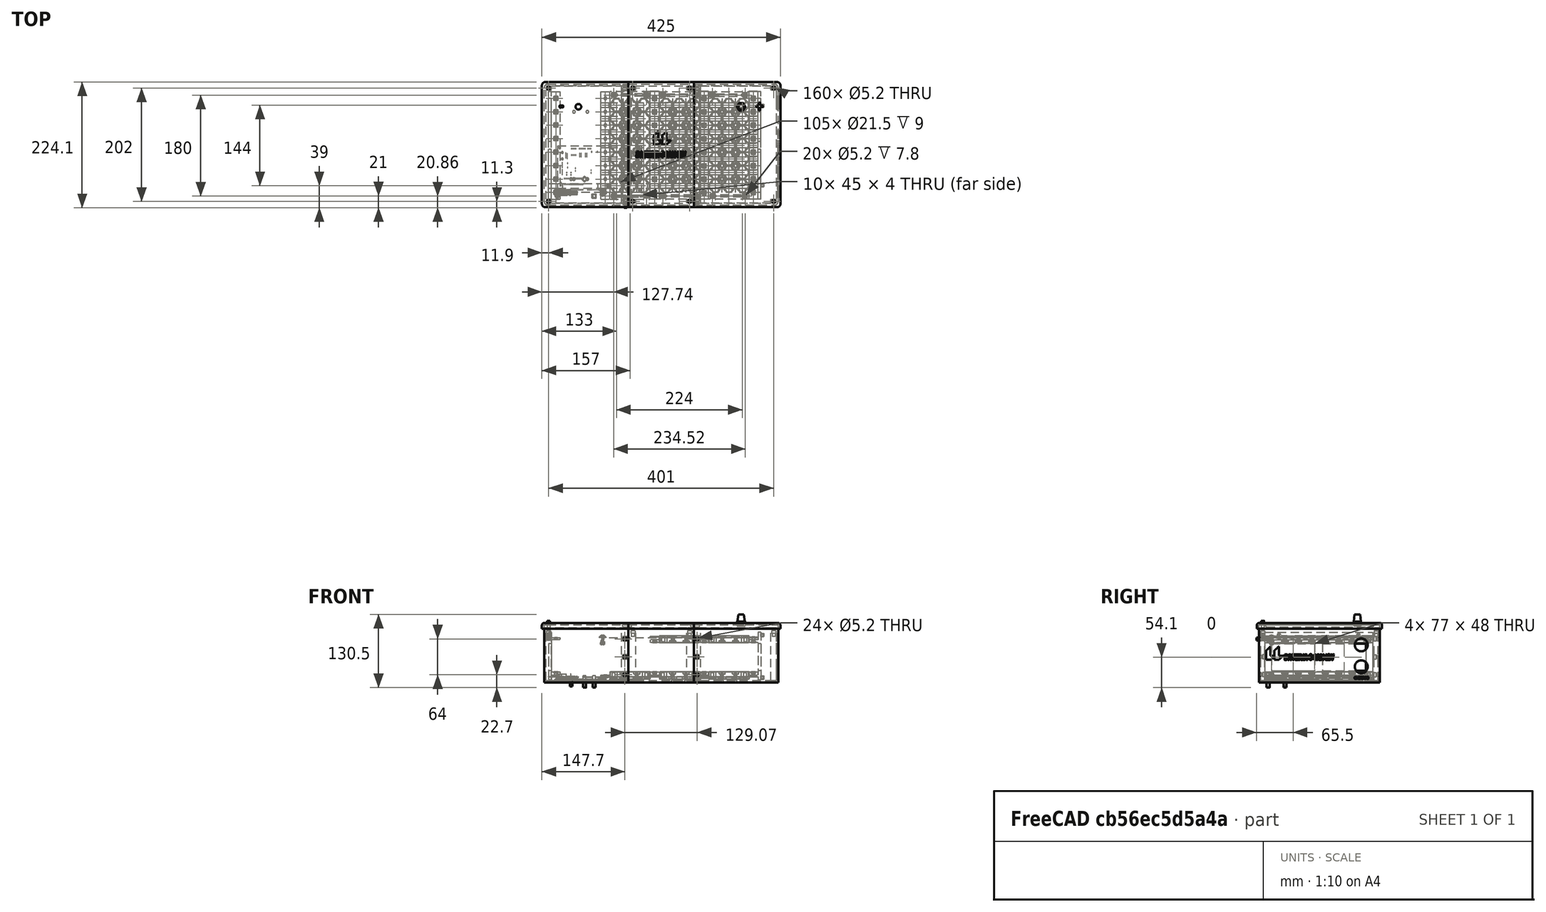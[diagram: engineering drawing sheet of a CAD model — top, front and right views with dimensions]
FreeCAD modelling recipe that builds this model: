
FCSTD DOCUMENT  (FreeCAD 0.19R24276 (Git))
Label: Caja_bateria_horizontal_10
License: All rights reserved
LicenseURL: http://en.wikipedia.org/wiki/All_rights_reserved
objects: TechDraw::DrawViewDimension×195, Part::Feature×111, App::Part×110, Part::FeaturePython×109, Mesh::Feature×86, Part::Cut×45, Part::Box×43, Part::MultiFuse×39, TechDraw::DrawProjGroupItem×37, App::DocumentObjectGroup×23, Part::Cylinder×18, TechDraw::DrawSVGTemplate×13, TechDraw::DrawPage×13, TechDraw::DrawProjGroup×12, TechDraw::DrawViewSymbol×12, TechDraw::DrawViewBalloon×11, TechDraw::DrawViewPart×10, Part::Fillet×6, Part::Extrusion×5, Part::Part2DObjectPython×4, +8 more types
note: 367 computed .brp shape members not serialized (recipe doc carries the construction recipe); baked Part::Feature solids carry a one-line shape summary decoded from their .brp

FEATURE [Mesh::Feature] _1700_Cell  label="21700_Cell"
  Placement = pos=(17,12,6) rot=(1,0,0;1.5708rad)
FEATURE [Part::Feature] Part__Feature  label="SOLID"
  shape: bbox 2.54 x 7.62 x 11.54 mm, 76 faces (baked)
FEATURE [App::Part] PinHeader_1x03_P2_54mm_Vertical  label="PinHeader_1x03_P2.54mm_Vertical"
  Group = -> [Part__Feature]
  Origin = -> Origin084
  Placement = pos=(53.975,78.359,1.65) rot=(0,0,1;1.5708rad)
FEATURE [Part::Feature] Part__Feature001  label="SOLID001"
  shape: bbox 2.54 x 12.7 x 11.54 mm, 124 faces (baked)
FEATURE [App::Part] PinHeader_1x05_P2_54mm_Vertical  label="PinHeader_1x05_P2.54mm_Vertical"
  Group = -> [Part__Feature001]
  Origin = -> Origin085
  Placement = pos=(142.875,23.749,1.65) rot=(0,0,1;0rad)
FEATURE [Part::Feature] Part__Feature002  label="SOLID002"
  shape: bbox 2.54 x 12.7 x 11.54 mm, 124 faces (baked)
FEATURE [App::Part] PinHeader_1x05_P2_54mm_Vertical001  label="PinHeader_1x05_P2.54mm_Vertical001"
  Group = -> [Part__Feature002]
  Origin = -> Origin086
  Placement = pos=(38.735,78.359,1.65) rot=(0,0,1;1.5708rad)
FEATURE [Part::Feature] Part__Feature003  label="SOLID003"
  shape: bbox 5.08 x 7.62 x 11.54 mm, 130 faces (baked)
FEATURE [App::Part] PinHeader_2x03_P2_54mm_Vertical  label="PinHeader_2x03_P2.54mm_Vertical"
  Group = -> [Part__Feature003]
  Origin = -> Origin087
  Placement = pos=(39.37,69.469,1.65) rot=(0,0,1;0rad)
FEATURE [Part::Feature] Part__Feature004  label="SOLID004"
  shape: bbox 5.08 x 7.62 x 11.54 mm, 130 faces (baked)
FEATURE [App::Part] PinHeader_2x03_P2_54mm_Vertical001  label="PinHeader_2x03_P2.54mm_Vertical001"
  Group = -> [Part__Feature004]
  Origin = -> Origin088
  Placement = pos=(49.53,69.469,1.65) rot=(0,0,1;0rad)
FEATURE [Part::Feature] Part__Feature005  label="SOLID005"
  shape: bbox 2.54 x 10.16 x 11.54 mm, 100 faces (baked)
FEATURE [App::Part] PinHeader_1x04_P2_54mm_Vertical  label="PinHeader_1x04_P2.54mm_Vertical"
  Group = -> [Part__Feature005]
  Origin = -> Origin089
  Placement = pos=(8.255,40.259,1.65) rot=(0,0,1;0rad)
FEATURE [Part::Feature] Part__Feature006  label="SOLID006"
  shape: bbox 2.54 x 10.16 x 11.54 mm, 100 faces (baked)
FEATURE [App::Part] PinHeader_1x04_P2_54mm_Vertical001  label="PinHeader_1x04_P2.54mm_Vertical001"
  Group = -> [Part__Feature006]
  Origin = -> Origin090
  Placement = pos=(24.765,66.929,1.65) rot=(0,0,1;1.5708rad)
FEATURE [Part::Feature] Part__Feature007  label="SOLID007"
  shape: bbox 2.54 x 10.16 x 11.54 mm, 100 faces (baked)
FEATURE [App::Part] PinHeader_1x04_P2_54mm_Vertical002  label="PinHeader_1x04_P2.54mm_Vertical002"
  Group = -> [Part__Feature007]
  Origin = -> Origin091
  Placement = pos=(24.765,78.359,1.65) rot=(0,0,1;1.5708rad)
FEATURE [Part::Feature] Part__Feature008  label="SOLID008"
  shape: bbox 2.54 x 10.16 x 11.54 mm, 100 faces (baked)
FEATURE [App::Part] PinHeader_1x04_P2_54mm_Vertical003  label="PinHeader_1x04_P2.54mm_Vertical003"
  Group = -> [Part__Feature008]
  Origin = -> Origin092
  Placement = pos=(8.255,52.959,1.65) rot=(0,0,1;0rad)
FEATURE [Part::Feature] Part__Feature009  label="SOLID009"
  shape: bbox 37.4 x 5.75 x 10.4 mm, 381 faces (baked)
FEATURE [App::Part] JST_XH_B14B_XH_A_1x14_P2_50mm_Vertical  label="JST_XH_B14B-XH-A_1x14_P2.50mm_Vertical"
  Group = -> [Part__Feature009]
  Origin = -> Origin093
  Placement = pos=(53.467,5.08,1.65) rot=(0,0,1;0rad)
FEATURE [Part::Feature] Part__Feature010  label="SOLID010"
  shape: bbox 37.4 x 5.75 x 10.4 mm, 381 faces (baked)
FEATURE [App::Part] JST_XH_B14B_XH_A_1x14_P2_50mm_Vertical001  label="JST_XH_B14B-XH-A_1x14_P2.50mm_Vertical001"
  Group = -> [Part__Feature010]
  Origin = -> Origin094
  Placement = pos=(12.065,14.732,1.65) rot=(0,0,1;0rad)
FEATURE [Part::Feature] Part__Feature011  label="SOLID011"
  shape: bbox 37.4 x 5.75 x 10.4 mm, 381 faces (baked)
FEATURE [App::Part] JST_XH_B14B_XH_A_1x14_P2_50mm_Vertical002  label="JST_XH_B14B-XH-A_1x14_P2.50mm_Vertical002"
  Group = -> [Part__Feature011]
  Origin = -> Origin095
  Placement = pos=(12.065,5.08,1.65) rot=(0,0,1;0rad)
FEATURE [Part::Feature] Part__Feature012  label="SOLID012"
  shape: bbox 37.4 x 5.75 x 10.4 mm, 381 faces (baked)
FEATURE [App::Part] JST_XH_B14B_XH_A_1x14_P2_50mm_Vertical003  label="JST_XH_B14B-XH-A_1x14_P2.50mm_Vertical003"
  Group = -> [Part__Feature012]
  Origin = -> Origin096
  Placement = pos=(12.065,25.019,1.65) rot=(0,0,1;0rad)
FEATURE [Part::Feature] Part__Feature013  label="SOLID013"
  shape: bbox 3.2 x 1.6 x 0.55 mm, 26 faces (baked)
FEATURE [App::Part] R_1206_3216Metric
  Group = -> [Part__Feature013]
  Origin = -> Origin097
  Placement = pos=(74.676,52.578,1.65) rot=(0,0,1;1.5708rad)
FEATURE [Part::Feature] Part__Feature014  label="SOLID014"
  shape: bbox 3.2 x 1.6 x 0.55 mm, 26 faces (baked)
FEATURE [App::Part] R_1206_3216Metric001
  Group = -> [Part__Feature014]
  Origin = -> Origin098
  Placement = pos=(64.135,36.068,1.65) rot=(0,0,-1;1.5708rad)
FEATURE [Part::Feature] Part__Feature015  label="SOLID015"
  shape: bbox 3.2 x 1.6 x 0.55 mm, 26 faces (baked)
FEATURE [App::Part] R_1206_3216Metric002
  Group = -> [Part__Feature015]
  Origin = -> Origin099
  Placement = pos=(3.429,15.24,1.65) rot=(0,0,-1;1.5708rad)
FEATURE [Part::Feature] Part__Feature016  label="SOLID016"
  shape: bbox 3.2 x 1.6 x 0.55 mm, 26 faces (baked)
FEATURE [App::Part] R_1206_3216Metric003
  Group = -> [Part__Feature016]
  Origin = -> Origin100
  Placement = pos=(106.934,24.638,1.65) rot=(0,0,1;0rad)
FEATURE [Part::Feature] Part__Feature017  label="SOLID017"
  shape: bbox 2.5 x 3 x 1.2 mm, 76 faces (baked)
FEATURE [App::Part] SOT_23  label="SOT-23"
  Group = -> [Part__Feature017]
  Origin = -> Origin101
  Placement = pos=(100.33,49.53,1.65) rot=(0,0,1;0rad)
FEATURE [Part::Feature] Part__Feature018  label="SOLID018"
  shape: bbox 9 x 9 x 1.1 mm, 524 faces (baked)
FEATURE [App::Part] TQFP_32_7x7mm_P0_8mm  label="TQFP-32_7x7mm_P0.8mm"
  Group = -> [Part__Feature018]
  Origin = -> Origin102
  Placement = pos=(65.151,54.102,1.65) rot=(0,0,1;0rad)
FEATURE [Part::Feature] Part__Feature019  label="SOLID019"
  shape: bbox 9 x 9 x 1.1 mm, 764 faces (baked)
FEATURE [App::Part] TQFP_48_7x7mm_P0_5mm  label="TQFP-48_7x7mm_P0.5mm"
  Group = -> [Part__Feature019]
  Origin = -> Origin103
  Placement = pos=(67.945,22.098,1.65) rot=(0,0,1;1.5708rad)
FEATURE [Part::Feature] Part__Feature020  label="SOLID020"
  shape: bbox 11.05 x 4.65 x 7 mm, 26 faces (baked)
FEATURE [App::Part] Crystal_HC49_4H_Vertical  label="Crystal_HC49-4H_Vertical"
  Group = -> [Part__Feature020]
  Origin = -> Origin104
  Placement = pos=(59.563,35.179,1.65) rot=(0,0,1;1.5708rad)
FEATURE [Part::Feature] Part__Feature021  label="SOLID021"
  shape: bbox 11.05 x 4.65 x 7 mm, 26 faces (baked)
FEATURE [App::Part] Crystal_HC49_4H_Vertical001  label="Crystal_HC49-4H_Vertical001"
  Group = -> [Part__Feature021]
  Origin = -> Origin105
  Placement = pos=(31.75,43.434,1.65) rot=(0,0,-1;1.5708rad)
FEATURE [Part::Feature] Part__Feature022  label="SOLID022"
  shape: bbox 10.35 x 15.9 x 2.99 mm, 756 faces (baked)
FEATURE [App::Part] SSOP_48_7_5x15_9mm_P0_635mm  label="SSOP-48_7.5x15.9mm_P0.635mm"
  Group = -> [Part__Feature022]
  Origin = -> Origin106
  Placement = pos=(124.46,46.609,1.65) rot=(0,0,1;0rad)
FEATURE [Part::Feature] Part__Feature023  label="SOLID023"
  shape: bbox 6 x 4.9 x 1.75 mm, 156 faces (baked)
FEATURE [App::Part] SOIC_8_3_9x4_9mm_P1_27mm  label="SOIC-8_3.9x4.9mm_P1.27mm"
  Group = -> [Part__Feature023]
  Origin = -> Origin107
  Placement = pos=(26.035,54.864,1.65) rot=(0,0,1;0rad)
FEATURE [Part::Feature] Part__Feature024  label="SOLID024"
  shape: bbox 10.3 x 11.55 x 2.75 mm, 306 faces (baked)
FEATURE [App::Part] SOIC_18W_7_5x11_6mm_P1_27mm  label="SOIC-18W_7.5x11.6mm_P1.27mm"
  Group = -> [Part__Feature024]
  Origin = -> Origin108
  Placement = pos=(43.815,41.529,1.65) rot=(0,0,1;0rad)
FEATURE [Part::Feature] Part__Feature025  label="SOLID025"
  shape: bbox 3.2 x 1.6 x 0.55 mm, 26 faces (baked)
FEATURE [App::Part] R_1206_3216Metric004
  Group = -> [Part__Feature025]
  Origin = -> Origin109
  Placement = pos=(87.122,52.578,1.65) rot=(0,0,1;0rad)
FEATURE [Part::Feature] Part__Feature026  label="SOLID026"
  shape: bbox 3.2 x 1.6 x 0.55 mm, 26 faces (baked)
FEATURE [App::Part] R_1206_3216Metric005
  Group = -> [Part__Feature026]
  Origin = -> Origin110
  Placement = pos=(87.63,39.243,1.65) rot=(0,0,1;0rad)
FEATURE [Part::Feature] Part__Feature027  label="SOLID027"
  shape: bbox 3.2 x 1.6 x 0.55 mm, 26 faces (baked)
FEATURE [App::Part] R_1206_3216Metric006
  Group = -> [Part__Feature027]
  Origin = -> Origin111
  Placement = pos=(87.122,25.273,1.65) rot=(0,0,1;0rad)
FEATURE [Part::Feature] Part__Feature028  label="SOLID028"
  shape: bbox 2 x 1.2 x 0.45 mm, 26 faces (baked)
FEATURE [App::Part] R_0805_2012Metric
  Group = -> [Part__Feature028]
  Origin = -> Origin112
  Placement = pos=(82.042,52.578,1.65) rot=(0,0,1;0rad)
FEATURE [Part::Feature] Part__Feature029  label="SOLID029"
  shape: bbox 2 x 1.2 x 0.45 mm, 26 faces (baked)
FEATURE [App::Part] R_0805_2012Metric001
  Group = -> [Part__Feature029]
  Origin = -> Origin113
  Placement = pos=(82.55,39.243,1.65) rot=(0,0,1;0rad)
FEATURE [Part::Feature] Part__Feature030  label="SOLID030"
  shape: bbox 2 x 1.2 x 0.45 mm, 26 faces (baked)
FEATURE [App::Part] R_0805_2012Metric002
  Group = -> [Part__Feature030]
  Origin = -> Origin114
  Placement = pos=(82.042,25.273,1.65) rot=(0,0,1;0rad)
FEATURE [Part::Feature] Part__Feature031  label="SOLID031"
  shape: bbox 2 x 1.2 x 0.45 mm, 26 faces (baked)
FEATURE [App::Part] R_0805_2012Metric003
  Group = -> [Part__Feature031]
  Origin = -> Origin115
  Placement = pos=(101.854,24.638,1.65) rot=(0,0,1;0rad)
FEATURE [Part::Feature] Part__Feature032  label="SOLID032"
  shape: bbox 3.2 x 1.6 x 0.55 mm, 26 faces (baked)
FEATURE [App::Part] R_1206_3216Metric007
  Group = -> [Part__Feature032]
  Origin = -> Origin116
  Placement = pos=(85.979,65.278,1.65) rot=(0,0,1;0rad)
FEATURE [Part::Feature] Part__Feature033  label="SOLID033"
  shape: bbox 3.2 x 1.6 x 0.55 mm, 26 faces (baked)
FEATURE [App::Part] R_1206_3216Metric008
  Group = -> [Part__Feature033]
  Origin = -> Origin117
  Placement = pos=(85.09,76.327,1.65) rot=(0,0,1;0rad)
FEATURE [Part::Feature] Part__Feature034  label="SOLID034"
  shape: bbox 3.2 x 1.6 x 0.55 mm, 26 faces (baked)
FEATURE [App::Part] R_1206_3216Metric009
  Group = -> [Part__Feature034]
  Origin = -> Origin118
  Placement = pos=(102.108,75.311,1.65) rot=(0,0,1;0rad)
FEATURE [Part::Feature] Part__Feature035  label="SOLID035"
  shape: bbox 3.2 x 1.6 x 0.55 mm, 26 faces (baked)
FEATURE [App::Part] R_1206_3216Metric010
  Group = -> [Part__Feature035]
  Origin = -> Origin119
  Placement = pos=(126.619,24.892,1.65) rot=(0,0,1;0rad)
FEATURE [Part::Feature] Part__Feature036  label="SOLID036"
  shape: bbox 2 x 1.2 x 0.45 mm, 26 faces (baked)
FEATURE [App::Part] R_0805_2012Metric004
  Group = -> [Part__Feature036]
  Origin = -> Origin120
  Placement = pos=(80.899,65.278,1.65) rot=(0,0,1;0rad)
FEATURE [Part::Feature] Part__Feature037  label="SOLID037"
  shape: bbox 2 x 1.2 x 0.45 mm, 26 faces (baked)
FEATURE [App::Part] R_0805_2012Metric005
  Group = -> [Part__Feature037]
  Origin = -> Origin121
  Placement = pos=(80.01,76.327,1.65) rot=(0,0,1;0rad)
FEATURE [Part::Feature] Part__Feature038  label="SOLID038"
  shape: bbox 2 x 1.2 x 0.45 mm, 26 faces (baked)
FEATURE [App::Part] R_0805_2012Metric006
  Group = -> [Part__Feature038]
  Origin = -> Origin122
  Placement = pos=(97.028,76.581,1.65) rot=(0,0,1;0rad)
FEATURE [Part::Feature] Part__Feature039  label="SOLID039"
  shape: bbox 2 x 1.2 x 0.45 mm, 26 faces (baked)
FEATURE [App::Part] R_0805_2012Metric007
  Group = -> [Part__Feature039]
  Origin = -> Origin123
  Placement = pos=(121.539,24.892,1.65) rot=(0,0,1;0rad)
FEATURE [Part::Feature] Part__Feature040  label="SOLID040"
  shape: bbox 3.2 x 1.6 x 0.55 mm, 26 faces (baked)
FEATURE [App::Part] R_1206_3216Metric011
  Group = -> [Part__Feature040]
  Origin = -> Origin124
  Placement = pos=(105.918,38.735,1.65) rot=(0,0,1;0rad)
FEATURE [Part::Feature] Part__Feature041  label="SOLID041"
  shape: bbox 3.2 x 1.6 x 0.55 mm, 26 faces (baked)
FEATURE [App::Part] R_1206_3216Metric012
  Group = -> [Part__Feature041]
  Origin = -> Origin125
  Placement = pos=(107.696,54.737,1.65) rot=(0,0,1;0rad)
FEATURE [Part::Feature] Part__Feature042  label="SOLID042"
  shape: bbox 3.2 x 1.6 x 0.55 mm, 26 faces (baked)
FEATURE [App::Part] R_1206_3216Metric013
  Group = -> [Part__Feature042]
  Origin = -> Origin126
  Placement = pos=(105.283,64.77,1.65) rot=(0,0,1;0rad)
FEATURE [Part::Feature] Part__Feature043  label="SOLID043"
  shape: bbox 3.2 x 1.6 x 0.55 mm, 26 faces (baked)
FEATURE [App::Part] R_1206_3216Metric014
  Group = -> [Part__Feature043]
  Origin = -> Origin127
  Placement = pos=(121.285,75.692,1.65) rot=(0,0,1;0rad)
FEATURE [Part::Feature] Part__Feature044  label="SOLID044"
  shape: bbox 2 x 1.2 x 0.45 mm, 26 faces (baked)
FEATURE [App::Part] R_0805_2012Metric008
  Group = -> [Part__Feature044]
  Origin = -> Origin128
  Placement = pos=(100.838,38.735,1.65) rot=(0,0,1;0rad)
FEATURE [Part::Feature] Part__Feature045  label="SOLID045"
  shape: bbox 2 x 1.2 x 0.45 mm, 26 faces (baked)
FEATURE [App::Part] R_0805_2012Metric009
  Group = -> [Part__Feature045]
  Origin = -> Origin129
  Placement = pos=(100.584,54.61,1.65) rot=(0,0,1;0rad)
FEATURE [Part::Feature] Part__Feature046  label="SOLID046"
  shape: bbox 2 x 1.2 x 0.45 mm, 26 faces (baked)
FEATURE [App::Part] R_0805_2012Metric010
  Group = -> [Part__Feature046]
  Origin = -> Origin130
  Placement = pos=(99.695,66.929,1.65) rot=(0,0,1;0rad)
FEATURE [Part::Feature] Part__Feature047  label="SOLID047"
  shape: bbox 2 x 1.2 x 0.45 mm, 26 faces (baked)
FEATURE [App::Part] R_0805_2012Metric011
  Group = -> [Part__Feature047]
  Origin = -> Origin131
  Placement = pos=(116.205,75.692,1.65) rot=(0,0,1;0rad)
FEATURE [Part::Feature] Part__Feature048  label="SOLID048"
  shape: bbox 3.2 x 1.6 x 0.55 mm, 26 faces (baked)
FEATURE [App::Part] R_1206_3216Metric015
  Group = -> [Part__Feature048]
  Origin = -> Origin132
  Placement = pos=(87.63,35.433,1.65) rot=(0,0,1;0rad)
FEATURE [Part::Feature] Part__Feature049  label="SOLID049"
  shape: bbox 3.2 x 1.6 x 0.55 mm, 26 faces (baked)
FEATURE [App::Part] R_1206_3216Metric016
  Group = -> [Part__Feature049]
  Origin = -> Origin133
  Placement = pos=(87.122,48.768,1.65) rot=(0,0,1;0rad)
FEATURE [Part::Feature] Part__Feature050  label="SOLID050"
  shape: bbox 3.2 x 1.6 x 0.55 mm, 26 faces (baked)
FEATURE [App::Part] R_1206_3216Metric017
  Group = -> [Part__Feature050]
  Origin = -> Origin134
  Placement = pos=(85.979,61.468,1.65) rot=(0,0,1;0rad)
FEATURE [Part::Feature] Part__Feature051  label="SOLID051"
  shape: bbox 3.2 x 1.6 x 0.55 mm, 26 faces (baked)
FEATURE [App::Part] R_1206_3216Metric018
  Group = -> [Part__Feature051]
  Origin = -> Origin135
  Placement = pos=(106.934,20.828,1.65) rot=(0,0,1;0rad)
FEATURE [Part::Feature] Part__Feature052  label="SOLID052"
  shape: bbox 3.2 x 1.6 x 0.55 mm, 26 faces (baked)
FEATURE [App::Part] R_1206_3216Metric019
  Group = -> [Part__Feature052]
  Origin = -> Origin136
  Placement = pos=(87.122,21.463,1.65) rot=(0,0,1;0rad)
FEATURE [Part::Feature] Part__Feature053  label="SOLID053"
  shape: bbox 3.2 x 1.6 x 0.55 mm, 26 faces (baked)
FEATURE [App::Part] R_1206_3216Metric020
  Group = -> [Part__Feature053]
  Origin = -> Origin137
  Placement = pos=(105.41,48.641,1.65) rot=(0,0,1;0rad)
FEATURE [Part::Feature] Part__Feature054  label="SOLID054"
  shape: bbox 3.2 x 1.6 x 0.55 mm, 26 faces (baked)
FEATURE [App::Part] R_1206_3216Metric021
  Group = -> [Part__Feature054]
  Origin = -> Origin138
  Placement = pos=(104.775,61.214,1.65) rot=(0,0,1;0rad)
FEATURE [Part::Feature] Part__Feature055  label="SOLID055"
  shape: bbox 3.2 x 1.6 x 0.55 mm, 26 faces (baked)
FEATURE [App::Part] R_1206_3216Metric022
  Group = -> [Part__Feature055]
  Origin = -> Origin139
  Placement = pos=(121.285,71.882,1.65) rot=(0,0,1;0rad)
FEATURE [Part::Feature] Part__Feature056  label="SOLID056"
  shape: bbox 3.2 x 1.6 x 0.55 mm, 26 faces (baked)
FEATURE [App::Part] R_1206_3216Metric023
  Group = -> [Part__Feature056]
  Origin = -> Origin140
  Placement = pos=(85.09,72.517,1.65) rot=(0,0,1;0rad)
FEATURE [Part::Feature] Part__Feature057  label="SOLID057"
  shape: bbox 3.2 x 1.6 x 0.55 mm, 26 faces (baked)
FEATURE [App::Part] R_1206_3216Metric024
  Group = -> [Part__Feature057]
  Origin = -> Origin141
  Placement = pos=(102.108,71.501,1.65) rot=(0,0,1;0rad)
FEATURE [Part::Feature] Part__Feature058  label="SOLID058"
  shape: bbox 3.2 x 1.6 x 0.55 mm, 26 faces (baked)
FEATURE [App::Part] R_1206_3216Metric025
  Group = -> [Part__Feature058]
  Origin = -> Origin142
  Placement = pos=(126.619,21.082,1.65) rot=(0,0,1;0rad)
FEATURE [Part::Feature] Part__Feature059  label="SOLID059"
  shape: bbox 3.2 x 1.6 x 0.55 mm, 26 faces (baked)
FEATURE [App::Part] R_1206_3216Metric026
  Group = -> [Part__Feature059]
  Origin = -> Origin143
  Placement = pos=(105.918,34.925,1.65) rot=(0,0,1;0rad)
FEATURE [Part::Feature] Part__Feature060  label="SOLID060"
  shape: bbox 3.2 x 1.6 x 0.55 mm, 26 faces (baked)
FEATURE [App::Part] R_1206_3216Metric027
  Group = -> [Part__Feature060]
  Origin = -> Origin144
  Placement = pos=(34.925,54.229,1.65) rot=(0,0,1;3.14159rad)
FEATURE [Part::Feature] Part__Feature061  label="SOLID061"
  shape: bbox 3.2 x 1.6 x 0.55 mm, 26 faces (baked)
FEATURE [App::Part] R_1206_3216Metric028
  Group = -> [Part__Feature061]
  Origin = -> Origin145
  Placement = pos=(63.627,65.786,1.65) rot=(0,0,1;0rad)
FEATURE [Part::Feature] Part__Feature062  label="SOLID062"
  shape: bbox 3.2 x 1.6 x 0.55 mm, 26 faces (baked)
FEATURE [App::Part] R_1206_3216Metric029
  Group = -> [Part__Feature062]
  Origin = -> Origin146
  Placement = pos=(118.237,59.69,1.65) rot=(0,0,1;0rad)
FEATURE [Part::Feature] Part__Feature063  label="SOLID063"
  shape: bbox 8.418 x 2.706 x 5.603 mm, 15 faces (baked)
FEATURE [App::Part] R_Axial_DIN0207_L6_3mm_D2_5mm_P7_62mm_Horizontal  label="R_Axial_DIN0207_L6.3mm_D2.5mm_P7.62mm_Horizontal"
  Group = -> [Part__Feature063]
  Origin = -> Origin147
  Placement = pos=(16.145,35.859,1.65) rot=(0,0,1;0rad)
FEATURE [Part::Feature] Part__Feature064  label="SOLID064"
  shape: bbox 8.418 x 2.706 x 5.603 mm, 15 faces (baked)
FEATURE [App::Part] R_Axial_DIN0207_L6_3mm_D2_5mm_P7_62mm_Horizontal001  label="R_Axial_DIN0207_L6.3mm_D2.5mm_P7.62mm_Horizontal001"
  Group = -> [Part__Feature064]
  Origin = -> Origin148
  Placement = pos=(16.145,31.809,1.65) rot=(0,0,1;0rad)
FEATURE [Part::Feature] Part__Feature065  label="SOLID065"
  shape: bbox 8.418 x 2.706 x 5.603 mm, 15 faces (baked)
FEATURE [App::Part] R_Axial_DIN0207_L6_3mm_D2_5mm_P7_62mm_Horizontal002  label="R_Axial_DIN0207_L6.3mm_D2.5mm_P7.62mm_Horizontal002"
  Group = -> [Part__Feature065]
  Origin = -> Origin149
  Placement = pos=(132.334,64.897,1.65) rot=(0,0,1;0rad)
FEATURE [Part::Feature] Part__Feature066  label="SOLID066"
  shape: bbox 8.418 x 2.706 x 5.603 mm, 15 faces (baked)
FEATURE [App::Part] R_Axial_DIN0207_L6_3mm_D2_5mm_P7_62mm_Horizontal003  label="R_Axial_DIN0207_L6.3mm_D2.5mm_P7.62mm_Horizontal003"
  Group = -> [Part__Feature066]
  Origin = -> Origin150
  Placement = pos=(145.034,64.897,1.65) rot=(0,0,-1;1.5708rad)
FEATURE [Part::Feature] Part__Feature067  label="SOLID067"
  shape: bbox 3.2 x 1.6 x 0.55 mm, 26 faces (baked)
FEATURE [App::Part] R_1206_3216Metric030
  Group = -> [Part__Feature067]
  Origin = -> Origin151
  Placement = pos=(145.415,38.989,1.65) rot=(0,0,1;1.5708rad)
FEATURE [Part::Feature] Part__Feature068  label="SOLID068"
  shape: bbox 2 x 1.2 x 0.45 mm, 26 faces (baked)
FEATURE [App::Part] R_0805_2012Metric012
  Group = -> [Part__Feature068]
  Origin = -> Origin152
  Placement = pos=(54.737,49.022,1.65) rot=(0,0,-1;1.5708rad)
FEATURE [Part::Feature] Part__Feature069  label="SOLID069"
  shape: bbox 8.418 x 2.706 x 5.603 mm, 15 faces (baked)
FEATURE [App::Part] R_Axial_DIN0207_L6_3mm_D2_5mm_P7_62mm_Horizontal004  label="R_Axial_DIN0207_L6.3mm_D2.5mm_P7.62mm_Horizontal004"
  Group = -> [Part__Feature069]
  Origin = -> Origin153
  Placement = pos=(17.78,44.704,1.65) rot=(0,0,1;1.5708rad)
FEATURE [Part::Feature] Part__Feature070  label="SOLID070"
  shape: bbox 2 x 1.2 x 0.45 mm, 26 faces (baked)
FEATURE [App::Part] R_0805_2012Metric013
  Group = -> [Part__Feature070]
  Origin = -> Origin154
  Placement = pos=(74.803,57.912,1.65) rot=(0,0,-1;1.5708rad)
FEATURE [Part::Feature] Part__Feature071  label="SOLID071"
  shape: bbox 2.5 x 3 x 1.2 mm, 76 faces (baked)
FEATURE [App::Part] SOT_23001  label="SOT-024"
  Group = -> [Part__Feature071]
  Origin = -> Origin155
  Placement = pos=(82.042,48.768,1.65) rot=(0,0,1;0rad)
FEATURE [Part::Feature] Part__Feature072  label="SOLID072"
  shape: bbox 2.5 x 3 x 1.2 mm, 76 faces (baked)
FEATURE [App::Part] SOT_23002  label="SOT-025"
  Group = -> [Part__Feature072]
  Origin = -> Origin156
  Placement = pos=(82.55,35.433,1.65) rot=(0,0,1;0rad)
FEATURE [Part::Feature] Part__Feature073  label="SOLID073"
  shape: bbox 2.5 x 3 x 1.2 mm, 76 faces (baked)
FEATURE [App::Part] SOT_23003  label="SOT-026"
  Group = -> [Part__Feature073]
  Origin = -> Origin157
  Placement = pos=(82.042,21.463,1.65) rot=(0,0,1;0rad)
FEATURE [Part::Feature] Part__Feature074  label="SOLID074"
  shape: bbox 2.5 x 3 x 1.2 mm, 76 faces (baked)
FEATURE [App::Part] SOT_23004  label="SOT-027"
  Group = -> [Part__Feature074]
  Origin = -> Origin158
  Placement = pos=(101.854,20.828,1.65) rot=(0,0,1;0rad)
FEATURE [Part::Feature] Part__Feature075  label="SOLID075"
  shape: bbox 2.5 x 3 x 1.2 mm, 76 faces (baked)
FEATURE [App::Part] SOT_23005  label="SOT-028"
  Group = -> [Part__Feature075]
  Origin = -> Origin159
  Placement = pos=(80.899,61.468,1.65) rot=(0,0,1;0rad)
FEATURE [Part::Feature] Part__Feature076  label="SOLID076"
  shape: bbox 2.5 x 3 x 1.2 mm, 76 faces (baked)
FEATURE [App::Part] SOT_23006  label="SOT-029"
  Group = -> [Part__Feature076]
  Origin = -> Origin160
  Placement = pos=(80.01,72.517,1.65) rot=(0,0,1;0rad)
FEATURE [Part::Feature] Part__Feature077  label="SOLID077"
  shape: bbox 2.5 x 3 x 1.2 mm, 76 faces (baked)
FEATURE [App::Part] SOT_23007  label="SOT-030"
  Group = -> [Part__Feature077]
  Origin = -> Origin161
  Placement = pos=(97.028,72.771,1.65) rot=(0,0,1;0rad)
FEATURE [Part::Feature] Part__Feature078  label="SOLID078"
  shape: bbox 2.5 x 3 x 1.2 mm, 76 faces (baked)
FEATURE [App::Part] SOT_23008  label="SOT-031"
  Group = -> [Part__Feature078]
  Origin = -> Origin162
  Placement = pos=(121.539,21.082,1.65) rot=(0,0,1;0rad)
FEATURE [Part::Feature] Part__Feature079  label="SOLID079"
  shape: bbox 2.5 x 3 x 1.2 mm, 76 faces (baked)
FEATURE [App::Part] SOT_23009  label="SOT-032"
  Group = -> [Part__Feature079]
  Origin = -> Origin163
  Placement = pos=(100.838,34.925,1.65) rot=(0,0,1;0rad)
FEATURE [Part::Feature] Part__Feature080  label="SOLID080"
  shape: bbox 2.5 x 3 x 1.2 mm, 76 faces (baked)
FEATURE [App::Part] SOT_23010  label="SOT-033"
  Group = -> [Part__Feature080]
  Origin = -> Origin164
  Placement = pos=(99.949,61.214,1.65) rot=(0,0,1;0rad)
FEATURE [Part::Feature] Part__Feature081  label="SOLID081"
  shape: bbox 2.5 x 3 x 1.2 mm, 76 faces (baked)
FEATURE [App::Part] SOT_23011  label="SOT-034"
  Group = -> [Part__Feature081]
  Origin = -> Origin165
  Placement = pos=(116.205,71.882,1.65) rot=(0,0,1;0rad)
FEATURE [Part::Feature] Part__Feature082  label="SOLID082"
  shape: bbox 7 x 6.5 x 1.7 mm, 78 faces (baked)
FEATURE [App::Part] SOT_223  label="SOT-223"
  Group = -> [Part__Feature082]
  Origin = -> Origin166
  Placement = pos=(138.43,48.514,1.65) rot=(0,0,1;0rad)
FEATURE [Part::Feature] Part__Feature083  label="SOLID083"
  shape: bbox 24.4 x 9.4 x 15 mm, 53 faces (baked)
FEATURE [App::Part] Fuseholder_Cylinder_5x20mm_Stelvio_Kontek_PTF78_Horizontal_Open  label="Fuseholder_Cylinder-5x20mm_Stelvio-Kontek_PTF78_Horizontal_Open"
  Group = -> [Part__Feature083]
  Origin = -> Origin167
  Placement = pos=(100.33,7.874,1.65) rot=(0,0,1;0rad)
FEATURE [Part::Feature] Part__Feature084  label="SOLID084"
  shape: bbox 11.53 x 3.72 x 6.71 mm, 13 faces (baked)
FEATURE [App::Part] D_5W_P10_16mm_Horizontal  label="D_5W_P10.16mm_Horizontal"
  Group = -> [Part__Feature084]
  Origin = -> Origin168
  Placement = pos=(60.579,72.644,1.65) rot=(0,0,1;0rad)
FEATURE [Part::Feature] Part__Feature085  label="SOLID085"
  shape: bbox 3.2 x 1.6 x 0.55 mm, 26 faces (baked)
FEATURE [App::Part] R_1206_3216Metric031
  Group = -> [Part__Feature085]
  Origin = -> Origin169
  Placement = pos=(92.71,35.433,1.65) rot=(0,0,1;0rad)
FEATURE [Part::Feature] Part__Feature086  label="SOLID086"
  shape: bbox 3.2 x 1.6 x 0.55 mm, 26 faces (baked)
FEATURE [App::Part] R_1206_3216Metric032
  Group = -> [Part__Feature086]
  Origin = -> Origin170
  Placement = pos=(92.202,48.768,1.65) rot=(0,0,1;0rad)
FEATURE [Part::Feature] Part__Feature087  label="SOLID087"
  shape: bbox 3.2 x 1.6 x 0.55 mm, 26 faces (baked)
FEATURE [App::Part] R_1206_3216Metric033
  Group = -> [Part__Feature087]
  Origin = -> Origin171
  Placement = pos=(91.059,61.468,1.65) rot=(0,0,1;0rad)
FEATURE [Part::Feature] Part__Feature088  label="SOLID088"
  shape: bbox 3.2 x 1.6 x 0.55 mm, 26 faces (baked)
FEATURE [App::Part] R_1206_3216Metric034
  Group = -> [Part__Feature088]
  Origin = -> Origin172
  Placement = pos=(112.014,20.828,1.65) rot=(0,0,1;0rad)
FEATURE [Part::Feature] Part__Feature089  label="SOLID089"
  shape: bbox 3.2 x 1.6 x 0.55 mm, 26 faces (baked)
FEATURE [App::Part] R_1206_3216Metric035
  Group = -> [Part__Feature089]
  Origin = -> Origin173
  Placement = pos=(92.202,21.463,1.65) rot=(0,0,1;0rad)
FEATURE [Part::Feature] Part__Feature090  label="SOLID090"
  shape: bbox 3.2 x 1.6 x 0.55 mm, 26 faces (baked)
FEATURE [App::Part] R_1206_3216Metric036
  Group = -> [Part__Feature090]
  Origin = -> Origin174
  Placement = pos=(110.49,48.641,1.65) rot=(0,0,1;0rad)
FEATURE [Part::Feature] Part__Feature091  label="SOLID091"
  shape: bbox 3.2 x 1.6 x 0.55 mm, 26 faces (baked)
FEATURE [App::Part] R_1206_3216Metric037
  Group = -> [Part__Feature091]
  Origin = -> Origin175
  Placement = pos=(109.855,61.214,1.65) rot=(0,0,1;0rad)
FEATURE [Part::Feature] Part__Feature092  label="SOLID092"
  shape: bbox 3.2 x 1.6 x 0.55 mm, 26 faces (baked)
FEATURE [App::Part] R_1206_3216Metric038
  Group = -> [Part__Feature092]
  Origin = -> Origin176
  Placement = pos=(126.365,71.882,1.65) rot=(0,0,1;0rad)
FEATURE [Part::Feature] Part__Feature093  label="SOLID093"
  shape: bbox 3.2 x 1.6 x 0.55 mm, 26 faces (baked)
FEATURE [App::Part] R_1206_3216Metric039
  Group = -> [Part__Feature093]
  Origin = -> Origin177
  Placement = pos=(90.17,72.517,1.65) rot=(0,0,1;0rad)
FEATURE [Part::Feature] Part__Feature094  label="SOLID094"
  shape: bbox 3.2 x 1.6 x 0.55 mm, 26 faces (baked)
FEATURE [App::Part] R_1206_3216Metric040
  Group = -> [Part__Feature094]
  Origin = -> Origin178
  Placement = pos=(107.188,71.501,1.65) rot=(0,0,1;0rad)
FEATURE [Part::Feature] Part__Feature095  label="SOLID095"
  shape: bbox 3.2 x 1.6 x 0.55 mm, 26 faces (baked)
FEATURE [App::Part] R_1206_3216Metric041
  Group = -> [Part__Feature095]
  Origin = -> Origin179
  Placement = pos=(131.699,21.082,1.65) rot=(0,0,1;0rad)
FEATURE [Part::Feature] Part__Feature096  label="SOLID096"
  shape: bbox 3.2 x 1.6 x 0.55 mm, 26 faces (baked)
FEATURE [App::Part] R_1206_3216Metric042
  Group = -> [Part__Feature096]
  Origin = -> Origin180
  Placement = pos=(110.998,34.925,1.65) rot=(0,0,1;0rad)
FEATURE [Part::Feature] Part__Feature097  label="SOLID097"
  shape: bbox 3.2 x 1.6 x 0.55 mm, 26 faces (baked)
FEATURE [App::Part] R_1206_3216Metric043
  Group = -> [Part__Feature097]
  Origin = -> Origin181
  Placement = pos=(57.277,64.77,1.65) rot=(0,0,1;1.5708rad)
FEATURE [Part::Feature] Part__Feature098  label="SOLID098"
  shape: bbox 3.2 x 1.6 x 0.55 mm, 26 faces (baked)
FEATURE [App::Part] R_1206_3216Metric044
  Group = -> [Part__Feature098]
  Origin = -> Origin182
  Placement = pos=(126.492,60.071,1.65) rot=(0,0,1;0rad)
FEATURE [Part::Feature] Part__Feature099  label="SOLID099"
  shape: bbox 3.2 x 1.6 x 0.55 mm, 26 faces (baked)
FEATURE [App::Part] R_1206_3216Metric045
  Group = -> [Part__Feature099]
  Origin = -> Origin183
  Placement = pos=(69.088,35.179,1.65) rot=(0,0,1;0rad)
FEATURE [Part::Feature] Part__Feature100  label="SOLID100"
  shape: bbox 3.2 x 1.6 x 0.55 mm, 26 faces (baked)
FEATURE [App::Part] R_1206_3216Metric046
  Group = -> [Part__Feature100]
  Origin = -> Origin184
  Placement = pos=(68.834,40.132,1.65) rot=(0,0,1;0rad)
FEATURE [Part::Feature] Part__Feature101  label="SOLID101"
  shape: bbox 3.2 x 1.6 x 0.55 mm, 26 faces (baked)
FEATURE [App::Part] R_1206_3216Metric047
  Group = -> [Part__Feature101]
  Origin = -> Origin185
  Placement = pos=(138.43,43.307,1.65) rot=(0,0,1;0rad)
FEATURE [Part::Feature] Part__Feature102  label="SOLID102"
  shape: bbox 3.2 x 1.6 x 0.55 mm, 26 faces (baked)
FEATURE [App::Part] R_1206_3216Metric048
  Group = -> [Part__Feature102]
  Origin = -> Origin186
  Placement = pos=(145.415,33.274,1.65) rot=(0,0,-1;1.5708rad)
FEATURE [Part::Feature] Part__Feature103  label="SOLID103"
  shape: bbox 3.2 x 1.6 x 0.55 mm, 26 faces (baked)
FEATURE [App::Part] R_1206_3216Metric049
  Group = -> [Part__Feature103]
  Origin = -> Origin187
  Placement = pos=(138.43,30.734,1.65) rot=(0,0,1;0rad)
FEATURE [Part::Feature] Part__Feature104  label="SOLID104"
  shape: bbox 3.2 x 1.6 x 0.55 mm, 26 faces (baked)
FEATURE [App::Part] R_1206_3216Metric050
  Group = -> [Part__Feature104]
  Origin = -> Origin188
  Placement = pos=(138.43,34.544,1.65) rot=(0,0,1;0rad)
FEATURE [Part::Feature] Part__Feature105  label="SOLID105"
  shape: bbox 3.2 x 1.6 x 0.55 mm, 26 faces (baked)
FEATURE [App::Part] R_1206_3216Metric051
  Group = -> [Part__Feature105]
  Origin = -> Origin189
  Placement = pos=(41.275,54.229,1.65) rot=(0,0,1;0rad)
FEATURE [Part::Feature] Part__Feature106  label="SOLID106"
  shape: bbox 3.2 x 1.6 x 0.55 mm, 26 faces (baked)
FEATURE [App::Part] R_1206_3216Metric052
  Group = -> [Part__Feature106]
  Origin = -> Origin190
  Placement = pos=(23.495,40.259,1.65) rot=(0,0,1;1.5708rad)
FEATURE [Part::Feature] Part__Feature107  label="SOLID107"
  shape: bbox 3.2 x 1.6 x 0.55 mm, 26 faces (baked)
FEATURE [App::Part] R_1206_3216Metric053
  Group = -> [Part__Feature107]
  Origin = -> Origin191
  Placement = pos=(20.32,40.259,1.65) rot=(0,0,1;1.5708rad)
FEATURE [Part::Feature] Part__Feature108  label="SOLID108"
  shape: bbox 3.2 x 1.6 x 0.55 mm, 26 faces (baked)
FEATURE [App::Part] R_1206_3216Metric054
  Group = -> [Part__Feature108]
  Origin = -> Origin192
  Placement = pos=(26.035,50.419,1.65) rot=(0,0,1;0rad)
FEATURE [Part::Feature] Part__Feature109  label="COMPOUND"
  shape: bbox 149.2 x 83.69 x 1.6 mm, 141 faces (baked)
FEATURE [App::Part] Open_CASCADE_STEP_translator_6_9_1  label="PCB BMS"
  Group = -> [PinHeader_1x03_P2_54mm_Vertical,PinHeader_1x05_P2_54mm_Vertical,PinHeader_1x05_P2_54mm_Vertical001,PinHeader_2x03_P2_54mm_Vertical,PinHeader_2x03_P2_54mm_Vertical001,PinHeader_1x04_P2_54mm_Vertical,PinHeader_1x04_P2_54mm_Vertical001,PinHeader_1x04_P2_54mm_Vertical002,PinHeader_1x04_P2_54mm_Vertical003,JST_XH_B14B_XH_A_1x14_P2_50mm_Vertical,JST_XH_B14B_XH_A_1x14_P2_50mm_Vertical001,+99 more]
  Origin = -> Origin193
  Placement = pos=(367,9.5,1) rot=(0.57735,0.57735,0.57735;2.0944rad)
FEATURE [Part::Cylinder] Cylinder  label="agujero_sup_izda"
  Angle = 360
  AttacherType = Attacher::AttachEngine3D
  Height = 6
  Placement = pos=(9.8,14.9,144) rot=(0,0,1;0rad)
  Radius = 1.6
FEATURE [Part::Cylinder] Cylinder001  label="agujero_sup_dcha"
  Angle = 360
  AttacherType = Attacher::AttachEngine3D
  Height = 6
  Placement = pos=(151.4,14.9,144) rot=(0,0,1;0rad)
  Radius = 1.6
FEATURE [Part::Cylinder] Cylinder002  label="agujero_inf_dcha"
  Angle = 360
  AttacherType = Attacher::AttachEngine3D
  Height = 6
  Placement = pos=(151.4,-61.1,144) rot=(0,0,1;0rad)
  Radius = 1.6
FEATURE [Part::Cylinder] Cylinder003  label="agujero_inf_izda"
  Angle = 360
  AttacherType = Attacher::AttachEngine3D
  Height = 6
  Placement = pos=(9.8,-61.1,144) rot=(0,0,1;0rad)
  Radius = 1.6
FEATURE [Part::Cylinder] Cylinder004  label="borde_agujero_sup_dcha"
  Angle = 360
  AttacherType = Attacher::AttachEngine3D
  Height = 5
  Placement = pos=(151.4,14.9,145) rot=(0,0,1;0rad)
  Radius = 3
FEATURE [Part::Cylinder] Cylinder005  label="borde_agujero_inf_dcha"
  Angle = 360
  AttacherType = Attacher::AttachEngine3D
  Height = 5
  Placement = pos=(151.4,-61.1,145) rot=(0,0,1;0rad)
  Radius = 3
FEATURE [Part::Cylinder] Cylinder006  label="borde_agujero_inf_izda"
  Angle = 360
  AttacherType = Attacher::AttachEngine3D
  Height = 5
  Placement = pos=(9.8,-61.1,145) rot=(0,0,1;0rad)
  Radius = 3
FEATURE [Part::Cylinder] Cylinder007  label="borde_agujero_sup_izda"
  Angle = 360
  AttacherType = Attacher::AttachEngine3D
  Height = 5
  Placement = pos=(9.8,14.9,145) rot=(0,0,1;0rad)
  Radius = 3
FEATURE [Part::MultiFuse] Fusion063  label="Borde_agujeros_PCB"
  Placement = pos=(212,3.5,66) rot=(0.57735,0.57735,0.57735;2.0944rad)
  Shapes = -> [Cylinder004,Cylinder007,Cylinder006,Cylinder005]
FEATURE [Part::MultiFuse] Fusion064  label="Agujeros_PCB"
  Placement = pos=(212,3.5,66) rot=(0.57735,0.57735,0.57735;2.0944rad)
  Shapes = -> [Cylinder,Cylinder003,Cylinder001,Cylinder002]
FEATURE [Sketcher::SketchObject] Sketch
  FullyConstrained = true
  MapMode = 5
  Support = -> [XY_Plane]
  sketch-geometry (5):
    g0: LineSegment StartX=0 StartY=0 StartZ=0 EndX=24 EndY=0 EndZ=0
    g1: LineSegment StartX=24 StartY=0 StartZ=0 EndX=24 EndY=-24 EndZ=0
    g2: LineSegment StartX=24 StartY=-24 StartZ=0 EndX=0 EndY=-24 EndZ=0
    g3: LineSegment StartX=0 StartY=-24 StartZ=0 EndX=0 EndY=0 EndZ=0
    g4: Circle CenterX=12 CenterY=-12 CenterZ=0 NormalX=0 NormalY=0 NormalZ=1 AngleXU=0 Radius=10.75
  constraints (15):
    c: Coincident(g0,g1)
    c: Coincident(g1,g2)
    c: Coincident(g2,g3)
    c: Coincident(g3,g0)
    c: Horizontal(g0)
    c: Horizontal(g2)
    c: Vertical(g1)
    c: Vertical(g3)
    c: DistanceX(g0,g0) = 24
    c: DistanceY(g1,g1) = 24
    c: PointOnObject(g0,g-1)
    c: PointOnObject(g-1,g3)
    c: Diameter(g4) = 21.5
    c: DistanceX(g0,g4) = 12
    c: DistanceY(g4,g0) = 12
FEATURE [PartDesign::Pad] Pad
  AllowMultiFace = false
  Direction = (1,1,1)
  Length = 9
  Length2 = 100
  Profile = -> Sketch
  Type = 0
FEATURE [Sketcher::SketchObject] Sketch001
  ExternalGeometry = -> [Pad]
  FullyConstrained = true
  MapMode = 5
  Placement = pos=(0,0,9) rot=(0,0,1;0rad)
  Support = -> [Pad]
  sketch-geometry (20):
    g0: LineSegment StartX=24 StartY=0 StartZ=0 EndX=17 EndY=0 EndZ=0
    g1: LineSegment StartX=17 StartY=0 StartZ=0 EndX=17 EndY=-4 EndZ=0
    g2: LineSegment StartX=20 StartY=-7 StartZ=0 EndX=24 EndY=-7 EndZ=0
    g3: LineSegment StartX=24 StartY=-7 StartZ=0 EndX=24 EndY=0 EndZ=0
    g4: ArcOfCircle CenterX=20 CenterY=-4 CenterZ=0 NormalX=0 NormalY=0 NormalZ=1 AngleXU=0 Radius=3 StartAngle=3.14159 EndAngle=4.71239
    g5: LineSegment StartX=0 StartY=0 StartZ=0 EndX=7 EndY=0 EndZ=0
    g6: LineSegment StartX=7 StartY=0 StartZ=0 EndX=7 EndY=-4 EndZ=0
    g7: LineSegment StartX=4 StartY=-7 StartZ=0 EndX=0 EndY=-7 EndZ=0
    g8: LineSegment StartX=0 StartY=-7 StartZ=0 EndX=0 EndY=0 EndZ=0
    g9: ArcOfCircle CenterX=4 CenterY=-4 CenterZ=0 NormalX=0 NormalY=0 NormalZ=1 AngleXU=0 Radius=3 StartAngle=4.71239 EndAngle=6.28319
    g10: LineSegment StartX=0 StartY=-24 StartZ=0 EndX=7 EndY=-24 EndZ=0
    g11: LineSegment StartX=7 StartY=-24 StartZ=0 EndX=7 EndY=-20 EndZ=0
    g12: LineSegment StartX=4 StartY=-17 StartZ=0 EndX=0 EndY=-17 EndZ=0
    g13: LineSegment StartX=0 StartY=-17 StartZ=0 EndX=0 EndY=-24 EndZ=0
    g14: LineSegment StartX=24 StartY=-24 StartZ=0 EndX=17 EndY=-24 EndZ=0
    g15: LineSegment StartX=17 StartY=-24 StartZ=0 EndX=17 EndY=-20 EndZ=0
    g16: LineSegment StartX=20 StartY=-17 StartZ=0 EndX=24 EndY=-17 EndZ=0
    g17: LineSegment StartX=24 StartY=-17 StartZ=0 EndX=24 EndY=-24 EndZ=0
    g18: ArcOfCircle CenterX=20 CenterY=-20 CenterZ=0 NormalX=0 NormalY=0 NormalZ=1 AngleXU=0 Radius=3 StartAngle=1.5708 EndAngle=3.14159
    g19: ArcOfCircle CenterX=4 CenterY=-20 CenterZ=0 NormalX=0 NormalY=0 NormalZ=1 AngleXU=0 Radius=3 StartAngle=2e-16 EndAngle=1.5708
  constraints (56):
    c: Coincident(g0,g1)
    c: Coincident(g2,g3)
    c: Coincident(g3,g0)
    c: Horizontal(g0)
    c: Horizontal(g2)
    c: Vertical(g1)
    c: Vertical(g3)
    c: DistanceX(g0,g0) = 7
    c: DistanceY(g3,g3) = 7
    c: PointOnObject(g-5,g3)
    c: PointOnObject(g-5,g0)
    c: Tangent(g2,g4) = -1.5708
    c: Tangent(g1,g4) = -1.5708
    c: Radius(g4) = 3
    c: Coincident(g5,g6)
    c: Coincident(g7,g8)
    c: Coincident(g8,g5)
    c: Horizontal(g5)
    c: Horizontal(g7)
    c: Vertical(g6)
    c: Vertical(g8)
    c: DistanceX(g5,g5) = 7
    c: PointOnObject(g-1,g8)
    c: PointOnObject(g-1,g5)
    c: Tangent(g7,g9) = 1.5708
    c: Tangent(g6,g9) = 1.5708
    c: Radius(g9) = 3
    c: DistanceY(g8,g8) = 7
    c: Coincident(g10,g11)
    c: Coincident(g12,g13)
    c: Coincident(g13,g10)
    c: Horizontal(g10)
    c: Horizontal(g12)
    c: Vertical(g11)
    c: Vertical(g13)
    c: PointOnObject(g-6,g13)
    c: PointOnObject(g10,g-4)
    c: Coincident(g14,g15)
    c: Coincident(g16,g17)
    c: Coincident(g17,g14)
    c: Horizontal(g14)
    c: Horizontal(g16)
    c: Vertical(g15)
    c: Vertical(g17)
    c: PointOnObject(g-4,g14)
    c: PointOnObject(g-4,g17)
    c: Tangent(g15,g18) = 1.5708
    c: Tangent(g16,g18) = 1.5708
    c: Tangent(g11,g19) = -1.5708
    c: Tangent(g12,g19) = -1.5708
    c: Radius(g18) = 3
    c: DistanceY(g17,g17) = 7
    c: DistanceX(g14,g14) = 7
    c: Radius(g19) = 3
    c: DistanceY(g13,g13) = 7
    c: DistanceX(g10,g10) = 7
FEATURE [PartDesign::Pad] Pad001
  AllowMultiFace = false
  BaseFeature = -> Pad
  Direction = (1,1,1)
  Length = 3.4
  Length2 = 100
  Profile = -> Sketch001
  Type = 0
FEATURE [PartDesign::Body] Body  label="Soporte_Celdas_21700"
  Group = -> [Sketch,Pad,Sketch001,Pad001]
  Origin = -> Origin
  Placement = pos=(23.5,47,9) rot=(0,1,0;3.14159rad)
  Tip = -> Pad001
FEATURE [Part::Cylinder] Cylinder028  label="AgujeroM5"
  Angle = 360
  AttacherType = Attacher::AttachEngine3D
  Height = 21
  Placement = pos=(79,0,-5) rot=(0,0,1;0rad)
  Radius = 2.6
FEATURE [Part::Box] Box009  label="Tuerca_Cuadrada_M4"
  AttacherType = Attacher::AttachEngine3D
  Height = 3.7
  Length = 7.7
  Placement = pos=(75.15,-3.8,13) rot=(0,0,1;0rad)
  Width = 7.7
FEATURE [Part::FeaturePython] Array  label="Base_Celdas"  # Draft array (typed FeaturePython)
  Angle = 360
  ArrayType = 0
  Axis = (0,0,1)
  Base = -> Body
  Center = (0,0,0)
  Fuse = false
  IntervalAxis = (0,0,0)
  IntervalX = (24,0,0)
  IntervalY = (0,-24,0)
  IntervalZ = (0,0,1)
  NumberPolar = 1
  NumberX = 7
  NumberY = 3
  NumberZ = 1
  Placement = pos=(47,0.5,6) rot=(0,0,1;1.5708rad)
FEATURE [Part::Box] Box010  label="Solapa_lat_inf"
  AttacherType = Attacher::AttachEngine3D
  Height = 5.5
  Length = 16
  Placement = pos=(72,-12,9.5) rot=(0,0,1;0rad)
  Width = 192
FEATURE [Part::MultiFuse] Fusion  label="Agujero+Tuerca"
  Placement = pos=(0,0,-1) rot=(0,0,1;0rad)
  Shapes = -> [Box009,Cylinder028]
FEATURE [Part::FeaturePython] Array001  label="Array_Agujeros+Tuerca"  # Draft array (typed FeaturePython)
  Angle = 360
  ArrayType = 0
  Axis = (0,0,1)
  Base = -> Fusion
  Center = (0,0,0)
  Fuse = false
  IntervalAxis = (0,0,0)
  IntervalX = (0,0,0)
  IntervalY = (0,24,0)
  IntervalZ = (0,0,1)
  NumberPolar = 1
  NumberX = 1
  NumberY = 8
  NumberZ = 1
  Placement = pos=(1,0,0) rot=(0,0,1;0rad)
FEATURE [Part::Box] Box013  label="Tapeta_Lateral001"
  AttacherType = Attacher::AttachEngine3D
  Height = 85
  Length = 5
  Placement = pos=(-26,-12,82) rot=(0,1,0;3.14159rad)
  Width = 192
FEATURE [Part::Box] Box014  label="Hueco_Tapa_Lateral"
  AttacherType = Attacher::AttachEngine3D
  Height = 48
  Length = 5
  Placement = pos=(-14,0,61.5) rot=(0,1,0;3.14159rad)
  Width = 77
FEATURE [Part::Box] Box015  label="Hueco_Tapa_Lateral001"
  AttacherType = Attacher::AttachEngine3D
  Height = 48
  Length = 5
  Placement = pos=(-14,91,61.5) rot=(0,1,0;3.14159rad)
  Width = 77
FEATURE [Part::MultiFuse] Fusion080
  Placement = pos=(-12,0,0) rot=(0,0,1;0rad)
  Shapes = -> [Box015,Box014]
FEATURE [Part::Cut] Cut001002024  label="Tapeta_Lateral_Hueca"
  Base = -> Box013
  Placement = pos=(10,0,3.6) rot=(0,0,1;0rad)
  Tool = -> Fusion080
FEATURE [Part::Box] Box  label="Cubo"
  AttacherType = Attacher::AttachEngine3D
  Height = 12.4
  Length = 72
  Placement = pos=(0,-12,2.6) rot=(0,0,1;0rad)
  Width = 12.1
FEATURE [Part::Box] Box018  label="Cubo001"
  AttacherType = Attacher::AttachEngine3D
  Height = 12.4
  Length = 45
  Placement = pos=(13.5,-8,2.6) rot=(0,0,1;0rad)
  Width = 4
FEATURE [Part::Cut] Cut001002026  label="Suplemento_Estructura_Celdas_Frontal"
  Base = -> Box
  Tool = -> Box018
FEATURE [Part::Cut] Cut001002027  label="Suplemento_Estructura_Celdas_Trasero"
  Base = -> Box
  Placement = pos=(72,168,0) rot=(0,0,1;3.14159rad)
  Tool = -> Box018
FEATURE [App::DocumentObjectGroup] Group001  label="PCBs"
  Group = -> [Open_CASCADE_STEP_translator_6_9_1]
FEATURE [Mesh::Feature] _1700_Cell001  label="21700_Cell001"
  Placement = pos=(41,12,6) rot=(1,0,0;1.5708rad)
FEATURE [Mesh::Feature] _1700_Cell002  label="21700_Cell002"
  Placement = pos=(65,12,6) rot=(1,0,0;1.5708rad)
FEATURE [Mesh::Feature] _1700_Cell003  label="21700_Cell003"
  Placement = pos=(65,36,6) rot=(1,0,0;1.5708rad)
FEATURE [Mesh::Feature] _1700_Cell004  label="21700_Cell004"
  Placement = pos=(41,36,6) rot=(1,0,0;1.5708rad)
FEATURE [Mesh::Feature] _1700_Cell005  label="21700_Cell005"
  Placement = pos=(17,36,6) rot=(1,0,0;1.5708rad)
FEATURE [Mesh::Feature] _1700_Cell006  label="21700_Cell006"
  Placement = pos=(17,84,6) rot=(1,0,0;1.5708rad)
FEATURE [Mesh::Feature] _1700_Cell007  label="21700_Cell007"
  Placement = pos=(41,84,6) rot=(1,0,0;1.5708rad)
FEATURE [Mesh::Feature] _1700_Cell008  label="21700_Cell008"
  Placement = pos=(65,84,6) rot=(1,0,0;1.5708rad)
FEATURE [Mesh::Feature] _1700_Cell009  label="21700_Cell009"
  Placement = pos=(65,60,6) rot=(1,0,0;1.5708rad)
FEATURE [Mesh::Feature] _1700_Cell010  label="21700_Cell010"
  Placement = pos=(41,60,6) rot=(1,0,0;1.5708rad)
FEATURE [Mesh::Feature] _1700_Cell011  label="21700_Cell011"
  Placement = pos=(17,60,6) rot=(1,0,0;1.5708rad)
FEATURE [Mesh::Feature] _1700_Cell012  label="21700_Cell012"
  Placement = pos=(17,108,6) rot=(1,0,0;1.5708rad)
FEATURE [Mesh::Feature] _1700_Cell013  label="21700_Cell013"
  Placement = pos=(41,108,6) rot=(1,0,0;1.5708rad)
FEATURE [Mesh::Feature] _1700_Cell014  label="21700_Cell014"
  Placement = pos=(65,108,6) rot=(1,0,0;1.5708rad)
FEATURE [Mesh::Feature] _1700_Cell015  label="21700_Cell015"
  Placement = pos=(65,132,6) rot=(1,0,0;1.5708rad)
FEATURE [Mesh::Feature] _1700_Cell016  label="21700_Cell016"
  Placement = pos=(41,132,6) rot=(1,0,0;1.5708rad)
FEATURE [Mesh::Feature] _1700_Cell017  label="21700_Cell017"
  Placement = pos=(17,132,6) rot=(1,0,0;1.5708rad)
FEATURE [Mesh::Feature] _1700_Cell018  label="21700_Cell018"
  Placement = pos=(17,156,6) rot=(1,0,0;1.5708rad)
FEATURE [Mesh::Feature] _1700_Cell019  label="21700_Cell019"
  Placement = pos=(41,156,6) rot=(1,0,0;1.5708rad)
FEATURE [Mesh::Feature] _1700_Cell020  label="21700_Cell020"
  Placement = pos=(65,156,6) rot=(1,0,0;1.5708rad)
FEATURE [Mesh::Feature] _1700_Cell021  label="21700_Cell021"
  Placement = pos=(129,156,76) rot=(0,0.707107,-0.707107;3.14159rad)
FEATURE [Mesh::Feature] _1700_Cell022  label="21700_Cell022"
  Placement = pos=(105,156,76) rot=(0,0.707107,-0.707107;3.14159rad)
FEATURE [Mesh::Feature] _1700_Cell023  label="21700_Cell023"
  Placement = pos=(153,156,76) rot=(0,0.707107,-0.707107;3.14159rad)
FEATURE [Mesh::Feature] _1700_Cell024  label="21700_Cell024"
  Placement = pos=(153,132,76) rot=(0,0.707107,-0.707107;3.14159rad)
FEATURE [Mesh::Feature] _1700_Cell025  label="21700_Cell025"
  Placement = pos=(129,132,76) rot=(0,0.707107,-0.707107;3.14159rad)
FEATURE [Mesh::Feature] _1700_Cell026  label="21700_Cell026"
  Placement = pos=(105,132,76) rot=(0,0.707107,-0.707107;3.14159rad)
FEATURE [Mesh::Feature] _1700_Cell027  label="21700_Cell027"
  Placement = pos=(105,108,76) rot=(0,0.707107,-0.707107;3.14159rad)
FEATURE [Mesh::Feature] _1700_Cell028  label="21700_Cell028"
  Placement = pos=(129,108,76) rot=(0,0.707107,-0.707107;3.14159rad)
FEATURE [Mesh::Feature] _1700_Cell029  label="21700_Cell029"
  Placement = pos=(153,108,76) rot=(0,0.707107,-0.707107;3.14159rad)
FEATURE [Mesh::Feature] _1700_Cell030  label="21700_Cell030"
  Placement = pos=(153,60,76) rot=(0,0.707107,-0.707107;3.14159rad)
FEATURE [Mesh::Feature] _1700_Cell031  label="21700_Cell031"
  Placement = pos=(105,60,76) rot=(0,0.707107,-0.707107;3.14159rad)
FEATURE [Mesh::Feature] _1700_Cell032  label="21700_Cell032"
  Placement = pos=(129,60,76) rot=(0,0.707107,-0.707107;3.14159rad)
FEATURE [Mesh::Feature] _1700_Cell033  label="21700_Cell033"
  Placement = pos=(105,84,76) rot=(0,0.707107,-0.707107;3.14159rad)
FEATURE [Mesh::Feature] _1700_Cell034  label="21700_Cell034"
  Placement = pos=(129,84,76) rot=(0,0.707107,-0.707107;3.14159rad)
FEATURE [Mesh::Feature] _1700_Cell035  label="21700_Cell035"
  Placement = pos=(153,36,76) rot=(0,0.707107,-0.707107;3.14159rad)
FEATURE [Mesh::Feature] _1700_Cell036  label="21700_Cell036"
  Placement = pos=(153,84,76) rot=(0,0.707107,-0.707107;3.14159rad)
FEATURE [Mesh::Feature] _1700_Cell037  label="21700_Cell037"
  Placement = pos=(129,36,76) rot=(0,0.707107,-0.707107;3.14159rad)
FEATURE [Mesh::Feature] _1700_Cell038  label="21700_Cell038"
  Placement = pos=(105,36,76) rot=(0,0.707107,-0.707107;3.14159rad)
FEATURE [Mesh::Feature] _1700_Cell039  label="21700_Cell039"
  Placement = pos=(105,12,76) rot=(0,0.707107,-0.707107;3.14159rad)
FEATURE [Mesh::Feature] _1700_Cell040  label="21700_Cell040"
  Placement = pos=(153,12,76) rot=(0,0.707107,-0.707107;3.14159rad)
FEATURE [Mesh::Feature] _1700_Cell041  label="21700_Cell041"
  Placement = pos=(129,12,76) rot=(0,0.707107,-0.707107;3.14159rad)
FEATURE [Mesh::Feature] _1700_Cell042  label="21700_Cell042"
  Placement = pos=(193,12,6) rot=(1,0,0;1.5708rad)
FEATURE [Mesh::Feature] _1700_Cell043  label="21700_Cell043"
  Placement = pos=(217,12,6) rot=(1,0,0;1.5708rad)
FEATURE [Mesh::Feature] _1700_Cell044  label="21700_Cell044"
  Placement = pos=(241,12,6) rot=(1,0,0;1.5708rad)
FEATURE [Mesh::Feature] _1700_Cell045  label="21700_Cell045"
  Placement = pos=(217,36,6) rot=(1,0,0;1.5708rad)
FEATURE [Mesh::Feature] _1700_Cell046  label="21700_Cell046"
  Placement = pos=(217,84,6) rot=(1,0,0;1.5708rad)
FEATURE [Mesh::Feature] _1700_Cell047  label="21700_Cell047"
  Placement = pos=(193,36,6) rot=(1,0,0;1.5708rad)
FEATURE [Mesh::Feature] _1700_Cell048  label="21700_Cell048"
  Placement = pos=(241,84,6) rot=(1,0,0;1.5708rad)
FEATURE [Mesh::Feature] _1700_Cell049  label="21700_Cell049"
  Placement = pos=(193,84,6) rot=(1,0,0;1.5708rad)
FEATURE [Mesh::Feature] _1700_Cell050  label="21700_Cell050"
  Placement = pos=(241,60,6) rot=(1,0,0;1.5708rad)
FEATURE [Mesh::Feature] _1700_Cell051  label="21700_Cell051"
  Placement = pos=(281,156,76) rot=(0,0.707107,-0.707107;3.14159rad)
FEATURE [Mesh::Feature] _1700_Cell052  label="21700_Cell052"
  Placement = pos=(305,156,76) rot=(0,0.707107,-0.707107;3.14159rad)
FEATURE [Mesh::Feature] _1700_Cell053  label="21700_Cell053"
  Placement = pos=(241,36,6) rot=(1,0,0;1.5708rad)
FEATURE [Mesh::Feature] _1700_Cell054  label="21700_Cell054"
  Placement = pos=(305,60,76) rot=(0,0.707107,-0.707107;3.14159rad)
FEATURE [Mesh::Feature] _1700_Cell055  label="21700_Cell055"
  Placement = pos=(193,60,6) rot=(1,0,0;1.5708rad)
FEATURE [Mesh::Feature] _1700_Cell056  label="21700_Cell056"
  Placement = pos=(305,12,76) rot=(0,0.707107,-0.707107;3.14159rad)
FEATURE [Mesh::Feature] _1700_Cell057  label="21700_Cell057"
  Placement = pos=(217,132,6) rot=(1,0,0;1.5708rad)
FEATURE [Mesh::Feature] _1700_Cell058  label="21700_Cell058"
  Placement = pos=(281,84,76) rot=(0,0.707107,-0.707107;3.14159rad)
FEATURE [Mesh::Feature] _1700_Cell059  label="21700_Cell059"
  Placement = pos=(241,108,6) rot=(1,0,0;1.5708rad)
FEATURE [Mesh::Feature] _1700_Cell060  label="21700_Cell060"
  Placement = pos=(329,36,76) rot=(0,0.707107,-0.707107;3.14159rad)
FEATURE [Mesh::Feature] _1700_Cell061  label="21700_Cell061"
  Placement = pos=(305,84,76) rot=(0,0.707107,-0.707107;3.14159rad)
FEATURE [Mesh::Feature] _1700_Cell062  label="21700_Cell062"
  Placement = pos=(329,156,76) rot=(0,0.707107,-0.707107;3.14159rad)
FEATURE [Mesh::Feature] _1700_Cell063  label="21700_Cell063"
  Placement = pos=(217,108,6) rot=(1,0,0;1.5708rad)
FEATURE [Mesh::Feature] _1700_Cell064  label="21700_Cell064"
  Placement = pos=(217,156,6) rot=(1,0,0;1.5708rad)
FEATURE [Mesh::Feature] _1700_Cell065  label="21700_Cell065"
  Placement = pos=(281,60,76) rot=(0,0.707107,-0.707107;3.14159rad)
FEATURE [Mesh::Feature] _1700_Cell066  label="21700_Cell066"
  Placement = pos=(193,156,6) rot=(1,0,0;1.5708rad)
FEATURE [Mesh::Feature] _1700_Cell067  label="21700_Cell067"
  Placement = pos=(329,132,76) rot=(0,0.707107,-0.707107;3.14159rad)
FEATURE [Mesh::Feature] _1700_Cell068  label="21700_Cell068"
  Placement = pos=(305,36,76) rot=(0,0.707107,-0.707107;3.14159rad)
FEATURE [Mesh::Feature] _1700_Cell069  label="21700_Cell069"
  Placement = pos=(241,156,6) rot=(1,0,0;1.5708rad)
FEATURE [Mesh::Feature] _1700_Cell070  label="21700_Cell070"
  Placement = pos=(193,108,6) rot=(1,0,0;1.5708rad)
FEATURE [Mesh::Feature] _1700_Cell071  label="21700_Cell071"
  Placement = pos=(329,60,76) rot=(0,0.707107,-0.707107;3.14159rad)
FEATURE [Mesh::Feature] _1700_Cell072  label="21700_Cell072"
  Placement = pos=(305,132,76) rot=(0,0.707107,-0.707107;3.14159rad)
FEATURE [Mesh::Feature] _1700_Cell073  label="21700_Cell073"
  Placement = pos=(281,108,76) rot=(0,0.707107,-0.707107;3.14159rad)
FEATURE [Mesh::Feature] _1700_Cell074  label="21700_Cell074"
  Placement = pos=(329,84,76) rot=(0,0.707107,-0.707107;3.14159rad)
FEATURE [Mesh::Feature] _1700_Cell075  label="21700_Cell075"
  Placement = pos=(329,108,76) rot=(0,0.707107,-0.707107;3.14159rad)
FEATURE [Mesh::Feature] _1700_Cell076  label="21700_Cell076"
  Placement = pos=(193,132,6) rot=(1,0,0;1.5708rad)
FEATURE [Mesh::Feature] _1700_Cell077  label="21700_Cell077"
  Placement = pos=(281,12,76) rot=(0,0.707107,-0.707107;3.14159rad)
FEATURE [Mesh::Feature] _1700_Cell078  label="21700_Cell078"
  Placement = pos=(305,108,76) rot=(0,0.707107,-0.707107;3.14159rad)
FEATURE [Mesh::Feature] _1700_Cell079  label="21700_Cell079"
  Placement = pos=(329,12,76) rot=(0,0.707107,-0.707107;3.14159rad)
FEATURE [Mesh::Feature] _1700_Cell080  label="21700_Cell080"
  Placement = pos=(217,60,6) rot=(1,0,0;1.5708rad)
FEATURE [Mesh::Feature] _1700_Cell081  label="21700_Cell081"
  Placement = pos=(281,132,76) rot=(0,0.707107,-0.707107;3.14159rad)
FEATURE [Mesh::Feature] _1700_Cell082  label="21700_Cell082"
  Placement = pos=(241,132,6) rot=(1,0,0;1.5708rad)
FEATURE [Mesh::Feature] _1700_Cell083  label="21700_Cell083"
  Placement = pos=(281,36,76) rot=(0,0.707107,-0.707107;3.14159rad)
FEATURE [App::DocumentObjectGroup] Group002  label="Celdas_21700"
  Group = -> [_1700_Cell,_1700_Cell001,_1700_Cell002,_1700_Cell003,_1700_Cell004,_1700_Cell005,_1700_Cell006,_1700_Cell007,_1700_Cell008,_1700_Cell009,_1700_Cell010,_1700_Cell011,_1700_Cell012,_1700_Cell013,_1700_Cell014,_1700_Cell015,_1700_Cell016,_1700_Cell017,_1700_Cell018,_1700_Cell019,_1700_Cell020,_1700_Cell021,_1700_Cell022,_1700_Cell023,_1700_Cell024,_1700_Cell025,_1700_Cell026,_1700_Cell027,+56 more]
FEATURE [Part::Box] Box032  label="Tuerca_Cuadrada_M5_1"
  AttacherType = Attacher::AttachEngine3D
  Height = 3.7
  Length = 7.8
  Placement = pos=(75.2,-3.8,-3.5) rot=(-0.099504,0,0.995037;0rad)
  Width = 7.8
FEATURE [Part::Cylinder] Cylinder029  label="AgujeroM5_1"
  Angle = 360
  AttacherType = Attacher::AttachEngine3D
  Height = 21
  Placement = pos=(79,0,-13) rot=(0,0,1;0rad)
  Radius = 2.6
FEATURE [Part::MultiFuse] Fusion084  label="Agujero_y_Tuerca"
  Placement = pos=(-7.86,79.86,0) rot=(0,0,-1;0.785398rad)
  Shapes = -> [Cylinder029,Box032]
FEATURE [Part::FeaturePython] Array003  label="Array_Huecos_Centrales"  # Draft array (typed FeaturePython)
  Angle = 360
  ArrayType = 0
  Axis = (0,0,1)
  Base = -> Fusion084
  Center = (0,0,0)
  Count = 12
  ExpandArray = false
  Fuse = false
  IntervalAxis = (0,0,0)
  IntervalX = (-24,0,0)
  IntervalY = (0,24,0)
  IntervalZ = (0,0,100)
  NumberCircles = 3
  NumberPolar = 5
  NumberX = 2
  NumberY = 6
  NumberZ = 1
  Placement = pos=(0,0,10) rot=(0,0,1;0rad)
  PlacementList = 12 placements: [(-7.86,79.86,0),(-7.86,103.86,0),(-7.86,127.86,0),(-7.86,151.86,0),(-7.86,175.86,0),(-7.86,199.86,0),(-31.86,79.86,0),(-31.86,103.86,0),(-31.86,127.86,0),(-31.86,151.86,0),(-31.86,175.86,0),(-31.86,199.86,0)]
  RadialDistance = 50
  ScaleList = (12) [(1,1,1),(1,1,1),(1,1,1),(1,1,1),(1,1,1),(1,1,1),(1,1,1),(1,1,1),(1,1,1),(1,1,1),(1,1,1),(1,1,1)]
  Symmetry = 1
  TangentialDistance = 25
FEATURE [Part::MultiFuse] Fusion085  label="Agujero_y_Tuerca001"
  Placement = pos=(-13.86,-6.14,0) rot=(0,0,-1;0rad)
  Shapes = -> [Cylinder029,Box032]
FEATURE [Part::FeaturePython] Array004  label="Array_huecos_Laterales"  # Draft array (typed FeaturePython)
  Angle = 360
  ArrayType = 0
  Axis = (0,0,1)
  Base = -> Fusion085
  Center = (0,0,0)
  Count = 4
  ExpandArray = false
  Fuse = false
  IntervalAxis = (0,0,0)
  IntervalX = (-58.4,0,0)
  IntervalY = (0,180,0)
  IntervalZ = (0,0,100)
  NumberCircles = 3
  NumberPolar = 5
  NumberX = 2
  NumberY = 2
  NumberZ = 1
  PlacementList = 4 placements: [(-13.86,-6.14,0),(-13.86,173.86,0),(-72.26,-6.14,0),(-72.26,173.86,0)]
  RadialDistance = 50
  ScaleList = (4) [(1,1,1),(1,1,1),(1,1,1),(1,1,1)]
  Symmetry = 1
  TangentialDistance = 25
FEATURE [Part::MultiFuse] Fusion086  label="Huecos_sujecion_Celdas"
  Placement = pos=(0,0,5) rot=(0,0,1;0rad)
  Shapes = -> [Array004,Array003]
FEATURE [Part::Box] Box033  label="Solapa_lat_sup"
  AttacherType = Attacher::AttachEngine3D
  Height = 3.5
  Length = 16
  Placement = pos=(-16,-12,6) rot=(0,0,1;0rad)
  Width = 192
FEATURE [Part::Box] Box034  label="Ranura_niquel"
  AttacherType = Attacher::AttachEngine3D
  Height = 0.5
  Length = 25
  Placement = pos=(-16,8,6) rot=(0,0,1;0rad)
  Width = 8.2
FEATURE [Part::FeaturePython] Array005  label="Ranuras_Niquel"  # Draft array (typed FeaturePython)
  Angle = 360
  ArrayType = 0
  Axis = (0,0,1)
  Base = -> Box034
  Center = (0,0,0)
  Count = 7
  ExpandArray = false
  Fuse = false
  IntervalAxis = (0,0,0)
  IntervalX = (0,100,0)
  IntervalY = (0,24,0)
  IntervalZ = (0,0,100)
  NumberCircles = 3
  NumberPolar = 5
  NumberX = 1
  NumberY = 7
  NumberZ = 1
  PlacementList = 7 placements: arithmetic series from (-16,8,6) step (0,24,0) to (-16,152,6)
  RadialDistance = 50
  ScaleList = (7) [(1,1,1),(1,1,1),(1,1,1),(1,1,1),(1,1,1),(1,1,1),(1,1,1)]
  Symmetry = 1
  TangentialDistance = 25
FEATURE [Part::Cut] Cut  label="Solapa_lat_sup_ranurada"
  Base = -> Box033
  Tool = -> Array005
FEATURE [Part::FeaturePython] Array006  label="Array_Agujeros+Tuerca002"  # Draft array (typed FeaturePython)
  Angle = 360
  ArrayType = 0
  Axis = (0,0,1)
  Base = -> Fusion
  Center = (0,0,0)
  Fuse = false
  IntervalAxis = (0,0,0)
  IntervalX = (0,0,0)
  IntervalY = (0,24,0)
  IntervalZ = (0,0,1)
  NumberPolar = 1
  NumberX = 1
  NumberY = 8
  NumberZ = 1
  Placement = pos=(-87,0,0) rot=(0,0,1;0rad)
FEATURE [Part::Cut] Cut001002033  label="Solapa_lat_sup_ranurada_taladrada"
  Base = -> Cut
  Tool = -> Array006
FEATURE [Part::Cut] Cut001002034  label="Solapa_lat_inf_taladrada"
  Base = -> Box010
  Tool = -> Array001
FEATURE [Part::MultiFuse] Fusion087  label="Modulo_celda"
  Shapes = -> [Array,Cut001002026,Cut001002027,Cut001002033,Cut001002034]
FEATURE [Part::Box] Box047  label="Pletina_Niquel"
  AttacherType = Attacher::AttachEngine3D
  Height = 0.2
  Length = 88
  Placement = pos=(0,8,5.8) rot=(0,0,1;0rad)
  Width = 8
FEATURE [Part::FeaturePython] Array015  label="Pletinas_Niquel_array"  # Draft array (typed FeaturePython)
  Angle = 360
  ArrayType = 0
  Axis = (0,0,1)
  Base = -> Box047
  Center = (0,0,0)
  Count = 7
  ExpandArray = false
  Fuse = false
  IntervalAxis = (0,0,0)
  IntervalX = (100,0,0)
  IntervalY = (0,24,0)
  IntervalZ = (0,0,100)
  NumberCircles = 3
  NumberPolar = 5
  NumberX = 1
  NumberY = 7
  NumberZ = 1
  Placement = pos=(77,0,0) rot=(0,0,1;0rad)
  PlacementList = 7 placements: arithmetic series from (0,8,5.8) step (0,24,0) to (0,152,5.8)
  RadialDistance = 50
  ScaleList = (7) [(1,1,1),(1,1,1),(1,1,1),(1,1,1),(1,1,1),(1,1,1),(1,1,1)]
  Symmetry = 1
  TangentialDistance = 25
FEATURE [Part::Box] Box048  label="Pletina_Cobre"
  AttacherType = Attacher::AttachEngine3D
  Height = 1
  Length = 16
  Placement = pos=(72,-12,4.8) rot=(0,0,1;0rad)
  Width = 193
FEATURE [Part::Cut] Cut001002045  label="Pletina_Cobre_taladrada"
  Base = -> Box048
  Placement = pos=(5,0,-1) rot=(0,0,1;0rad)
  Tool = -> Array001
FEATURE [Part::Box] Box051  label="Cubo006"
  AttacherType = Attacher::AttachEngine3D
  Height = 0.2
  Length = 17
  Placement = pos=(72,8,3.6) rot=(0,0,1;0rad)
  Width = 8
FEATURE [Part::Box] Box052  label="Cubo007"
  AttacherType = Attacher::AttachEngine3D
  Height = 0.2
  Length = 72
  Placement = pos=(88,8,5.8) rot=(0,0,1;0rad)
  Width = 8
FEATURE [Part::Box] Box053  label="Cubo008"
  AttacherType = Attacher::AttachEngine3D
  Height = 2
  Length = 1
  Placement = pos=(88,8,3.8) rot=(0,0,1;0rad)
  Width = 8
FEATURE [Part::MultiFuse] Fusion093  label="Pletina_Niquel_doblada"
  Shapes = -> [Box053,Box052,Box051]
FEATURE [Part::FeaturePython] Array017  label="Pletinas_Niquel_Dobladas_array"  # Draft array (typed FeaturePython)
  Angle = 360
  ArrayType = 0
  Axis = (0,0,1)
  Base = -> Fusion093
  Center = (0,0,0)
  Count = 7
  ExpandArray = false
  Fuse = false
  IntervalAxis = (0,0,0)
  IntervalX = (100,0,0)
  IntervalY = (0,24,0)
  IntervalZ = (0,0,100)
  NumberCircles = 3
  NumberPolar = 5
  NumberX = 1
  NumberY = 7
  NumberZ = 1
  Placement = pos=(165,168,0) rot=(0,0,1;3.14159rad)
  PlacementList = 7 placements: arithmetic series from (0,0,0) step (0,24,0) to (0,144,0)
  RadialDistance = 50
  ScaleList = (7) [(1,1,1),(1,1,1),(1,1,1),(1,1,1),(1,1,1),(1,1,1),(1,1,1)]
  Symmetry = 1
  TangentialDistance = 25
FEATURE [Part::Cylinder] Cylinder042  label="AgujeroM018"
  Angle = 360
  AttacherType = Attacher::AttachEngine3D
  Height = 21
  Placement = pos=(79,0,-5) rot=(0,0,1;0rad)
  Radius = 2.6
FEATURE [Part::Box] Box111  label="Tuerca_Cuadrada_M017"
  AttacherType = Attacher::AttachEngine3D
  Height = 3.7
  Length = 7.6
  Placement = pos=(75.2,-3.8,13) rot=(0,0,1;0rad)
  Width = 7.6
FEATURE [Part::Box] Box112  label="Solapa_lat_inf009"
  AttacherType = Attacher::AttachEngine3D
  Height = 5.5
  Length = 16
  Placement = pos=(72,-12,9.5) rot=(0,0,1;0rad)
  Width = 192
FEATURE [Part::MultiFuse] Fusion112  label="Agujero+Tuerca013"
  Shapes = -> [Box111,Cylinder042]
FEATURE [Part::FeaturePython] Array051  label="Array_Agujeros+Tuerca023"  # Draft array (typed FeaturePython)
  Angle = 360
  ArrayType = 0
  Axis = (0,0,1)
  Base = -> Fusion112
  Center = (0,0,0)
  Fuse = false
  IntervalAxis = (0,0,0)
  IntervalX = (0,0,0)
  IntervalY = (0,24,0)
  IntervalZ = (0,0,1)
  NumberPolar = 1
  NumberX = 1
  NumberY = 8
  NumberZ = 1
  Placement = pos=(1,0,0) rot=(0,0,1;0rad)
FEATURE [Part::Cut] Cut001002083  label="Solapa_lat_inf_taladrada009"
  Base = -> Box112
  Placement = pos=(-88,0,0) rot=(0,0,1;0rad)
  Tool = -> Array051
FEATURE [Part::Cylinder] Cylinder043  label="AgujeroM019"
  Angle = 360
  AttacherType = Attacher::AttachEngine3D
  Height = 21
  Placement = pos=(79,0,-5) rot=(0,0,1;0rad)
  Radius = 2.6
FEATURE [Part::Box] Box113  label="Tuerca_Cuadrada_M018"
  AttacherType = Attacher::AttachEngine3D
  Height = 3.7
  Length = 7.7
  Placement = pos=(75.2,-3.8,13) rot=(0,0,1;0rad)
  Width = 7.7
FEATURE [Part::MultiFuse] Fusion113  label="Agujero+Tuerca014"
  Shapes = -> [Box113,Cylinder043]
FEATURE [Part::Box] Box114  label="Solapa_lat_sup009"
  AttacherType = Attacher::AttachEngine3D
  Height = 3.5
  Length = 16
  Placement = pos=(-16,-12,7) rot=(0,0,1;0rad)
  Width = 192
FEATURE [Part::Box] Box115  label="Ranura_niquel009"
  AttacherType = Attacher::AttachEngine3D
  Height = 0.3
  Length = 16
  Placement = pos=(-16,8,6) rot=(0,0,1;0rad)
  Width = 8.2
FEATURE [Part::FeaturePython] Array052  label="Ranuras_Niquel009"  # Draft array (typed FeaturePython)
  Angle = 360
  ArrayType = 0
  Axis = (0,0,1)
  Base = -> Box115
  Center = (0,0,0)
  Count = 7
  ExpandArray = false
  Fuse = false
  IntervalAxis = (0,0,0)
  IntervalX = (0,100,0)
  IntervalY = (0,24,0)
  IntervalZ = (0,0,100)
  NumberCircles = 3
  NumberPolar = 5
  NumberX = 1
  NumberY = 7
  NumberZ = 1
  PlacementList = 7 placements: arithmetic series from (-16,8,6) step (0,24,0) to (-16,152,6)
  RadialDistance = 50
  ScaleList = (7) [(1,1,1),(1,1,1),(1,1,1),(1,1,1),(1,1,1),(1,1,1),(1,1,1)]
  Symmetry = 1
  TangentialDistance = 25
FEATURE [Part::Cut] Cut001002084  label="Solapa_lat_sup_ranurada009"
  Base = -> Box114
  Tool = -> Array052
FEATURE [Part::FeaturePython] Array053  label="Array_Agujeros+Tuerca024"  # Draft array (typed FeaturePython)
  Angle = 360
  ArrayType = 0
  Axis = (0,0,1)
  Base = -> Fusion113
  Center = (0,0,0)
  Fuse = false
  IntervalAxis = (0,0,0)
  IntervalX = (0,0,0)
  IntervalY = (0,24,0)
  IntervalZ = (0,0,1)
  NumberPolar = 1
  NumberX = 1
  NumberY = 8
  NumberZ = 1
  Placement = pos=(-87,0,0) rot=(0,0,1;0rad)
FEATURE [Part::Cut] Cut001002085  label="Solapa_lat_sup_ranurada_taladrada009"
  Base = -> Cut001002084
  Placement = pos=(0,0,65.6) rot=(0,0,1;0rad)
  Tool = -> Array053
FEATURE [Part::FeaturePython] Screw  label="M4x14-Screw"  # Fasteners workbench fastener (typed FeaturePython)
  Placement = pos=(80,0,77.2) rot=(0,0,1;0rad)
  diameter = 6
  invert = false
  length = 5
  lengthCustom = 14
  matchOuter = false
  offset = 0
  thread = true
  type = 34
FEATURE [Part::FeaturePython] Washer  label="M4-Washer"  # Fasteners workbench fastener (typed FeaturePython)
  Placement = pos=(80,0,76) rot=(0,0,1;0rad)
  diameter = 3
  invert = false
  matchOuter = false
  offset = 0
  type = 6
FEATURE [Part::FeaturePython] Nut  label="M4-Nut"  # Fasteners workbench fastener (typed FeaturePython)
  Placement = pos=(80,0,69) rot=(0,1,0;3.14159rad)
  diameter = 1
  invert = false
  matchOuter = false
  offset = 0
  thread = false
  type = 3
FEATURE [Part::MultiFuse] Fusion114  label="Tornillo_Tuerca_sin_pletina"
  Shapes = -> [Nut,Washer,Screw]
FEATURE [Part::FeaturePython] Array054  label="Pack_tornillo_Tuerca_sin_pletina"  # Draft array (typed FeaturePython)
  Angle = 360
  ArrayType = 0
  Axis = (0,0,1)
  Base = -> Fusion114
  Center = (0,0,0)
  Count = 8
  ExpandArray = false
  Fuse = false
  IntervalAxis = (0,0,0)
  IntervalX = (100,0,0)
  IntervalY = (0,24,0)
  IntervalZ = (0,0,100)
  NumberCircles = 3
  NumberPolar = 5
  NumberX = 1
  NumberY = 8
  NumberZ = 1
  Placement = pos=(5,0,0) rot=(0,0,1;0rad)
  PlacementList = 8 placements: arithmetic series from (0,0,0) step (0,24,0) to (0,168,0)
  RadialDistance = 50
  ScaleList = (8) [(1,1,1),(1,1,1),(1,1,1),(1,1,1),(1,1,1),(1,1,1),(1,1,1),(1,1,1)]
  Symmetry = 1
  TangentialDistance = 25
FEATURE [Part::FeaturePython] Screw001  label="M4x14-Screw001"  # Fasteners workbench fastener (typed FeaturePython)
  Placement = pos=(80,0,77.2) rot=(0,0,1;0rad)
  diameter = 6
  invert = false
  length = 5
  lengthCustom = 14
  matchOuter = false
  offset = 0
  thread = true
  type = 34
FEATURE [Part::FeaturePython] Washer001  label="M4-Washer001"  # Fasteners workbench fastener (typed FeaturePython)
  Placement = pos=(80,0,76) rot=(0,0,1;0rad)
  diameter = 3
  invert = false
  matchOuter = false
  offset = 0
  type = 6
FEATURE [Part::FeaturePython] Nut001  label="M4-Nut001"  # Fasteners workbench fastener (typed FeaturePython)
  Placement = pos=(80,0,67) rot=(0,1,0;3.14159rad)
  diameter = 1
  invert = false
  matchOuter = false
  offset = 0
  thread = false
  type = 3
FEATURE [Part::MultiFuse] Fusion115  label="Tornillo_Tuerca_con_pletinas"
  Shapes = -> [Nut001,Washer001,Screw001]
FEATURE [Part::FeaturePython] Array055  label="Pack_tornillo_Tuerca_con_pletinas"  # Draft array (typed FeaturePython)
  Angle = 360
  ArrayType = 0
  Axis = (0,0,1)
  Base = -> Fusion115
  Center = (0,0,0)
  Count = 8
  ExpandArray = false
  Fuse = false
  IntervalAxis = (0,0,0)
  IntervalX = (100,0,0)
  IntervalY = (0,24,0)
  IntervalZ = (0,0,100)
  NumberCircles = 3
  NumberPolar = 5
  NumberX = 1
  NumberY = 8
  NumberZ = 1
  Placement = pos=(165,0,79.6) rot=(0,1,0;3.14159rad)
  PlacementList = 8 placements: arithmetic series from (0,0,0) step (0,24,0) to (0,168,0)
  RadialDistance = 50
  ScaleList = (8) [(1,1,1),(1,1,1),(1,1,1),(1,1,1),(1,1,1),(1,1,1),(1,1,1),(1,1,1)]
  Symmetry = 1
  TangentialDistance = 25
FEATURE [Part::MultiFuse] Fusion116  label="Tapeta_Lateral_Izquierda"
  Placement = pos=(5,0,0) rot=(0,0,1;0rad)
  Shapes = -> [Cut001002024,Cut001002085,Cut001002083]
FEATURE [Part::FeaturePython] Washer002  label="M4-Washer002"  # Fasteners workbench fastener (typed FeaturePython)
  Placement = pos=(80,0,76) rot=(0,0,1;0rad)
  diameter = 3
  invert = false
  matchOuter = false
  offset = 0
  type = 6
FEATURE [Part::FeaturePython] Nut002  label="M4-Nut002"  # Fasteners workbench fastener (typed FeaturePython)
  Placement = pos=(80,0,67.2) rot=(0,1,0;3.14159rad)
  diameter = 1
  invert = false
  matchOuter = false
  offset = 0
  thread = false
  type = 3
FEATURE [Part::FeaturePython] Screw002  label="M4x14-Screw002"  # Fasteners workbench fastener (typed FeaturePython)
  Placement = pos=(80,0,77.2) rot=(0,0,1;0rad)
  diameter = 6
  invert = false
  length = 5
  lengthCustom = 14
  matchOuter = false
  offset = 0
  thread = true
  type = 34
FEATURE [Part::MultiFuse] Fusion117  label="Tornillo_Tuerca_con_pletinas001"
  Shapes = -> [Nut002,Washer002,Screw002]
FEATURE [Part::FeaturePython] Array056  label="Pack_tornillo_Tuerca_con_pletinas_Mod_B"  # Draft array (typed FeaturePython)
  Angle = 360
  ArrayType = 0
  Axis = (0,0,1)
  Base = -> Fusion117
  Center = (0,0,0)
  Count = 8
  ExpandArray = false
  Fuse = false
  IntervalAxis = (0,0,0)
  IntervalX = (100,0,0)
  IntervalY = (0,24,0)
  IntervalZ = (0,0,100)
  NumberCircles = 3
  NumberPolar = 5
  NumberX = 1
  NumberY = 8
  NumberZ = 1
  Placement = pos=(93,0,2.2) rot=(0,0,1;0rad)
  PlacementList = 8 placements: arithmetic series from (0,0,0) step (0,24,0) to (0,168,0)
  RadialDistance = 50
  ScaleList = (8) [(1,1,1),(1,1,1),(1,1,1),(1,1,1),(1,1,1),(1,1,1),(1,1,1),(1,1,1)]
  Symmetry = 1
  TangentialDistance = 25
FEATURE [Part::FeaturePython] Screw003  label="M4x14-Screw003"  # Fasteners workbench fastener (typed FeaturePython)
  Placement = pos=(80,0,77.2) rot=(0,0,1;0rad)
  diameter = 6
  invert = false
  length = 5
  lengthCustom = 14
  matchOuter = false
  offset = 0
  thread = true
  type = 34
FEATURE [Part::FeaturePython] Washer003  label="M4-Washer003"  # Fasteners workbench fastener (typed FeaturePython)
  Placement = pos=(80,0,76) rot=(0,0,1;0rad)
  diameter = 3
  invert = false
  matchOuter = false
  offset = 0
  type = 6
FEATURE [Part::FeaturePython] Nut003  label="M4-Nut003"  # Fasteners workbench fastener (typed FeaturePython)
  Placement = pos=(80,0,69) rot=(0,1,0;3.14159rad)
  diameter = 1
  invert = false
  matchOuter = false
  offset = 0
  thread = false
  type = 3
FEATURE [Part::MultiFuse] Fusion118  label="Tornillo_Tuerca_sin_pletina001"
  Shapes = -> [Nut003,Washer003,Screw003]
FEATURE [Part::FeaturePython] Array057  label="Pack_tornillo_Tuerca_sin_pletina_Mod_B"  # Draft array (typed FeaturePython)
  Angle = 360
  ArrayType = 0
  Axis = (0,0,1)
  Base = -> Fusion118
  Center = (0,0,0)
  Count = 8
  ExpandArray = false
  Fuse = false
  IntervalAxis = (0,0,0)
  IntervalX = (100,0,0)
  IntervalY = (0,24,0)
  IntervalZ = (0,0,100)
  NumberCircles = 3
  NumberPolar = 5
  NumberX = 1
  NumberY = 8
  NumberZ = 1
  Placement = pos=(253,0,82) rot=(0,1,0;3.14159rad)
  PlacementList = 8 placements: arithmetic series from (0,0,0) step (0,24,0) to (0,168,0)
  RadialDistance = 50
  ScaleList = (8) [(1,1,1),(1,1,1),(1,1,1),(1,1,1),(1,1,1),(1,1,1),(1,1,1),(1,1,1)]
  Symmetry = 1
  TangentialDistance = 25
FEATURE [Part::FeaturePython] Screw004  label="M4x14-Screw004"  # Fasteners workbench fastener (typed FeaturePython)
  Placement = pos=(80,0,77.2) rot=(0,0,1;0rad)
  diameter = 6
  invert = false
  length = 5
  lengthCustom = 14
  matchOuter = false
  offset = 0
  thread = true
  type = 34
FEATURE [Part::FeaturePython] Washer004  label="M4-Washer004"  # Fasteners workbench fastener (typed FeaturePython)
  Placement = pos=(80,0,76) rot=(0,0,1;0rad)
  diameter = 3
  invert = false
  matchOuter = false
  offset = 0
  type = 6
FEATURE [Part::FeaturePython] Nut004  label="M4-Nut004"  # Fasteners workbench fastener (typed FeaturePython)
  Placement = pos=(80,0,69) rot=(0,1,0;3.14159rad)
  diameter = 1
  invert = false
  matchOuter = false
  offset = 0
  thread = false
  type = 3
FEATURE [Part::MultiFuse] Fusion119  label="Tornillo_Tuerca_sin_pletina002"
  Shapes = -> [Nut004,Washer004,Screw004]
FEATURE [Part::FeaturePython] Array058  label="Pack_tornillo_Tuerca_sin_pletina_Mod_C"  # Draft array (typed FeaturePython)
  Angle = 360
  ArrayType = 0
  Axis = (0,0,1)
  Base = -> Fusion119
  Center = (0,0,0)
  Count = 8
  ExpandArray = false
  Fuse = false
  IntervalAxis = (0,0,0)
  IntervalX = (100,0,0)
  IntervalY = (0,24,0)
  IntervalZ = (0,0,100)
  NumberCircles = 3
  NumberPolar = 5
  NumberX = 1
  NumberY = 8
  NumberZ = 1
  Placement = pos=(181,0,0) rot=(0,0,1;0rad)
  PlacementList = 8 placements: arithmetic series from (0,0,0) step (0,24,0) to (0,168,0)
  RadialDistance = 50
  ScaleList = (8) [(1,1,1),(1,1,1),(1,1,1),(1,1,1),(1,1,1),(1,1,1),(1,1,1),(1,1,1)]
  Symmetry = 1
  TangentialDistance = 25
FEATURE [Part::FeaturePython] Washer005  label="M4-Washer005"  # Fasteners workbench fastener (typed FeaturePython)
  Placement = pos=(80,0,76) rot=(0,0,1;0rad)
  diameter = 3
  invert = false
  matchOuter = false
  offset = 0
  type = 6
FEATURE [Part::FeaturePython] Nut005  label="M4-Nut005"  # Fasteners workbench fastener (typed FeaturePython)
  Placement = pos=(80,0,67) rot=(0,1,0;3.14159rad)
  diameter = 1
  invert = false
  matchOuter = false
  offset = 0
  thread = false
  type = 3
FEATURE [Part::FeaturePython] Screw005  label="M4x14-Screw005"  # Fasteners workbench fastener (typed FeaturePython)
  Placement = pos=(80,0,77.2) rot=(0,0,1;0rad)
  diameter = 6
  invert = false
  length = 5
  lengthCustom = 14
  matchOuter = false
  offset = 0
  thread = true
  type = 34
FEATURE [Part::MultiFuse] Fusion120  label="Tornillo_Tuerca_con_pletinas002"
  Shapes = -> [Nut005,Washer005,Screw005]
FEATURE [Part::FeaturePython] Array059  label="Pack_tornillo_Tuerca_con_pletinas_Mod_C"  # Draft array (typed FeaturePython)
  Angle = 360
  ArrayType = 0
  Axis = (0,0,1)
  Base = -> Fusion120
  Center = (0,0,0)
  Count = 8
  ExpandArray = false
  Fuse = false
  IntervalAxis = (0,0,0)
  IntervalX = (100,0,0)
  IntervalY = (0,24,0)
  IntervalZ = (0,0,100)
  NumberCircles = 3
  NumberPolar = 5
  NumberX = 1
  NumberY = 8
  NumberZ = 1
  Placement = pos=(341,0,79.6) rot=(0,1,0;3.14159rad)
  PlacementList = 8 placements: arithmetic series from (0,0,0) step (0,24,0) to (0,168,0)
  RadialDistance = 50
  ScaleList = (8) [(1,1,1),(1,1,1),(1,1,1),(1,1,1),(1,1,1),(1,1,1),(1,1,1),(1,1,1)]
  Symmetry = 1
  TangentialDistance = 25
FEATURE [Part::FeaturePython] Screw006  label="M4x14-Screw006"  # Fasteners workbench fastener (typed FeaturePython)
  Placement = pos=(80,0,77.2) rot=(0,0,1;0rad)
  diameter = 6
  invert = false
  length = 5
  lengthCustom = 14
  matchOuter = false
  offset = 0
  thread = true
  type = 34
FEATURE [Part::FeaturePython] Washer006  label="M4-Washer006"  # Fasteners workbench fastener (typed FeaturePython)
  Placement = pos=(80,0,76) rot=(0,0,1;0rad)
  diameter = 3
  invert = false
  matchOuter = false
  offset = 0
  type = 6
FEATURE [Part::FeaturePython] Nut006  label="M4-Nut006"  # Fasteners workbench fastener (typed FeaturePython)
  Placement = pos=(80,0,68) rot=(0,1,0;3.14159rad)
  diameter = 1
  invert = false
  matchOuter = false
  offset = 0
  thread = false
  type = 3
FEATURE [Part::MultiFuse] Fusion121  label="Tornillo_Tuerca_Tapeta_sup"
  Shapes = -> [Nut006,Washer006,Screw006]
FEATURE [Part::FeaturePython] Array060  label="Pack_tornillo_Tuerca_Tapeta_Izda_sup"  # Draft array (typed FeaturePython)
  Angle = 360
  ArrayType = 0
  Axis = (0,0,1)
  Base = -> Fusion121
  Center = (0,0,0)
  Count = 8
  ExpandArray = false
  Fuse = false
  IntervalAxis = (0,0,0)
  IntervalX = (100,0,0)
  IntervalY = (0,24,0)
  IntervalZ = (0,0,100)
  NumberCircles = 3
  NumberPolar = 5
  NumberX = 1
  NumberY = 8
  NumberZ = 1
  Placement = pos=(-83,0,1) rot=(0,0,1;0rad)
  PlacementList = 8 placements: arithmetic series from (0,0,0) step (0,24,0) to (0,168,0)
  RadialDistance = 50
  ScaleList = (8) [(1,1,1),(1,1,1),(1,1,1),(1,1,1),(1,1,1),(1,1,1),(1,1,1),(1,1,1)]
  Symmetry = 1
  TangentialDistance = 25
FEATURE [Part::FeaturePython] Washer007  label="M4-Washer007"  # Fasteners workbench fastener (typed FeaturePython)
  Placement = pos=(80,0,76) rot=(0,0,1;0rad)
  diameter = 3
  invert = false
  matchOuter = false
  offset = 0
  type = 6
FEATURE [Part::FeaturePython] Nut007  label="M4-Nut007"  # Fasteners workbench fastener (typed FeaturePython)
  Placement = pos=(80,0,69) rot=(0,1,0;3.14159rad)
  diameter = 1
  invert = false
  matchOuter = false
  offset = 0
  thread = false
  type = 3
FEATURE [Part::FeaturePython] Screw007  label="M4x14-Screw007"  # Fasteners workbench fastener (typed FeaturePython)
  Placement = pos=(80,0,77.2) rot=(0,0,1;0rad)
  diameter = 6
  invert = false
  length = 5
  lengthCustom = 14
  matchOuter = false
  offset = 0
  thread = true
  type = 34
FEATURE [Part::MultiFuse] Fusion122  label="Tornillo_Tuerca_Tapeta_inf"
  Shapes = -> [Nut007,Washer007,Screw007]
FEATURE [Part::FeaturePython] Array061  label="Pack_tornillo_Tuerca_Tapeta_Izda_inf"  # Draft array (typed FeaturePython)
  Angle = 360
  ArrayType = 0
  Axis = (0,0,1)
  Base = -> Fusion122
  Center = (0,0,0)
  Count = 8
  ExpandArray = false
  Fuse = false
  IntervalAxis = (0,0,0)
  IntervalX = (100,0,0)
  IntervalY = (0,24,0)
  IntervalZ = (0,0,100)
  NumberCircles = 3
  NumberPolar = 5
  NumberX = 1
  NumberY = 8
  NumberZ = 1
  Placement = pos=(77,0,82) rot=(0,1,0;3.14159rad)
  PlacementList = 8 placements: arithmetic series from (0,0,0) step (0,24,0) to (0,168,0)
  RadialDistance = 50
  ScaleList = (8) [(1,1,1),(1,1,1),(1,1,1),(1,1,1),(1,1,1),(1,1,1),(1,1,1),(1,1,1)]
  Symmetry = 1
  TangentialDistance = 25
FEATURE [Part::Cut] Cut001002086  label="Modulo_celda_inf_A"
  Base = -> Fusion087
  Placement = pos=(5,0,0) rot=(0,0,1;0rad)
  Tool = -> Fusion086
FEATURE [App::DocumentObjectGroup] Group009  label="Soporte Inferior Mod A"
  Group = -> [Cut001002045,Cut001002086,Array017]
FEATURE [Part::FeaturePython] Clone  label="Modulo_celda_inf_B"  # Draft clone (typed FeaturePython)
  AttacherType = Attacher::AttachEngine3D
  Fuse = false
  Objects = -> [Cut001002086]
  Placement = pos=(93,0,0) rot=(0,0,1;0rad)
  Scale = (1,1,1)
FEATURE [Part::FeaturePython] Clone001  label="Modulo_celda_sup_A"  # Draft clone (typed FeaturePython)
  AttacherType = Attacher::AttachEngine3D
  Fuse = false
  Objects = -> [Cut001002086]
  Placement = pos=(77,0,82) rot=(0,1,0;3.14159rad)
  Scale = (1,1,1)
FEATURE [Part::FeaturePython] Clone002  label="Pletina_Cobre_taladrada_sup_izda_A"  # Draft clone (typed FeaturePython)
  AttacherType = Attacher::AttachEngine3D
  Fuse = false
  Objects = -> [Cut001002045]
  Placement = pos=(-83,0,71.2) rot=(0,0,1;0rad)
  Scale = (1,1,1)
FEATURE [Part::FeaturePython] Clone003  label="Pletinas_Niquel_sup_A"  # Draft clone (typed FeaturePython)
  AttacherType = Attacher::AttachEngine3D
  Fuse = false
  Objects = -> [Array015]
  Placement = pos=(-11,0,70.2) rot=(0,0,1;0rad)
  Scale = (1,1,1)
FEATURE [App::DocumentObjectGroup] Group010  label="Soporte Superior Mod A"
  Group = -> [Clone001,Clone002,Clone003]
FEATURE [App::DocumentObjectGroup] Group006  label="Modulo A Bateria"
  Group = -> [Group009,Group010]
FEATURE [Part::FeaturePython] Clone004  label="Modulo_celda_sup_B"  # Draft clone (typed FeaturePython)
  AttacherType = Attacher::AttachEngine3D
  Fuse = false
  Objects = -> [Clone001]
  Placement = pos=(165,0,82) rot=(0,1,0;3.14159rad)
  Scale = (1,1,1)
FEATURE [Part::FeaturePython] Clone005  label="Pletina_Cobre_taladrada_inf_B"  # Draft clone (typed FeaturePython)
  AttacherType = Attacher::AttachEngine3D
  Fuse = false
  Objects = -> [Cut001002045]
  Placement = pos=(5,0,0) rot=(0,0,1;0rad)
  Scale = (1,1,1)
FEATURE [App::DocumentObjectGroup] Group008  label="Soporte Inferior Mod B"
  Group = -> [Clone,Clone005,Array015]
FEATURE [Part::FeaturePython] Clone006  label="Pletinas_Niquel_sup_B"  # Draft clone (typed FeaturePython)
  AttacherType = Attacher::AttachEngine3D
  Fuse = false
  Objects = -> [Clone003]
  Placement = pos=(92,0,70.2) rot=(0,0,1;0rad)
  Scale = (1,1,1)
FEATURE [Part::FeaturePython] Clone007  label="Pletina_Cobre_taladrada_sup_B"  # Draft clone (typed FeaturePython)
  AttacherType = Attacher::AttachEngine3D
  Fuse = false
  Objects = -> [Cut001002045]
  Placement = pos=(93,0,71.2) rot=(0,0,1;0rad)
  Scale = (1,1,1)
FEATURE [App::DocumentObjectGroup] Group011  label="Soporte Superior Mod B"
  Group = -> [Clone004,Clone006,Clone007]
FEATURE [App::DocumentObjectGroup] Group007  label="Modulo B Bateria"
  Group = -> [Group008,Group011]
FEATURE [Part::FeaturePython] Clone008  label="Modulo_celda_sup_C"  # Draft clone (typed FeaturePython)
  AttacherType = Attacher::AttachEngine3D
  Fuse = false
  Objects = -> [Clone004]
  Placement = pos=(253,0,82) rot=(0,1,0;3.14159rad)
  Scale = (1,1,1)
FEATURE [Part::FeaturePython] Clone009  label="Pletinas_Niquel_Dobladas_array_sup_C"  # Draft clone (typed FeaturePython)
  AttacherType = Attacher::AttachEngine3D
  Fuse = false
  Objects = -> [Array017]
  Placement = pos=(93,168,82.0222) rot=(1,0,0;3.14159rad)
  Scale = (1,1,1)
FEATURE [Part::FeaturePython] Clone010  label="Pletina_Cobre_taladrada_sup_C"  # Draft clone (typed FeaturePython)
  AttacherType = Attacher::AttachEngine3D
  Fuse = false
  Objects = -> [Clone007]
  Placement = pos=(93,0,72.2) rot=(0,0,1;0rad)
  Scale = (1,1,1)
FEATURE [App::DocumentObjectGroup] Group020  label="Soporte Superior Mod C"
  Group = -> [Clone010,Clone009,Clone008]
FEATURE [Part::FeaturePython] Clone011  label="Modulo_celda_inf_C"  # Draft clone (typed FeaturePython)
  AttacherType = Attacher::AttachEngine3D
  Fuse = false
  Objects = -> [Cut001002086]
  Placement = pos=(181,0,0) rot=(0,0,1;0rad)
  Scale = (1,1,1)
FEATURE [Part::FeaturePython] Clone012  label="Pletinas_Niquel_Dobladas_array_inf_C"  # Draft clone (typed FeaturePython)
  AttacherType = Attacher::AttachEngine3D
  Fuse = false
  Objects = -> [Array017]
  Placement = pos=(341,168,0) rot=(0,0,1;3.14159rad)
  Scale = (1,1,1)
FEATURE [Part::FeaturePython] Clone013  label="Pletina_Cobre_taladrada_inf_C"  # Draft clone (typed FeaturePython)
  AttacherType = Attacher::AttachEngine3D
  Fuse = false
  Objects = -> [Cut001002045]
  Placement = pos=(181,0,-1) rot=(0,0,1;0rad)
  Scale = (1,1,1)
FEATURE [App::DocumentObjectGroup] Group021  label="Soporte Inferior Mod C"
  Group = -> [Clone013,Clone012,Clone011]
FEATURE [App::DocumentObjectGroup] Group014  label="Modulo C Bateria"
  Group = -> [Group020,Group021]
FEATURE [Part::FeaturePython] Clone014  label="Modulo_celda_inf_D"  # Draft clone (typed FeaturePython)
  AttacherType = Attacher::AttachEngine3D
  Fuse = false
  Objects = -> [Cut001002086]
  Placement = pos=(269,0,0) rot=(0,0,1;0rad)
  Scale = (1,1,1)
FEATURE [Part::FeaturePython] Clone015  label="Pletina_Cobre_taladrada_inf_D"  # Draft clone (typed FeaturePython)
  AttacherType = Attacher::AttachEngine3D
  Fuse = false
  Objects = -> [Clone005]
  Placement = pos=(181,0,0) rot=(0,0,1;0rad)
  Scale = (1,1,1)
FEATURE [Part::FeaturePython] Clone016  label="Pletinas_Niquel_array_inf_D"  # Draft clone (typed FeaturePython)
  AttacherType = Attacher::AttachEngine3D
  Fuse = false
  Objects = -> [Array015]
  Placement = pos=(253,0,0) rot=(0,0,1;0rad)
  Scale = (1,1,1)
FEATURE [App::DocumentObjectGroup] Group022  label="Soporte Inferior Mod D"
  Group = -> [Clone016,Clone015,Clone014]
FEATURE [Part::FeaturePython] Clone017  label="Modulo_celda_sup_D"  # Draft clone (typed FeaturePython)
  AttacherType = Attacher::AttachEngine3D
  Fuse = false
  Objects = -> [Clone001]
  Placement = pos=(341,0,82) rot=(0,1,0;3.14159rad)
  Scale = (1,1,1)
FEATURE [Part::FeaturePython] Clone018  label="Pletinas_Niquel_sup_D"  # Draft clone (typed FeaturePython)
  AttacherType = Attacher::AttachEngine3D
  Fuse = false
  Objects = -> [Clone003]
  Placement = pos=(269,0,70.2) rot=(0,0,1;0rad)
  Scale = (1,1,1)
FEATURE [Part::FeaturePython] Clone019  label="Pletina_Cobre_taladrada_sup_D"  # Draft clone (typed FeaturePython)
  AttacherType = Attacher::AttachEngine3D
  Fuse = false
  Objects = -> [Clone002]
  Placement = pos=(269,0,71.2) rot=(0,0,1;0rad)
  Scale = (1,1,1)
FEATURE [App::DocumentObjectGroup] Group023  label="Soporte Superior Mod D"
  Group = -> [Clone019,Clone018,Clone017]
FEATURE [App::DocumentObjectGroup] Group017  label="Modulo D Batería"
  Group = -> [Group023,Group022]
FEATURE [App::DocumentObjectGroup] Group  label="Estructura_Bateria"
  Group = -> [Group006,Group007,Group014,Group017]
FEATURE [Part::Cylinder] Cylinder044  label="AgujeroM020"
  Angle = 360
  AttacherType = Attacher::AttachEngine3D
  Height = 21
  Placement = pos=(79,0,-5) rot=(0,0,1;0rad)
  Radius = 2.6
FEATURE [Part::Box] Box116  label="Tuerca_Cuadrada_M019"
  AttacherType = Attacher::AttachEngine3D
  Height = 3.7
  Length = 7.7
  Placement = pos=(75.2,-3.8,13) rot=(0,0,1;0rad)
  Width = 7.7
FEATURE [Part::Box] Box117  label="Solapa_lat_inf010"
  AttacherType = Attacher::AttachEngine3D
  Height = 5.5
  Length = 16
  Placement = pos=(72,-12,9.5) rot=(0,0,1;0rad)
  Width = 192
FEATURE [Part::MultiFuse] Fusion123  label="Agujero+Tuerca015"
  Placement = pos=(0,0,-1) rot=(0,0,1;0rad)
  Shapes = -> [Box116,Cylinder044]
FEATURE [Part::FeaturePython] Array062  label="Array_Agujeros+Tuerca025"  # Draft array (typed FeaturePython)
  Angle = 360
  ArrayType = 0
  Axis = (0,0,1)
  Base = -> Fusion123
  Center = (0,0,0)
  Fuse = false
  IntervalAxis = (0,0,0)
  IntervalX = (0,0,0)
  IntervalY = (0,24,0)
  IntervalZ = (0,0,1)
  NumberPolar = 1
  NumberX = 1
  NumberY = 8
  NumberZ = 1
  Placement = pos=(1,0,0) rot=(0,0,1;0rad)
FEATURE [Part::Box] Box118  label="Solapa_lat_sup010"
  AttacherType = Attacher::AttachEngine3D
  Height = 3.5
  Length = 16
  Placement = pos=(-16,-12,6) rot=(0,0,1;0rad)
  Width = 192
FEATURE [Part::Box] Box119  label="Ranura_niquel010"
  AttacherType = Attacher::AttachEngine3D
  Height = 0.5
  Length = 25
  Placement = pos=(-16,8,6) rot=(0,0,1;0rad)
  Width = 8.2
FEATURE [Part::FeaturePython] Array063  label="Ranuras_Niquel010"  # Draft array (typed FeaturePython)
  Angle = 360
  ArrayType = 0
  Axis = (0,0,1)
  Base = -> Box119
  Center = (0,0,0)
  Count = 7
  ExpandArray = false
  Fuse = false
  IntervalAxis = (0,0,0)
  IntervalX = (0,100,0)
  IntervalY = (0,24,0)
  IntervalZ = (0,0,100)
  NumberCircles = 3
  NumberPolar = 5
  NumberX = 1
  NumberY = 7
  NumberZ = 1
  PlacementList = 7 placements: arithmetic series from (-16,8,6) step (0,24,0) to (-16,152,6)
  RadialDistance = 50
  ScaleList = (7) [(1,1,1),(1,1,1),(1,1,1),(1,1,1),(1,1,1),(1,1,1),(1,1,1)]
  Symmetry = 1
  TangentialDistance = 25
FEATURE [Part::Cut] Cut001002087  label="Solapa_lat_sup_ranurada010"
  Base = -> Box118
  Tool = -> Array063
FEATURE [Part::FeaturePython] Array064  label="Array_Agujeros+Tuerca026"  # Draft array (typed FeaturePython)
  Angle = 360
  ArrayType = 0
  Axis = (0,0,1)
  Base = -> Fusion123
  Center = (0,0,0)
  Fuse = false
  IntervalAxis = (0,0,0)
  IntervalX = (0,0,0)
  IntervalY = (0,24,0)
  IntervalZ = (0,0,1)
  NumberPolar = 1
  NumberX = 1
  NumberY = 8
  NumberZ = 1
  Placement = pos=(-87,0,0) rot=(0,0,1;0rad)
FEATURE [Part::Cut] Cut001002088  label="Solapa_lat_sup_ranurada_taladrada_Sop_Drcha"
  Base = -> Cut001002087
  Placement = pos=(352,0,0) rot=(0,0,1;0rad)
  Tool = -> Array064
FEATURE [Part::Cut] Cut001002089  label="Solapa_lat_inf_taladrada_Sop_Drcha"
  Base = -> Box117
  Placement = pos=(424,0,81.8548) rot=(0,1,0;3.14159rad)
  Tool = -> Array062
FEATURE [Part::Box] Box120  label="Hueco_Tapa_Lateral004"
  AttacherType = Attacher::AttachEngine3D
  Height = 48
  Length = 5
  Placement = pos=(-14,0,61.5) rot=(0,1,0;3.14159rad)
  Width = 77
FEATURE [Part::Box] Box121  label="Tapeta_Lateral002"
  AttacherType = Attacher::AttachEngine3D
  Height = 85
  Length = 5
  Placement = pos=(-26,-12,82) rot=(0,1,0;3.14159rad)
  Width = 192
FEATURE [Part::Box] Box122  label="Hueco_Tapa_Lateral005"
  AttacherType = Attacher::AttachEngine3D
  Height = 48
  Length = 5
  Placement = pos=(-14,91,61.5) rot=(0,1,0;3.14159rad)
  Width = 77
FEATURE [Part::MultiFuse] Fusion124
  Placement = pos=(-12,0,0) rot=(0,0,1;0rad)
  Shapes = -> [Box122,Box120]
FEATURE [Part::Cut] Cut001002090  label="Tapeta_Lateral_Drcha_Hueca"
  Base = -> Box121
  Placement = pos=(383,0,3.6) rot=(0,0,1;0rad)
  Tool = -> Fusion124
FEATURE [Part::Cut] Cut001002091  label="Soporte_Tornillos_PCB"
  Base = -> Fusion063
  Tool = -> Fusion064
FEATURE [Part::MultiFuse] Fusion125  label="Tapeta_Lateral_Derecha_PCB"
  Placement = pos=(5,0,0) rot=(0,0,1;0rad)
  Shapes = -> [Cut001002090,Cut001002089,Cut001002088,Cut001002091]
FEATURE [App::DocumentObjectGroup] Group019  label="Tapas Laterales"
  Group = -> [Fusion116,Fusion125]
FEATURE [Part::FeaturePython] Screw008  label="M4x14-Screw008"  # Fasteners workbench fastener (typed FeaturePython)
  Placement = pos=(80,0,77.2) rot=(0,0,1;0rad)
  diameter = 6
  invert = false
  length = 5
  lengthCustom = 14
  matchOuter = false
  offset = 0
  thread = true
  type = 34
FEATURE [Part::FeaturePython] Washer008  label="M4-Washer008"  # Fasteners workbench fastener (typed FeaturePython)
  Placement = pos=(80,0,76) rot=(0,0,1;0rad)
  diameter = 3
  invert = false
  matchOuter = false
  offset = 0
  type = 6
FEATURE [Part::FeaturePython] Nut008  label="M4-Nut008"  # Fasteners workbench fastener (typed FeaturePython)
  Placement = pos=(80,0,68) rot=(0,1,0;3.14159rad)
  diameter = 1
  invert = false
  matchOuter = false
  offset = 0
  thread = false
  type = 3
FEATURE [Part::MultiFuse] Fusion126  label="Tornillo_Tuerca_Tapeta_sup001"
  Shapes = -> [Nut008,Washer008,Screw008]
FEATURE [Part::FeaturePython] Array065  label="Pack_tornillo_Tuerca_Tapeta_drcha_sup"  # Draft array (typed FeaturePython)
  Angle = 360
  ArrayType = 0
  Axis = (0,0,1)
  Base = -> Fusion126
  Center = (0,0,0)
  Count = 8
  ExpandArray = false
  Fuse = false
  IntervalAxis = (0,0,0)
  IntervalX = (100,0,0)
  IntervalY = (0,24,0)
  IntervalZ = (0,0,100)
  NumberCircles = 3
  NumberPolar = 5
  NumberX = 1
  NumberY = 8
  NumberZ = 1
  Placement = pos=(269,0,1) rot=(0,0,1;0rad)
  PlacementList = 8 placements: arithmetic series from (0,0,0) step (0,24,0) to (0,168,0)
  RadialDistance = 50
  ScaleList = (8) [(1,1,1),(1,1,1),(1,1,1),(1,1,1),(1,1,1),(1,1,1),(1,1,1),(1,1,1)]
  Symmetry = 1
  TangentialDistance = 25
FEATURE [Part::FeaturePython] Washer009  label="M4-Washer009"  # Fasteners workbench fastener (typed FeaturePython)
  Placement = pos=(80,0,76) rot=(0,0,1;0rad)
  diameter = 3
  invert = false
  matchOuter = false
  offset = 0
  type = 6
FEATURE [Part::FeaturePython] Nut009  label="M4-Nut009"  # Fasteners workbench fastener (typed FeaturePython)
  Placement = pos=(80,0,69) rot=(0,1,0;3.14159rad)
  diameter = 1
  invert = false
  matchOuter = false
  offset = 0
  thread = false
  type = 3
FEATURE [Part::FeaturePython] Screw009  label="M4x14-Screw009"  # Fasteners workbench fastener (typed FeaturePython)
  Placement = pos=(80,0,77.2) rot=(0,0,1;0rad)
  diameter = 6
  invert = false
  length = 5
  lengthCustom = 14
  matchOuter = false
  offset = 0
  thread = true
  type = 34
FEATURE [Part::MultiFuse] Fusion127  label="Tornillo_Tuerca_Tapeta_inf001"
  Shapes = -> [Nut009,Washer009,Screw009]
FEATURE [Part::FeaturePython] Array066  label="Pack_tornillo_Tuerca_Tapeta_drcha_inf"  # Draft array (typed FeaturePython)
  Angle = 360
  ArrayType = 0
  Axis = (0,0,1)
  Base = -> Fusion127
  Center = (0,0,0)
  Count = 8
  ExpandArray = false
  Fuse = false
  IntervalAxis = (0,0,0)
  IntervalX = (100,0,0)
  IntervalY = (0,24,0)
  IntervalZ = (0,0,100)
  NumberCircles = 3
  NumberPolar = 5
  NumberX = 1
  NumberY = 8
  NumberZ = 1
  Placement = pos=(429,0,82) rot=(0,1,0;3.14159rad)
  PlacementList = 8 placements: arithmetic series from (0,0,0) step (0,24,0) to (0,168,0)
  RadialDistance = 50
  ScaleList = (8) [(1,1,1),(1,1,1),(1,1,1),(1,1,1),(1,1,1),(1,1,1),(1,1,1),(1,1,1)]
  Symmetry = 1
  TangentialDistance = 25
FEATURE [App::DocumentObjectGroup] Group018  label="Sujeciones"
  Group = -> [Array054,Array055,Array056,Array057,Array058,Array059,Array060,Array061,Array065,Array066]
FEATURE [Part::Box] Box123  label="Cubo_int_izda"
  AttacherType = Attacher::AttachEngine3D
  Height = 105
  Length = 147
  Placement = pos=(-21,-13,0) rot=(0,0,1;0rad)
  Width = 209
FEATURE [Part::Box] Box124  label="Cubo_ext_izda"
  AttacherType = Attacher::AttachEngine3D
  Height = 97
  Length = 150
  Placement = pos=(-24,-16,-4) rot=(0,0,1;0rad)
  Width = 215
FEATURE [Part::Box] Box125  label="Cubo_ext_izda001"
  AttacherType = Attacher::AttachEngine3D
  Height = 97
  Length = 150
  Placement = pos=(243,-16,-4) rot=(0,0,1;0rad)
  Width = 215
FEATURE [Part::Box] Box126  label="Cubo_ext_izda002"
  AttacherType = Attacher::AttachEngine3D
  Height = 97
  Length = 117
  Placement = pos=(126,-16,-4) rot=(0,0,1;0rad)
  Width = 215
FEATURE [Part::Box] Box127  label="Cubo_int_izda001"
  AttacherType = Attacher::AttachEngine3D
  Height = 105
  Length = 147
  Placement = pos=(243,-13,0) rot=(0,0,1;0rad)
  Width = 209
FEATURE [Part::Box] Box128  label="Cubo_int_izda002"
  AttacherType = Attacher::AttachEngine3D
  Height = 105
  Length = 117
  Placement = pos=(126,-13,0) rot=(0,0,1;0rad)
  Width = 209
FEATURE [Part::Cut] Cut001002092  label="Caja_izda"
  Base = -> Box124
  Tool = -> Box123
FEATURE [Part::Cut] Cut001002093  label="Caja_drcha"
  Base = -> Box125
  Tool = -> Box127
FEATURE [Part::Cut] Cut001002094  label="Caja_central"
  Base = -> Box126
  Tool = -> Box128
FEATURE [Part::Box] Box129  label="Solapa_union_caja"
  AttacherType = Attacher::AttachEngine3D
  Height = 93
  Length = 15
  Placement = pos=(114,-13,0) rot=(0,0,1;0rad)
  Width = 7
FEATURE [Part::Box] Box130  label="Tuerca_M4"
  AttacherType = Attacher::AttachEngine3D
  Height = 3.7
  Length = 7.6
  Placement = pos=(117,-7,89) rot=(1,0,0;1.5708rad)
  Width = 7.6
FEATURE [Part::Cylinder] Cylinder045  label="Tornillo_M4"
  Angle = 360
  AttacherType = Attacher::AttachEngine3D
  Height = 21
  Placement = pos=(120.7,-6,92.7) rot=(1,0,0;1.5708rad)
  Radius = 2.6
FEATURE [Part::MultiFuse] Fusion128  label="tornillo+tuerca_M4"
  Placement = pos=(0,0,-19) rot=(0,0,1;0rad)
  Shapes = -> [Box130,Cylinder045]
FEATURE [Part::FeaturePython] Array067  label="Array_Sujecion"  # Draft array (typed FeaturePython)
  Angle = 360
  ArrayType = 0
  Axis = (0,0,1)
  Base = -> Fusion128
  Center = (0,0,0)
  Count = 3
  ExpandArray = false
  Fuse = false
  IntervalAxis = (0,0,0)
  IntervalX = (100,0,0)
  IntervalY = (0,100,0)
  IntervalZ = (0,0,-32)
  NumberCircles = 3
  NumberPolar = 5
  NumberX = 1
  NumberY = 1
  NumberZ = 3
  Placement = pos=(-1,1,0) rot=(0,0,1;0rad)
  PlacementList = 3 placements: arithmetic series from (0,0,-19) step (0,0,-32) to (0,0,-83)
  RadialDistance = 50
  ScaleList = (3) [(1,1,1),(1,1,1),(1,1,1)]
  Symmetry = 1
  TangentialDistance = 25
FEATURE [Part::FeaturePython] Clone020  label="Solapa_union_caja001"  # Draft clone (typed FeaturePython)
  AttacherType = Attacher::AttachEngine3D
  Fuse = false
  Objects = -> [Box129]
  Placement = pos=(240,-13,0) rot=(0,0,1;0rad)
  Scale = (1,1,1)
FEATURE [Part::FeaturePython] Clone021  label="Array_Sujecion001"  # Draft clone (typed FeaturePython)
  AttacherType = Attacher::AttachEngine3D
  Fuse = false
  Objects = -> [Array067]
  Placement = pos=(128,1,0) rot=(0,0,1;0rad)
  Scale = (1,1,1)
FEATURE [Part::FeaturePython] Clone022  label="Solapa_union_caja002"  # Draft clone (typed FeaturePython)
  AttacherType = Attacher::AttachEngine3D
  Fuse = false
  Objects = -> [Box129]
  Placement = pos=(114,179,0) rot=(0,0,1;0rad)
  Scale = (1,1,1)
FEATURE [Part::FeaturePython] Clone023  label="Solapa_union_caja003"  # Draft clone (typed FeaturePython)
  AttacherType = Attacher::AttachEngine3D
  Fuse = false
  Objects = -> [Box129]
  Placement = pos=(240,179,0) rot=(0,0,1;0rad)
  Scale = (1,1,1)
FEATURE [Part::FeaturePython] Clone024  label="Array_Sujecion002"  # Draft clone (typed FeaturePython)
  AttacherType = Attacher::AttachEngine3D
  Fuse = false
  Objects = -> [Array067]
  Placement = pos=(240.47,172,0) rot=(0,0,1;3.14159rad)
  Scale = (1,1,1)
FEATURE [Part::FeaturePython] Clone025  label="Array_Sujecion003"  # Draft clone (typed FeaturePython)
  AttacherType = Attacher::AttachEngine3D
  Fuse = false
  Objects = -> [Array067]
  Placement = pos=(369.47,172,0) rot=(0,0,1;3.14159rad)
  Scale = (1,1,1)
FEATURE [Part::Box] Box131  label="Solapa_base"
  AttacherType = Attacher::AttachEngine3D
  Height = 2
  Length = 12
  Placement = pos=(114,-13,-2) rot=(0,0,1;0rad)
  Width = 209
FEATURE [Part::FeaturePython] Clone026  label="Solapa_base001"  # Draft clone (typed FeaturePython)
  AttacherType = Attacher::AttachEngine3D
  Fuse = false
  Objects = -> [Box131]
  Placement = pos=(114,-13,-2) rot=(0,0,1;0rad)
  Scale = (1,1,1)
FEATURE [Part::Cut] Cut001002095  label="Caja_izda_solapa_inf"
  Base = -> Cut001002092
  Tool = -> Box131
FEATURE [Part::FeaturePython] Clone027  label="Solapa_base002"  # Draft clone (typed FeaturePython)
  AttacherType = Attacher::AttachEngine3D
  Fuse = false
  Objects = -> [Box131]
  Placement = pos=(243,-13,-2) rot=(0,0,1;0rad)
  Scale = (1,1,1)
FEATURE [Part::FeaturePython] Clone028  label="Solapa_base003"  # Draft clone (typed FeaturePython)
  AttacherType = Attacher::AttachEngine3D
  Fuse = false
  Objects = -> [Box131]
  Placement = pos=(243,-13,-2) rot=(0,0,1;0rad)
  Scale = (1,1,1)
FEATURE [Part::Cut] Cut001002096  label="Caja_drcha_solapa_inf"
  Base = -> Cut001002093
  Tool = -> Clone027
FEATURE [Part::Cut] Cut001002097  label="Solapa_agujeros"
  Base = -> Box129
  Tool = -> Array067
FEATURE [Part::Cut] Cut001002098  label="Solapa_agujeros001"
  Base = -> Clone020
  Tool = -> Clone021
FEATURE [Part::Cut] Cut001002099  label="Solapa_agujeros002"
  Base = -> Clone022
  Placement = pos=(0,10,0) rot=(0,0,1;0rad)
  Tool = -> Clone024
FEATURE [Part::Cut] Cut001002100  label="Solapa_agujeros003"
  Base = -> Clone023
  Placement = pos=(0,10,0) rot=(0,0,1;0rad)
  Tool = -> Clone025
FEATURE [Part::MultiFuse] Fusion129  label="Caja_central_soportes"
  Placement = pos=(0,-6,0) rot=(0,0,1;0rad)
  Shapes = -> [Cut001002097,Cut001002098,Cut001002099,Cut001002100,Clone028,Clone026,Cut001002094]
FEATURE [Part::MultiFuse] Fusion130  label="Agujeros_tapa_izda"
  Shapes = -> [Clone024,Array067]
FEATURE [Part::MultiFuse] Fusion131  label="Agujeros_tapa_drcha"
  Shapes = -> [Clone025,Clone021]
FEATURE [Part::Cut] Cut001002101  label="Caja_izda_taladrada"
  Base = -> Cut001002095
  Placement = pos=(0,-6,0) rot=(0,0,1;0rad)
  Tool = -> Fusion130
FEATURE [Part::Cut] Cut001002102  label="Caja_drcha_taladrada"
  Base = -> Cut001002096
  Placement = pos=(0,-6,0) rot=(0,0,1;0rad)
  Tool = -> Fusion131
FEATURE [Part::Box] Box132  label="Cubo009"
  AttacherType = Attacher::AttachEngine3D
  Height = 93
  Length = 10
  Placement = pos=(-21,-19,0) rot=(0,0,1;0rad)
  Width = 7
FEATURE [Part::Box] Box133  label="Tuerca_M005"
  AttacherType = Attacher::AttachEngine3D
  Height = 4.2
  Length = 7.6
  Placement = pos=(117,-7,89) rot=(1,0,0;1.5708rad)
  Width = 7.6
FEATURE [Part::Cylinder] Cylinder046  label="Tornillo_M005"
  Angle = 360
  AttacherType = Attacher::AttachEngine3D
  Height = 35
  Placement = pos=(120.7,18,92.7) rot=(1,0,0;1.5708rad)
  Radius = 2.6
FEATURE [Part::MultiFuse] Fusion132  label="tornillo+tuerca_M005"
  Placement = pos=(-136.8,77,95) rot=(1,0,0;1.5708rad)
  Shapes = -> [Box133,Cylinder046]
FEATURE [Part::Cut] Cut001002103  label="Sujecion_tapa"
  Base = -> Box132
  Tool = -> Fusion132
FEATURE [Part::FeaturePython] Clone029  label="Sujecion_tapa001"  # Draft clone (typed FeaturePython)
  AttacherType = Attacher::AttachEngine3D
  Fuse = false
  Objects = -> [Cut001002103]
  Placement = pos=(0,202,0) rot=(0,0,1;0rad)
  Scale = (1,1,1)
FEATURE [Part::FeaturePython] Clone030  label="Sujecion_tapa002"  # Draft clone (typed FeaturePython)
  AttacherType = Attacher::AttachEngine3D
  Fuse = false
  Objects = -> [Cut001002103]
  Placement = pos=(401,0,0) rot=(0,0,1;0rad)
  Scale = (1,1,1)
FEATURE [Part::FeaturePython] Clone031  label="Sujecion_tapa003"  # Draft clone (typed FeaturePython)
  AttacherType = Attacher::AttachEngine3D
  Fuse = false
  Objects = -> [Cut001002103]
  Placement = pos=(401,202,0) rot=(0,0,1;0rad)
  Scale = (1,1,1)
FEATURE [Part::Cylinder] Cylinder047  label="Hueco_tornillo_M4"
  Angle = 360
  AttacherType = Attacher::AttachEngine3D
  Height = 15
  Placement = pos=(24,24,-11) rot=(0,0,1;0rad)
  Radius = 2.4
FEATURE [Part::FeaturePython] Array068  label="Array_Huecos_M4_Modulo"  # Draft array (typed FeaturePython)
  Angle = 360
  ArrayType = 0
  Axis = (0,0,1)
  Base = -> Cylinder047
  Center = (0,0,0)
  Count = 4
  ExpandArray = false
  Fuse = false
  IntervalAxis = (0,0,0)
  IntervalX = (24,0,0)
  IntervalY = (0,120,0)
  IntervalZ = (0,0,100)
  NumberCircles = 3
  NumberPolar = 5
  NumberX = 2
  NumberY = 2
  NumberZ = 1
  PlacementList = 4 placements: [(24,24,-11),(24,144,-11),(48,24,-11),(48,144,-11)]
  RadialDistance = 50
  ScaleList = (4) [(1,1,1),(1,1,1),(1,1,1),(1,1,1)]
  Symmetry = 1
  TangentialDistance = 25
FEATURE [Part::FeaturePython] Array069  label="Array_Huecos_Bateria"  # Draft array (typed FeaturePython)
  Angle = 360
  ArrayType = 0
  Axis = (0,0,1)
  Base = -> Array068
  Center = (0,0,0)
  Count = 4
  ExpandArray = false
  Fuse = false
  IntervalAxis = (0,0,0)
  IntervalX = (88,0,0)
  IntervalY = (0,100,0)
  IntervalZ = (0,0,100)
  NumberCircles = 3
  NumberPolar = 5
  NumberX = 4
  NumberY = 1
  NumberZ = 1
  Placement = pos=(5,0,0) rot=(0,0,1;0rad)
  PlacementList = 4 placements: arithmetic series from (0,0,0) step (88,0,0) to (264,0,0)
  RadialDistance = 50
  ScaleList = (4) [(1,1,1),(1,1,1),(1,1,1),(1,1,1)]
  Symmetry = 1
  TangentialDistance = 25
FEATURE [Part::MultiFuse] Fusion133  label="Caja_Izda_Sujecion_Tapa"
  Shapes = -> [Cut001002103,Clone029,Cut001002101]
FEATURE [Part::Cut] Cut001002104  label="Caja_Izda_Sujecion_Bateria"
  Base = -> Fusion133
  Tool = -> Array069
FEATURE [Part::Cut] Cut001002105  label="Caja_Central_Sujecion_Bateria"
  Base = -> Fusion129
  Tool = -> Array069
FEATURE [Part::MultiFuse] Fusion134  label="Caja_Drcha_Sujecion_Tapa"
  Shapes = -> [Cut001002102,Clone030,Clone031]
FEATURE [Part::Cut] Cut001002106  label="Caja_Drcha_Sujecion_Bateria"
  Base = -> Fusion134
  Tool = -> Array069
FEATURE [Part::Box] Box134  label="Cubo_int_izda_tapa"
  AttacherType = Attacher::AttachEngine3D
  Height = 7
  Length = 150
  Placement = pos=(-24,-22.1,79) rot=(0,0,1;0rad)
  Width = 215.2
FEATURE [Part::Box] Box135  label="Cubo_ext_izda_tapa"
  AttacherType = Attacher::AttachEngine3D
  Height = 10
  Length = 154
  Placement = pos=(-28,-26.1,79) rot=(0,0,1;0rad)
  Width = 223.2
FEATURE [Part::Cut] Cut001002107  label="Tapa_Izda"
  Base = -> Box135
  Tool = -> Box134
FEATURE [Part::FeaturePython] Clone032  label="tornillo+tuerca_tapa_superior"  # Draft clone (typed FeaturePython)
  AttacherType = Attacher::AttachEngine3D
  Fuse = false
  Objects = -> [Fusion132]
  Placement = pos=(-136.8,77,88) rot=(1,0,0;1.5708rad)
  Scale = (1,1,1)
FEATURE [Part::FeaturePython] Array070  label="Array_tornillo_tapa_superior"  # Draft array (typed FeaturePython)
  Angle = 360
  ArrayType = 0
  Axis = (0,0,1)
  Base = -> Clone032
  Center = (0,0,0)
  Count = 2
  ExpandArray = false
  Fuse = false
  IntervalAxis = (0,0,0)
  IntervalX = (100,0,0)
  IntervalY = (0,202,0)
  IntervalZ = (0,0,100)
  NumberCircles = 3
  NumberPolar = 5
  NumberX = 1
  NumberY = 2
  NumberZ = 1
  PlacementList = 2 placements: [(-136.8,77,88),(-136.8,279,88)]
  RadialDistance = 50
  ScaleList = (2) [(1,1,1),(1,1,1)]
  Symmetry = 1
  TangentialDistance = 25
FEATURE [Part::Cut] Cut001002108  label="Tapa_izda_sup"
  Base = -> Cut001002107
  Tool = -> Array070
FEATURE [Part::Fillet] Fillet002  label="Tapa_izda_sup_chaflan"
  Base = -> Cut001002108
  Edges = 7 edges: [Edge1 r=6,Edge2 r=4,Edge3 r=6,Edge7 r=4,Edge8 r=4,Edge27 r=6,Edge28 r=6]
  Placement = pos=(0,0,7) rot=(0,0,1;0rad)
FEATURE [Part::FeaturePython] Clone033  label="Cubo_ext_drcha_tapa"  # Draft clone (typed FeaturePython)
  AttacherType = Attacher::AttachEngine3D
  Fuse = false
  Objects = -> [Box135]
  Placement = pos=(243,-26.1,79) rot=(0,0,1;0rad)
  Scale = (1,1,1)
FEATURE [Part::FeaturePython] Clone034  label="Cubo_int_drcha_tapa"  # Draft clone (typed FeaturePython)
  AttacherType = Attacher::AttachEngine3D
  Fuse = false
  Objects = -> [Box134]
  Placement = pos=(243,-22.1,79) rot=(0,0,1;0rad)
  Scale = (1,1,1)
FEATURE [Part::Cut] Cut001002109  label="Tapa_drcha"
  Base = -> Clone033
  Tool = -> Clone034
FEATURE [Part::FeaturePython] Clone035  label="Array_tornillo_tapa_superior_drchA"  # Draft clone (typed FeaturePython)
  AttacherType = Attacher::AttachEngine3D
  Fuse = false
  Objects = -> [Array070]
  Placement = pos=(401,0,0) rot=(0,0,1;0rad)
  Scale = (1,1,1)
FEATURE [Part::Cut] Cut001002110  label="Tapa_drcha_sup"
  Base = -> Cut001002109
  Tool = -> Clone035
FEATURE [Part::Fillet] Fillet003  label="Tapa_drcha_sup_chaflan"
  Base = -> Cut001002110
  Edges = 7 edges: [Edge9 r=4,Edge10 r=4,Edge11 r=4,Edge15 r=6,Edge21 r=6,Edge27 r=6,Edge28 r=6]
  Placement = pos=(0,0,7) rot=(0,0,1;0rad)
FEATURE [Part::Box] Box136  label="Cubo_ext_centro_tapa"
  AttacherType = Attacher::AttachEngine3D
  Height = 10
  Length = 117
  Placement = pos=(126,-26.1,79) rot=(0,0,1;0rad)
  Width = 223.2
FEATURE [Part::Box] Box137  label="Cubo_int_centro_tapa"
  AttacherType = Attacher::AttachEngine3D
  Height = 7
  Length = 117
  Placement = pos=(126,-22.1,79) rot=(0,0,1;0rad)
  Width = 215.2
FEATURE [Part::Cut] Cut001002111  label="Tapa_Centro"
  Base = -> Box136
  Placement = pos=(0,0,7) rot=(0,0,1;0rad)
  Tool = -> Box137
FEATURE [Part::FeaturePython] Screw010  label="M10x20-Screw"  # Fasteners workbench fastener (typed FeaturePython)
  Placement = pos=(37,153,91) rot=(0,1,0;3.14159rad)
  diameter = 10
  invert = false
  length = 0
  lengthCustom = 20
  matchOuter = false
  offset = 0
  thread = false
  type = 28
FEATURE [Part::FeaturePython] Clone036  label="M8x16-Screw001"  # Draft clone (typed FeaturePython)
  AttacherType = Attacher::AttachEngine3D
  Fuse = false
  Objects = -> [Screw010]
  Placement = pos=(327,153,91) rot=(0,1,0;3.14159rad)
  Scale = (1,1,1)
FEATURE [Part::FeaturePython] Clone037  label="Sujecion_tapa004"  # Draft clone (typed FeaturePython)
  AttacherType = Attacher::AttachEngine3D
  Fuse = false
  Objects = -> [Clone029]
  Placement = pos=(150,202,0) rot=(0,0,1;0rad)
  Scale = (1,1,1)
FEATURE [Part::FeaturePython] Clone038  label="Sujecion_tapa005"  # Draft clone (typed FeaturePython)
  AttacherType = Attacher::AttachEngine3D
  Fuse = false
  Objects = -> [Clone037]
  Placement = pos=(251,202,0) rot=(0,0,1;0rad)
  Scale = (1,1,1)
FEATURE [Part::FeaturePython] Clone039  label="Sujecion_tapa006"  # Draft clone (typed FeaturePython)
  AttacherType = Attacher::AttachEngine3D
  Fuse = false
  Objects = -> [Clone038]
  Placement = pos=(251,0,0) rot=(0,0,1;0rad)
  Scale = (1,1,1)
FEATURE [Part::FeaturePython] Clone040  label="Sujecion_tapa007"  # Draft clone (typed FeaturePython)
  AttacherType = Attacher::AttachEngine3D
  Fuse = false
  Objects = -> [Clone039]
  Placement = pos=(150,0,0) rot=(0,0,1;0rad)
  Scale = (1,1,1)
FEATURE [Part::MultiFuse] Fusion135  label="Caja_Central_Sujecion_Bateria_y_tapa"
  Shapes = -> [Clone037,Clone038,Clone039,Clone040,Cut001002105]
FEATURE [Part::Cylinder] Cylinder048  label="Agujero_Tapa_central"
  Angle = 360
  AttacherType = Attacher::AttachEngine3D
  Height = 10
  Placement = pos=(133.9,186.3,93) rot=(0,0,1;0rad)
  Radius = 2.6
FEATURE [Part::FeaturePython] Clone041  label="Agujero_Tapa_central001"  # Draft clone (typed FeaturePython)
  AttacherType = Attacher::AttachEngine3D
  Fuse = false
  Objects = -> [Cylinder048]
  Placement = pos=(234.9,186.3,93) rot=(0,0,1;0rad)
  Scale = (1,1,1)
FEATURE [Part::FeaturePython] Clone042  label="Agujero_Tapa_central002"  # Draft clone (typed FeaturePython)
  AttacherType = Attacher::AttachEngine3D
  Fuse = false
  Objects = -> [Clone041]
  Placement = pos=(234.9,-15.7,93) rot=(0,0,1;0rad)
  Scale = (1,1,1)
FEATURE [Part::FeaturePython] Clone043  label="Agujero_Tapa_central003"  # Draft clone (typed FeaturePython)
  AttacherType = Attacher::AttachEngine3D
  Fuse = false
  Objects = -> [Clone042]
  Placement = pos=(133.9,-15.7,93) rot=(0,0,1;0rad)
  Scale = (1,1,1)
FEATURE [Part::MultiFuse] Fusion136  label="Agujeros_Tapa_Central"
  Shapes = -> [Clone043,Clone042,Clone041,Cylinder048]
FEATURE [Part::Cut] Cut001002112  label="Tapa_Central_con_agujeros"
  Base = -> Cut001002111
  Tool = -> Fusion136
FEATURE [Part::Box] Box138  label="Aleta_sujecion_tapa_central"
  AttacherType = Attacher::AttachEngine3D
  Height = 4
  Length = 16
  Placement = pos=(237,-10,89) rot=(0,0,1;0rad)
  Width = 192
FEATURE [Part::FeaturePython] Clone044  label="Aleta_sujecion_tapa_central001"  # Draft clone (typed FeaturePython)
  AttacherType = Attacher::AttachEngine3D
  Fuse = false
  Objects = -> [Box138]
  Placement = pos=(116,-10,89) rot=(0,0,1;0rad)
  Scale = (1,1,1)
FEATURE [Part::MultiFuse] Fusion137  label="Tapa_central_sujeciones"
  Shapes = -> [Cut001002112,Box138,Clone044]
FEATURE [App::DocumentObjectGroup] Group024  label="Caja_Exterior"
  Group = -> [Fusion137,Cut001002104,Fusion135]
FEATURE [Part::Fillet] Fillet  label="Tapa_Central_redondeada"
  Base = -> Fusion137
  Edges = 24 edges: [Edge1 r=1.5,Edge2 r=1.5,Edge3 r=1.5,Edge4 r=1.5,Edge5 r=1.5,Edge6 r=1.5,Edge7 r=1.5,Edge10 r=1.5,Edge11 r=1.5,Edge12 r=1.5,Edge16 r=1.5,Edge23 r=1.5,Edge24 r=1.5,Edge26 r=1.5,Edge37 r=1.5,Edge38 r=1.5,Edge40 r=1.5,Edge41 r=1.5,Edge42 r=1.5,Edge43 r=1.5,Edge45 r=1.5,Edge63 r=4,Edge64 r=4,Edge68 r=1.5]
  Placement = pos=(0,0,20) rot=(0,0,1;0rad)
FEATURE [Mesh::Feature] car3pc68  label="Conector IP68"
  Placement = pos=(448,160,24) rot=(0,1,0;1.5708rad)
FEATURE [Mesh::Feature] car3pc68001  label="Conector IP68-2"
  Placement = pos=(448,160,66) rot=(0,1,0;1.5708rad)
FEATURE [App::DocumentObjectGroup] Group025  label="Conectores"
  Group = -> [car3pc68001,car3pc68]
FEATURE [Part::Cylinder] Cylinder049  label="Agujero_conector"
  Angle = 360
  AttacherType = Attacher::AttachEngine3D
  Height = 10
  Placement = pos=(384,160,24) rot=(0,1,0;1.5708rad)
  Radius = 11.5
FEATURE [Part::FeaturePython] Clone045  label="Agujero_conector001"  # Draft clone (typed FeaturePython)
  AttacherType = Attacher::AttachEngine3D
  Fuse = false
  Objects = -> [Cylinder049]
  Placement = pos=(384,160,63) rot=(0,1,0;1.5708rad)
  Scale = (1,1,1)
FEATURE [Part::MultiFuse] Fusion138  label="Agujero_Conectores"
  Shapes = -> [Cylinder049,Clone045]
FEATURE [Part::Cut] Cut001002113  label="Caja_Drcha_agujeros"
  Base = -> Cut001002106
  Tool = -> Fusion138
FEATURE [Part::Fillet] Fillet005  label="Caja_Izda_Fillet"
  Base = -> Cut001002104
  Edges = 14 edges: [Edge29 r=6,Edge30 r=1,Edge31 r=1,Edge32 r=1,Edge57 r=6,Edge58 r=1,Edge59 r=1,Edge60 r=1,Edge78 r=1,Edge79 r=1,Edge80 r=1,Edge81 r=1,Edge82 r=1,Edge83 r=1]
FEATURE [Part::FeaturePython] Nut010  label="M8-Nut"  # Fasteners workbench fastener (typed FeaturePython)
  Placement = pos=(37,153,97) rot=(0,0,1;0rad)
  diameter = 3
  invert = false
  matchOuter = false
  offset = 0
  thread = false
  type = 8
FEATURE [Part::Cone] Cone  label="Cono"
  Angle = 360
  AttacherType = Attacher::AttachEngine3D
  Height = 13
  Placement = pos=(37,153,104.5) rot=(0,0,1;0rad)
  Radius1 = 6.5
  Radius2 = 5
FEATURE [Part::MultiFuse] Fusion139  label="Borne"
  Shapes = -> [Nut010,Cone]
FEATURE [Part::FeaturePython] Clone046  label="Borne001"  # Draft clone (typed FeaturePython)
  AttacherType = Attacher::AttachEngine3D
  Fuse = false
  Objects = -> [Fusion139]
  Placement = pos=(290,0,0) rot=(0,0,1;0rad)
  Scale = (1,1,1)
FEATURE [App::DocumentObjectGroup] Group028  label="Bornes"
  Group = -> [Fusion139,Clone046]
FEATURE [Part::Cut] Cut001002114  label="Tapa_izda_sup_borne"
  Base = -> Fillet002
  Placement = pos=(0,0,20) rot=(0,0,1;0rad)
  Tool = -> Screw010
FEATURE [Part::Cut] Cut001002115  label="Tapa_drcha_sup_borne"
  Base = -> Fillet003
  Placement = pos=(0,0,20) rot=(0,0,1;0rad)
  Tool = -> Clone036
FEATURE [TechDraw::DrawSVGTemplate] Template
  Height = 297
  Orientation = 1
  Width = 420
FEATURE [TechDraw::DrawViewPart] View001  label="3D view"
  CoarseView = false
  Direction = (-0.577,0.577,0.577)
  Focus = 100
  HardHidden = false
  IsoCount = 0
  IsoHidden = false
  IsoVisible = false
  LockPosition = true
  Perspective = false
  Rotation = 0
  Scale = 0.5
  ScaleType = 0
  SeamHidden = false
  SeamVisible = true
  SmoothHidden = false
  SmoothVisible = true
  Source = -> [Cut001002086]
  X = 342.687
  XDirection = (-0.707,-0.707,0)
  Y = 127.125
FEATURE [TechDraw::DrawSVGTemplate] Template002
  Height = 297
  Orientation = 1
  Width = 420
FEATURE [TechDraw::DrawProjGroupItem] ProjItem006  label="Front002"
  CoarseView = false
  Direction = (0,0,1)
  Focus = 100
  HardHidden = false
  IsoCount = 0
  IsoHidden = false
  IsoVisible = false
  LockPosition = true
  Perspective = false
  Rotation = 0
  RotationVector = (0,1,0)
  ScaleType = 2
  SeamHidden = false
  SeamVisible = true
  SmoothHidden = false
  SmoothVisible = true
  Source = -> [Cut001002045]
  Type = 0
  X = 0
  XDirection = (0,1,0)
  Y = 0
FEATURE [TechDraw::DrawProjGroupItem] ProjItem007  label="Top002"
  CoarseView = false
  Direction = (-1,0,0)
  Focus = 100
  HardHidden = false
  IsoCount = 0
  IsoHidden = false
  IsoVisible = false
  LockPosition = true
  Perspective = false
  Rotation = 0
  RotationVector = (1,0,0)
  ScaleType = 2
  SeamHidden = false
  SeamVisible = true
  SmoothHidden = false
  SmoothVisible = true
  Source = -> [Cut001002045]
  Type = 4
  X = 0
  XDirection = (0,1,0)
  Y = -74.7238
FEATURE [TechDraw::DrawProjGroupItem] ProjItem008  label="FrontTopLeft"
  CoarseView = false
  Direction = (-0.57735,-0.57735,0.57735)
  Focus = 100
  HardHidden = false
  IsoCount = 0
  IsoHidden = false
  IsoVisible = false
  LockPosition = true
  Perspective = false
  Rotation = 0
  RotationVector = (1,0,0)
  ScaleType = 2
  SeamHidden = false
  SeamVisible = true
  SmoothHidden = false
  SmoothVisible = true
  Source = -> [Cut001002045]
  Type = 6
  X = 200.461
  XDirection = (0,0.707107,0.707107)
  Y = -24.7264
FEATURE [TechDraw::DrawProjGroup] ProjGroup002
  Anchor = -> ProjItem006
  AutoDistribute = true
  LockPosition = false
  ProjectionType = 0
  Rotation = 0
  ScaleType = 0
  Source = -> [Cut001002045]
  Views = -> [ProjItem006,ProjItem007,ProjItem008]
  X = 129.744
  Y = 194.78
  spacingX = 15
  spacingY = 15
FEATURE [TechDraw::DrawViewDimension] Dimension025
  Arbitrary = false
  ArbitraryTolerances = false
  EqualTolerance = true
  FormatSpec = %.2f
  FormatSpecOverTolerance = %+.2f
  FormatSpecUnderTolerance = %+.2f
  Inverted = false
  LockPosition = false
  MeasureType = 1
  OverTolerance = 0
  References2D = -> [ProjItem006]
  Rotation = 0
  ScaleType = 0
  TheoreticalExact = false
  Type = 1
  UnderTolerance = 0
  X = 90.1169
  Y = -15.8192
FEATURE [TechDraw::DrawViewDimension] Dimension026
  Arbitrary = false
  ArbitraryTolerances = false
  EqualTolerance = true
  FormatSpec = %.2f
  FormatSpecOverTolerance = %+.2f
  FormatSpecUnderTolerance = %+.2f
  Inverted = false
  LockPosition = false
  MeasureType = 1
  OverTolerance = 0
  References2D = -> [ProjItem006]
  Rotation = 0
  ScaleType = 0
  TheoreticalExact = false
  Type = 1
  UnderTolerance = 0
  X = 46.7987
  Y = -15.223
FEATURE [TechDraw::DrawViewDimension] Dimension027
  Arbitrary = false
  ArbitraryTolerances = false
  EqualTolerance = true
  FormatSpec = %.2f
  FormatSpecOverTolerance = %+.2f
  FormatSpecUnderTolerance = %+.2f
  Inverted = false
  LockPosition = false
  MeasureType = 1
  OverTolerance = 0
  References2D = -> [ProjItem006]
  Rotation = 0
  ScaleType = 0
  TheoreticalExact = false
  Type = 2
  UnderTolerance = 0
  X = -109.591
  Y = 0.23376
FEATURE [TechDraw::DrawViewDimension] Dimension028
  Arbitrary = false
  ArbitraryTolerances = false
  EqualTolerance = true
  FormatSpec = %.2f
  FormatSpecOverTolerance = %+.2f
  FormatSpecUnderTolerance = %+.2f
  Inverted = false
  LockPosition = false
  MeasureType = 1
  OverTolerance = 0
  References2D = -> [ProjItem007]
  Rotation = 0
  ScaleType = 0
  TheoreticalExact = false
  Type = 2
  UnderTolerance = 0
  X = 103.222
  Y = 9.81605
FEATURE [TechDraw::DrawViewDimension] Dimension029
  Arbitrary = false
  ArbitraryTolerances = false
  EqualTolerance = true
  FormatSpec = %.2f
  FormatSpecOverTolerance = %+.2f
  FormatSpecUnderTolerance = %+.2f
  Inverted = false
  LockPosition = false
  MeasureType = 1
  OverTolerance = 0
  References2D = -> [ProjItem007]
  Rotation = 0
  ScaleType = 0
  TheoreticalExact = false
  Type = 1
  UnderTolerance = 0
  X = 1.00984
  Y = -9.42027
FEATURE [TechDraw::DrawViewDimension] Dimension030
  Arbitrary = false
  ArbitraryTolerances = false
  EqualTolerance = true
  FormatSpec = ⌀%.2f
  FormatSpecOverTolerance = %+.2f
  FormatSpecUnderTolerance = %+.2f
  Inverted = false
  LockPosition = false
  MeasureType = 1
  OverTolerance = 0
  References2D = -> [ProjItem006]
  Rotation = 0
  ScaleType = 0
  TheoreticalExact = false
  Type = 5
  UnderTolerance = 0
  X = -1.1688
  Y = 22.4409
FEATURE [TechDraw::DrawSVGTemplate] Template003
  Height = 297
  Orientation = 1
  Width = 420
FEATURE [TechDraw::DrawProjGroupItem] ProjItem009  label="Front003"
  CoarseView = false
  Direction = (1,0,0)
  Focus = 100
  HardHidden = true
  IsoCount = 0
  IsoHidden = false
  IsoVisible = false
  LockPosition = true
  Perspective = false
  Rotation = 0
  RotationVector = (0,1,0)
  ScaleType = 2
  SeamHidden = false
  SeamVisible = true
  SmoothHidden = false
  SmoothVisible = true
  Source = -> [Fusion116]
  Type = 0
  X = 0
  XDirection = (0,1,0)
  Y = 0
FEATURE [TechDraw::DrawProjGroupItem] ProjItem011  label="Top003"
  CoarseView = false
  Direction = (0,0,1)
  Focus = 100
  HardHidden = true
  IsoCount = 0
  IsoHidden = false
  IsoVisible = false
  LockPosition = true
  Perspective = false
  Rotation = 0
  RotationVector = (1,0,0)
  ScaleType = 2
  SeamHidden = false
  SeamVisible = true
  SmoothHidden = false
  SmoothVisible = true
  Source = -> [Fusion116]
  Type = 4
  X = 0
  XDirection = (0,1,0)
  Y = -101.123
FEATURE [TechDraw::DrawProjGroup] ProjGroup003
  Anchor = -> ProjItem009
  AutoDistribute = true
  LockPosition = true
  ProjectionType = 0
  Rotation = 0
  ScaleType = 0
  Source = -> [Fusion116]
  Views = -> [ProjItem009,ProjItem011]
  X = 134.288
  Y = 214.382
  spacingX = 15
  spacingY = 15
FEATURE [TechDraw::DrawViewPart] View003
  CoarseView = false
  Direction = (0.577,-0.577,0.577)
  Focus = 100
  HardHidden = false
  IsoCount = 0
  IsoHidden = false
  IsoVisible = false
  LockPosition = false
  Perspective = false
  Rotation = 0
  Scale = 0.5
  ScaleType = 0
  SeamHidden = false
  SeamVisible = true
  SmoothHidden = false
  SmoothVisible = true
  Source = -> [Fusion116]
  X = 338.714
  XDirection = (0.707,0.707,0)
  Y = 114.486
FEATURE [TechDraw::DrawViewDimension] Dimension031
  Arbitrary = false
  ArbitraryTolerances = false
  EqualTolerance = true
  FormatSpec = %.2f
  FormatSpecOverTolerance = %+.2f
  FormatSpecUnderTolerance = %+.2f
  Inverted = false
  LockPosition = false
  MeasureType = 1
  OverTolerance = 0
  References2D = -> [ProjItem009]
  Rotation = 0
  ScaleType = 0
  TheoreticalExact = false
  Type = 2
  UnderTolerance = 0
  X = -107.682
  Y = 51.8212
FEATURE [TechDraw::DrawViewDimension] Dimension032
  Arbitrary = false
  ArbitraryTolerances = false
  EqualTolerance = true
  FormatSpec = %.2f
  FormatSpecOverTolerance = %+.2f
  FormatSpecUnderTolerance = %+.2f
  Inverted = false
  LockPosition = false
  MeasureType = 1
  OverTolerance = 0
  References2D = -> [ProjItem009]
  Rotation = 0
  ScaleType = 0
  TheoreticalExact = false
  Type = 2
  UnderTolerance = 0
  X = 104.57
  Y = 36.8583
FEATURE [TechDraw::DrawViewDimension] Dimension033
  Arbitrary = false
  ArbitraryTolerances = false
  EqualTolerance = true
  FormatSpec = %.2f
  FormatSpecOverTolerance = %+.2f
  FormatSpecUnderTolerance = %+.2f
  Inverted = false
  LockPosition = false
  MeasureType = 1
  OverTolerance = 0
  References2D = -> [ProjItem009]
  Rotation = 0
  ScaleType = 0
  TheoreticalExact = false
  Type = 2
  UnderTolerance = 0
  X = 104.122
  Y = -18.1297
FEATURE [TechDraw::DrawViewDimension] Dimension034
  Arbitrary = false
  ArbitraryTolerances = false
  EqualTolerance = true
  FormatSpec = %.2f
  FormatSpecOverTolerance = %+.2f
  FormatSpecUnderTolerance = %+.2f
  Inverted = false
  LockPosition = false
  MeasureType = 1
  OverTolerance = 0
  References2D = -> [ProjItem009]
  Rotation = 0
  ScaleType = 0
  TheoreticalExact = false
  Type = 2
  UnderTolerance = 0
  X = -107.312
  Y = -47.8141
FEATURE [TechDraw::DrawViewDimension] Dimension035
  Arbitrary = false
  ArbitraryTolerances = false
  EqualTolerance = true
  FormatSpec = %.2f
  FormatSpecOverTolerance = %+.2f
  FormatSpecUnderTolerance = %+.2f
  Inverted = false
  LockPosition = false
  MeasureType = 1
  OverTolerance = 0
  References2D = -> [ProjItem009]
  Rotation = 0
  ScaleType = 0
  TheoreticalExact = false
  Type = 2
  UnderTolerance = 0
  X = 46.4861
  Y = -3.69007
FEATURE [TechDraw::DrawViewDimension] Dimension036
  Arbitrary = false
  ArbitraryTolerances = false
  EqualTolerance = true
  FormatSpec = %.2f
  FormatSpecOverTolerance = %+.2f
  FormatSpecUnderTolerance = %+.2f
  Inverted = false
  LockPosition = false
  MeasureType = 1
  OverTolerance = 0
  References2D = -> [ProjItem009]
  Rotation = 0
  ScaleType = 0
  TheoreticalExact = false
  Type = 1
  UnderTolerance = 0
  X = 0.426785
  Y = 19.4051
FEATURE [TechDraw::DrawViewDimension] Dimension037
  Arbitrary = false
  ArbitraryTolerances = false
  EqualTolerance = true
  FormatSpec = %.2f
  FormatSpecOverTolerance = %+.2f
  FormatSpecUnderTolerance = %+.2f
  Inverted = false
  LockPosition = false
  MeasureType = 1
  OverTolerance = 0
  References2D = -> [ProjItem009]
  Rotation = 0
  ScaleType = 0
  TheoreticalExact = false
  Type = 1
  UnderTolerance = 0
  X = -108.462
  Y = 19.7135
FEATURE [TechDraw::DrawViewDimension] Dimension038
  Arbitrary = false
  ArbitraryTolerances = false
  EqualTolerance = true
  FormatSpec = ⌀%.2f
  FormatSpecOverTolerance = %+.2f
  FormatSpecUnderTolerance = %+.2f
  Inverted = false
  LockPosition = false
  MeasureType = 1
  OverTolerance = 0
  References2D = -> [ProjItem011]
  Rotation = 0
  ScaleType = 0
  TheoreticalExact = false
  Type = 5
  UnderTolerance = 0
  X = 109.736
  Y = -2.69291
FEATURE [TechDraw::DrawViewDimension] Dimension039
  Arbitrary = false
  ArbitraryTolerances = false
  EqualTolerance = true
  FormatSpec = %.2f
  FormatSpecOverTolerance = %+.2f
  FormatSpecUnderTolerance = %+.2f
  Inverted = false
  LockPosition = false
  MeasureType = 1
  OverTolerance = 0
  References2D = -> [ProjItem011]
  Rotation = 0
  ScaleType = 0
  TheoreticalExact = false
  Type = 1
  UnderTolerance = 0
  X = -90
  Y = -17.8984
FEATURE [TechDraw::DrawViewDimension] Dimension040
  Arbitrary = false
  ArbitraryTolerances = false
  EqualTolerance = true
  FormatSpec = %.2f
  FormatSpecOverTolerance = %+.2f
  FormatSpecUnderTolerance = %+.2f
  Inverted = false
  LockPosition = false
  MeasureType = 1
  OverTolerance = 0
  References2D = -> [ProjItem011]
  Rotation = 0
  ScaleType = 0
  TheoreticalExact = false
  Type = 1
  UnderTolerance = 0
  X = -49.3465
  Y = -17.8913
FEATURE [TechDraw::DrawViewDimension] Dimension043
  Arbitrary = false
  ArbitraryTolerances = false
  EqualTolerance = true
  FormatSpec = %.2f
  FormatSpecOverTolerance = %+.2f
  FormatSpecUnderTolerance = %+.2f
  Inverted = false
  LockPosition = false
  MeasureType = 1
  OverTolerance = 0
  References2D = -> [ProjItem011]
  Rotation = 0
  ScaleType = 0
  TheoreticalExact = false
  Type = 2
  UnderTolerance = 0
  X = -108.452
  Y = -2.03235
FEATURE [TechDraw::DrawViewSection] SectionView  label="Section A - A"
  BaseView = -> ProjItem009
  CoarseView = false
  CutSurfaceDisplay = 2
  Direction = (0,-1,0)
  FileGeomPattern = <path>
  FileHatchPattern = <path>
  Focus = 100
  FuseBeforeCut = false
  HardHidden = false
  HatchScale = 1
  IsoCount = 0
  IsoHidden = false
  IsoVisible = false
  LockPosition = true
  NameGeomPattern = Diamond
  Perspective = false
  Rotation = 0
  ScaleType = 0
  SeamHidden = false
  SeamVisible = true
  SectionDirection = 0
  SectionNormal = (0,-1,0)
  SectionOrigin = (-5.5,119,43.1)
  SectionSymbol = A
  SmoothHidden = false
  SmoothVisible = true
  Source = -> [Fusion116]
  X = 325.12
  XDirection = (1,0,0)
  Y = 211.927
FEATURE [TechDraw::DrawViewDimension] Dimension046
  Arbitrary = false
  ArbitraryTolerances = false
  EqualTolerance = true
  FormatSpec = %.2f
  FormatSpecOverTolerance = %+.2f
  FormatSpecUnderTolerance = %+.2f
  Inverted = false
  LockPosition = false
  MeasureType = 1
  OverTolerance = 0
  References2D = -> [SectionView]
  Rotation = 0
  ScaleType = 0
  TheoreticalExact = false
  Type = 1
  UnderTolerance = 0
  X = -23.4842
  Y = 53.7766
FEATURE [TechDraw::DrawViewDimension] Dimension047
  Arbitrary = false
  ArbitraryTolerances = false
  EqualTolerance = true
  FormatSpec = %.2f
  FormatSpecOverTolerance = %+.2f
  FormatSpecUnderTolerance = %+.2f
  Inverted = false
  LockPosition = false
  MeasureType = 1
  OverTolerance = 0
  References2D = -> [SectionView]
  Rotation = 0
  ScaleType = 0
  TheoreticalExact = false
  Type = 2
  UnderTolerance = 0
  X = 16.7274
  Y = 43.3681
FEATURE [TechDraw::DrawViewDimension] Dimension048
  Arbitrary = false
  ArbitraryTolerances = false
  EqualTolerance = true
  FormatSpec = %.2f
  FormatSpecOverTolerance = %+.2f
  FormatSpecUnderTolerance = %+.2f
  Inverted = false
  LockPosition = false
  MeasureType = 1
  OverTolerance = 0
  References2D = -> [SectionView]
  Rotation = 0
  ScaleType = 0
  TheoreticalExact = false
  Type = 2
  UnderTolerance = 0
  X = 16.718
  Y = -40.9484
FEATURE [TechDraw::DrawViewDimension] Dimension049
  Arbitrary = false
  ArbitraryTolerances = false
  EqualTolerance = true
  FormatSpec = %.2f
  FormatSpecOverTolerance = %+.2f
  FormatSpecUnderTolerance = %+.2f
  Inverted = false
  LockPosition = false
  MeasureType = 1
  OverTolerance = 0
  References2D = -> [SectionView]
  Rotation = 0
  ScaleType = 0
  TheoreticalExact = false
  Type = 2
  UnderTolerance = 0
  X = 16.7212
  Y = 5.88385
FEATURE [TechDraw::DrawViewDimension] Dimension051
  Arbitrary = false
  ArbitraryTolerances = false
  EqualTolerance = true
  FormatSpec = %.2f
  FormatSpecOverTolerance = %+.2f
  FormatSpecUnderTolerance = %+.2f
  Inverted = false
  LockPosition = false
  MeasureType = 1
  OverTolerance = 0
  References2D = -> [SectionView]
  Rotation = 0
  ScaleType = 0
  TheoreticalExact = false
  Type = 1
  UnderTolerance = 0
  X = 13.4893
  Y = -13.4296
FEATURE [TechDraw::DrawViewDimension] Dimension052
  Arbitrary = false
  ArbitraryTolerances = false
  EqualTolerance = true
  FormatSpec = %.2f
  FormatSpecOverTolerance = %+.2f
  FormatSpecUnderTolerance = %+.2f
  Inverted = false
  LockPosition = false
  MeasureType = 1
  OverTolerance = 0
  References2D = -> [SectionView]
  Rotation = 0
  ScaleType = 0
  TheoreticalExact = false
  Type = 1
  UnderTolerance = 0
  X = -11.6003
  Y = -45.3108
FEATURE [TechDraw::DrawViewDimension] Dimension053
  Arbitrary = false
  ArbitraryTolerances = false
  EqualTolerance = true
  FormatSpec = %.2f
  FormatSpecOverTolerance = %+.2f
  FormatSpecUnderTolerance = %+.2f
  Inverted = false
  LockPosition = false
  MeasureType = 1
  OverTolerance = 0
  References2D = -> [SectionView]
  Rotation = 0
  ScaleType = 0
  TheoreticalExact = false
  Type = 2
  UnderTolerance = 0
  X = -20.0202
  Y = -35.5479
FEATURE [TechDraw::DrawViewAnnotation] Annotation
  Font = osifont
  LineSpace = 80
  LockPosition = false
  MaxWidth = -1
  Rotation = 0
  ScaleType = 0
  Text = Secci\xf3n A-A
  TextSize = 5
  TextStyle = 0
  X = 329.587
  Y = 266.894
FEATURE [TechDraw::DrawSVGTemplate] Template004
  Height = 297
  Orientation = 1
  Width = 420
FEATURE [TechDraw::DrawProjGroupItem] ProjItem012  label="Front004"
  CoarseView = false
  Direction = (-1,0,0)
  Focus = 100
  HardHidden = true
  IsoCount = 0
  IsoHidden = false
  IsoVisible = false
  LockPosition = true
  Perspective = false
  Rotation = 0
  RotationVector = (0,-1,0)
  ScaleType = 2
  SeamHidden = false
  SeamVisible = true
  SmoothHidden = false
  SmoothVisible = true
  Source = -> [Fusion125]
  Type = 0
  X = 0
  XDirection = (0,-1,0)
  Y = 0
FEATURE [TechDraw::DrawProjGroupItem] ProjItem014  label="Top004"
  CoarseView = false
  Direction = (0,0,1)
  Focus = 100
  HardHidden = true
  IsoCount = 0
  IsoHidden = false
  IsoVisible = false
  LockPosition = true
  Perspective = false
  Rotation = 0
  RotationVector = (1,0,0)
  ScaleType = 2
  SeamHidden = false
  SeamVisible = true
  SmoothHidden = false
  SmoothVisible = true
  Source = -> [Fusion125]
  Type = 4
  X = 0
  XDirection = (0,-1,0)
  Y = -111.58
FEATURE [TechDraw::DrawProjGroup] ProjGroup004
  Anchor = -> ProjItem012
  AutoDistribute = true
  LockPosition = true
  ProjectionType = 0
  Rotation = 0
  ScaleType = 0
  Source = -> [Fusion125]
  Views = -> [ProjItem012,ProjItem014]
  X = 148.576
  Y = 216.555
  spacingX = 15
  spacingY = 15
FEATURE [TechDraw::DrawViewDimension] Dimension055
  Arbitrary = false
  ArbitraryTolerances = false
  EqualTolerance = true
  FormatSpec = %.2f
  FormatSpecOverTolerance = %+.2f
  FormatSpecUnderTolerance = %+.2f
  Inverted = false
  LockPosition = false
  MeasureType = 1
  OverTolerance = 0
  References2D = -> [ProjItem012]
  Rotation = 0
  ScaleType = 0
  TheoreticalExact = false
  Type = 1
  UnderTolerance = 0
  X = 86.2922
  Y = -53.2684
FEATURE [TechDraw::DrawViewDimension] Dimension056
  Arbitrary = false
  ArbitraryTolerances = false
  EqualTolerance = true
  FormatSpec = %.2f
  FormatSpecOverTolerance = %+.2f
  FormatSpecUnderTolerance = %+.2f
  Inverted = false
  LockPosition = false
  MeasureType = 1
  OverTolerance = 0
  References2D = -> [ProjItem012]
  Rotation = 0
  ScaleType = 0
  TheoreticalExact = false
  Type = 1
  UnderTolerance = 0
  X = 11.7052
  Y = -52.2944
FEATURE [TechDraw::DrawViewDimension] Dimension059
  Arbitrary = false
  ArbitraryTolerances = false
  EqualTolerance = true
  FormatSpec = %.2f
  FormatSpecOverTolerance = %+.2f
  FormatSpecUnderTolerance = %+.2f
  Inverted = false
  LockPosition = false
  MeasureType = 1
  OverTolerance = 0
  References2D = -> [ProjItem012]
  Rotation = 0
  ScaleType = 0
  TheoreticalExact = false
  Type = 2
  UnderTolerance = 0
  X = 102.412
  Y = 37.7481
FEATURE [TechDraw::DrawViewDimension] Dimension062
  Arbitrary = false
  ArbitraryTolerances = false
  EqualTolerance = true
  FormatSpec = %.2f
  FormatSpecOverTolerance = %+.2f
  FormatSpecUnderTolerance = %+.2f
  Inverted = false
  LockPosition = false
  MeasureType = 1
  OverTolerance = 0
  References2D = -> [ProjItem012]
  Rotation = 0
  ScaleType = 0
  TheoreticalExact = false
  Type = 2
  UnderTolerance = 0
  X = 102.084
  Y = -48.426
FEATURE [TechDraw::DrawViewDimension] Dimension063
  Arbitrary = false
  ArbitraryTolerances = false
  EqualTolerance = true
  FormatSpec = %.2f
  FormatSpecOverTolerance = %+.2f
  FormatSpecUnderTolerance = %+.2f
  Inverted = false
  LockPosition = false
  MeasureType = 1
  OverTolerance = 0
  References2D = -> [ProjItem014]
  Rotation = 0
  ScaleType = 0
  TheoreticalExact = false
  Type = 1
  UnderTolerance = 0
  X = 0.201968
  Y = -20.6748
FEATURE [TechDraw::DrawViewDimension] Dimension064
  Arbitrary = false
  ArbitraryTolerances = false
  EqualTolerance = true
  FormatSpec = %.2f
  FormatSpecOverTolerance = %+.2f
  FormatSpecUnderTolerance = %+.2f
  Inverted = false
  LockPosition = false
  MeasureType = 1
  OverTolerance = 0
  References2D = -> [ProjItem014]
  Rotation = 0
  ScaleType = 0
  TheoreticalExact = false
  Type = 1
  UnderTolerance = 0
  X = 70.4091
  Y = -15.9551
FEATURE [TechDraw::DrawViewDimension] Dimension065
  Arbitrary = false
  ArbitraryTolerances = false
  EqualTolerance = true
  FormatSpec = %.2f
  FormatSpecOverTolerance = %+.2f
  FormatSpecUnderTolerance = %+.2f
  Inverted = false
  LockPosition = false
  MeasureType = 1
  OverTolerance = 0
  References2D = -> [ProjItem014]
  Rotation = 0
  ScaleType = 0
  TheoreticalExact = false
  Type = 1
  UnderTolerance = 0
  X = 24
  Y = -15.0728
FEATURE [TechDraw::DrawViewDimension] Dimension066
  Arbitrary = false
  ArbitraryTolerances = false
  EqualTolerance = true
  FormatSpec = ⌀%.2f
  FormatSpecOverTolerance = %+.2f
  FormatSpecUnderTolerance = %+.2f
  Inverted = false
  LockPosition = false
  MeasureType = 1
  OverTolerance = 0
  References2D = -> [ProjItem014]
  Rotation = 0
  ScaleType = 0
  TheoreticalExact = false
  Type = 5
  UnderTolerance = 0
  X = -23.4283
  Y = 0.605905
FEATURE [TechDraw::DrawViewSection] SectionView001  label="Section A - A001"
  BaseView = -> ProjItem012
  CoarseView = false
  CutSurfaceDisplay = 2
  Direction = (0,1,0)
  FileGeomPattern = <path>
  FileHatchPattern = <path>
  Focus = 100
  FuseBeforeCut = false
  HardHidden = true
  HatchScale = 1
  IsoCount = 0
  IsoHidden = false
  IsoVisible = false
  LockPosition = false
  NameGeomPattern = Diamond
  Perspective = false
  Rotation = 0
  ScaleType = 0
  SeamHidden = false
  SeamVisible = true
  SectionDirection = 0
  SectionNormal = (0,1,0)
  SectionOrigin = (354,47,43.1)
  SectionSymbol = A
  SmoothHidden = false
  SmoothVisible = true
  Source = -> [Fusion125]
  X = 318.11
  XDirection = (-1,0,0)
  Y = 216.601
FEATURE [TechDraw::DrawViewDimension] Dimension058
  Arbitrary = false
  ArbitraryTolerances = false
  EqualTolerance = true
  FormatSpec = %.2f
  FormatSpecOverTolerance = %+.2f
  FormatSpecUnderTolerance = %+.2f
  Inverted = false
  LockPosition = false
  MeasureType = 1
  OverTolerance = 0
  References2D = -> [SectionView001]
  Rotation = 0
  ScaleType = 0
  TheoreticalExact = false
  Type = 2
  UnderTolerance = 0
  X = 35.7735
  Y = 18.5222
FEATURE [TechDraw::DrawViewDimension] Dimension061
  Arbitrary = false
  ArbitraryTolerances = false
  EqualTolerance = true
  FormatSpec = %.2f
  FormatSpecOverTolerance = %+.2f
  FormatSpecUnderTolerance = %+.2f
  Inverted = false
  LockPosition = false
  MeasureType = 1
  OverTolerance = 0
  References2D = -> [SectionView001]
  Rotation = 0
  ScaleType = 0
  TheoreticalExact = false
  Type = 2
  UnderTolerance = 0
  X = 25.2894
  Y = -40.8716
FEATURE [TechDraw::DrawViewDimension] Dimension057
  Arbitrary = false
  ArbitraryTolerances = false
  EqualTolerance = true
  FormatSpec = %.2f
  FormatSpecOverTolerance = %+.2f
  FormatSpecUnderTolerance = %+.2f
  Inverted = false
  LockPosition = false
  MeasureType = 1
  OverTolerance = 0
  References2D = -> [SectionView001]
  Rotation = 0
  ScaleType = 0
  TheoreticalExact = false
  Type = 2
  UnderTolerance = 0
  X = 26.523
  Y = 18.8291
FEATURE [TechDraw::DrawViewDimension] Dimension067
  Arbitrary = false
  ArbitraryTolerances = false
  EqualTolerance = true
  FormatSpec = %.2f
  FormatSpecOverTolerance = %+.2f
  FormatSpecUnderTolerance = %+.2f
  Inverted = false
  LockPosition = false
  MeasureType = 1
  OverTolerance = 0
  References2D = -> [SectionView001]
  Rotation = 0
  ScaleType = 0
  TheoreticalExact = false
  Type = 2
  UnderTolerance = 0
  X = -20.6705
  Y = -5.29409
FEATURE [TechDraw::DrawViewDimension] Dimension068
  Arbitrary = false
  ArbitraryTolerances = false
  EqualTolerance = true
  FormatSpec = %.2f
  FormatSpecOverTolerance = %+.2f
  FormatSpecUnderTolerance = %+.2f
  Inverted = false
  LockPosition = false
  MeasureType = 1
  OverTolerance = 0
  References2D = -> [ProjItem014]
  Rotation = 0
  ScaleType = 0
  TheoreticalExact = false
  Type = 2
  UnderTolerance = 0
  X = 105.453
  Y = 21.6391
FEATURE [TechDraw::DrawViewDimension] Dimension069
  Arbitrary = false
  ArbitraryTolerances = false
  EqualTolerance = true
  FormatSpec = %.2f
  FormatSpecOverTolerance = %+.2f
  FormatSpecUnderTolerance = %+.2f
  Inverted = false
  LockPosition = false
  MeasureType = 1
  OverTolerance = 0
  References2D = -> [ProjItem014]
  Rotation = 0
  ScaleType = 0
  TheoreticalExact = false
  Type = 1
  UnderTolerance = 0
  X = -85.1897
  Y = 24.3724
FEATURE [TechDraw::DrawViewDimension] Dimension070
  Arbitrary = false
  ArbitraryTolerances = false
  EqualTolerance = true
  FormatSpec = %.2f
  FormatSpecOverTolerance = %+.2f
  FormatSpecUnderTolerance = %+.2f
  Inverted = false
  LockPosition = false
  MeasureType = 1
  OverTolerance = 0
  References2D = -> [SectionView001]
  Rotation = 0
  ScaleType = 0
  TheoreticalExact = false
  Type = 2
  UnderTolerance = 0
  X = -20.7781
  Y = -45.8284
FEATURE [TechDraw::DrawViewDimension] Dimension071
  Arbitrary = false
  ArbitraryTolerances = false
  EqualTolerance = true
  FormatSpec = %.2f
  FormatSpecOverTolerance = %+.2f
  FormatSpecUnderTolerance = %+.2f
  Inverted = false
  LockPosition = false
  MeasureType = 1
  OverTolerance = 0
  References2D = -> [ProjItem012]
  Rotation = 0
  ScaleType = 0
  TheoreticalExact = false
  Type = 1
  UnderTolerance = 0
  X = 0.336614
  Y = 14.9311
FEATURE [TechDraw::DrawViewDimension] Dimension072
  Arbitrary = false
  ArbitraryTolerances = false
  EqualTolerance = true
  FormatSpec = %.2f
  FormatSpecOverTolerance = %+.2f
  FormatSpecUnderTolerance = %+.2f
  Inverted = false
  LockPosition = false
  MeasureType = 1
  OverTolerance = 0
  References2D = -> [ProjItem012]
  Rotation = 0
  ScaleType = 0
  TheoreticalExact = false
  Type = 1
  UnderTolerance = 0
  X = -105.821
  Y = 14.967
FEATURE [TechDraw::DrawViewDimension] Dimension073
  Arbitrary = false
  ArbitraryTolerances = false
  EqualTolerance = true
  FormatSpec = %.2f
  FormatSpecOverTolerance = %+.2f
  FormatSpecUnderTolerance = %+.2f
  Inverted = false
  LockPosition = false
  MeasureType = 1
  OverTolerance = 0
  References2D = -> [ProjItem012]
  Rotation = 0
  ScaleType = 0
  TheoreticalExact = false
  Type = 1
  UnderTolerance = 0
  X = -47.0237
  Y = -10.1445
FEATURE [TechDraw::DrawViewDimension] Dimension075
  Arbitrary = false
  ArbitraryTolerances = false
  EqualTolerance = true
  FormatSpec = %.2f
  FormatSpecOverTolerance = %+.2f
  FormatSpecUnderTolerance = %+.2f
  Inverted = false
  LockPosition = false
  MeasureType = 1
  OverTolerance = 0
  References2D = -> [ProjItem014]
  Rotation = 0
  ScaleType = 0
  TheoreticalExact = false
  Type = 1
  UnderTolerance = 0
  X = 2.41356
  Y = 24.431
FEATURE [TechDraw::DrawViewDimension] Dimension076
  Arbitrary = false
  ArbitraryTolerances = false
  EqualTolerance = true
  FormatSpec = %.2f
  FormatSpecOverTolerance = %+.2f
  FormatSpecUnderTolerance = %+.2f
  Inverted = false
  LockPosition = false
  MeasureType = 1
  OverTolerance = 0
  References2D = -> [ProjItem012]
  Rotation = 0
  ScaleType = 0
  TheoreticalExact = false
  Type = 2
  UnderTolerance = 0
  X = -108.261
  Y = -46.8427
FEATURE [TechDraw::DrawViewDimension] Dimension077
  Arbitrary = false
  ArbitraryTolerances = false
  EqualTolerance = true
  FormatSpec = %.2f
  FormatSpecOverTolerance = %+.2f
  FormatSpecUnderTolerance = %+.2f
  Inverted = false
  LockPosition = false
  MeasureType = 1
  OverTolerance = 0
  References2D = -> [ProjItem012]
  Rotation = 0
  ScaleType = 0
  TheoreticalExact = false
  Type = 2
  UnderTolerance = 0
  X = 101.947
  Y = -2.20567
FEATURE [TechDraw::DrawViewDimension] Dimension078
  Arbitrary = false
  ArbitraryTolerances = false
  EqualTolerance = true
  FormatSpec = %.2f
  FormatSpecOverTolerance = %+.2f
  FormatSpecUnderTolerance = %+.2f
  Inverted = false
  LockPosition = false
  MeasureType = 1
  OverTolerance = 0
  References2D = -> [SectionView001]
  Rotation = 0
  ScaleType = 0
  TheoreticalExact = false
  Type = 2
  UnderTolerance = 0
  X = 16.9279
  Y = -4.9226
FEATURE [TechDraw::DrawViewPart] View004
  CoarseView = false
  Direction = (-0.577,0.577,0.577)
  Focus = 100
  HardHidden = false
  IsoCount = 0
  IsoHidden = false
  IsoVisible = false
  LockPosition = false
  Perspective = false
  Rotation = 0
  Scale = 0.5
  ScaleType = 0
  SeamHidden = false
  SeamVisible = true
  SmoothHidden = false
  SmoothVisible = true
  Source = -> [Fusion125]
  X = 330.11
  XDirection = (-0.707,-0.707,0)
  Y = 119.827
FEATURE [TechDraw::DrawViewAnnotation] Annotation001
  Font = osifont
  LineSpace = 80
  LockPosition = false
  MaxWidth = -1
  Rotation = 0
  ScaleType = 0
  Text = Secci\xf3n A-A
  TextSize = 5
  TextStyle = 0
  X = 328.66
  Y = 265.415
FEATURE [TechDraw::DrawViewDimension] Dimension079
  Arbitrary = false
  ArbitraryTolerances = false
  EqualTolerance = true
  FormatSpec = %.2f
  FormatSpecOverTolerance = %+.2f
  FormatSpecUnderTolerance = %+.2f
  Inverted = false
  LockPosition = false
  MeasureType = 1
  OverTolerance = 0
  References2D = -> [ProjItem012]
  Rotation = 0
  ScaleType = 0
  TheoreticalExact = false
  Type = 1
  UnderTolerance = 0
  X = -34.2854
  Y = -50.4299
FEATURE [TechDraw::DrawSVGTemplate] Template005
  Height = 297
  Orientation = 1
  Width = 420
FEATURE [TechDraw::DrawSVGTemplate] Template006
  Height = 297
  Orientation = 1
  Width = 420
FEATURE [TechDraw::DrawProjGroupItem] ProjItem024  label="Front006"
  CoarseView = false
  Direction = (1,0,0)
  Focus = 100
  HardHidden = true
  IsoCount = 0
  IsoHidden = false
  IsoVisible = false
  LockPosition = true
  Perspective = false
  Rotation = 0
  RotationVector = (0,1,0)
  Scale = 0.75
  ScaleType = 2
  SeamHidden = false
  SeamVisible = true
  SmoothHidden = false
  SmoothVisible = true
  Source = -> [Fillet005]
  Type = 0
  X = 0
  XDirection = (0,1,0)
  Y = 0
FEATURE [TechDraw::DrawProjGroupItem] ProjItem025  label="Left003"
  CoarseView = false
  Direction = (1e-16,-1,0)
  Focus = 100
  HardHidden = true
  IsoCount = 0
  IsoHidden = false
  IsoVisible = false
  LockPosition = true
  Perspective = false
  Rotation = 0
  RotationVector = (1,0,0)
  Scale = 0.75
  ScaleType = 2
  SeamHidden = false
  SeamVisible = true
  SmoothHidden = false
  SmoothVisible = true
  Source = -> [Fillet005]
  Type = 1
  X = 176.991
  XDirection = (1,1e-16,0)
  Y = 0
FEATURE [TechDraw::DrawProjGroupItem] ProjItem026  label="Top006"
  CoarseView = false
  Direction = (0,0,1)
  Focus = 100
  HardHidden = false
  IsoCount = 0
  IsoHidden = false
  IsoVisible = false
  LockPosition = true
  Perspective = false
  Rotation = 0
  RotationVector = (1,0,0)
  Scale = 0.75
  ScaleType = 2
  SeamHidden = false
  SeamVisible = true
  SmoothHidden = false
  SmoothVisible = true
  Source = -> [Fillet005]
  Type = 4
  X = 0
  XDirection = (0,1,0)
  Y = -135.568
FEATURE [TechDraw::DrawProjGroup] ProjGroup006
  Anchor = -> ProjItem024
  AutoDistribute = true
  LockPosition = false
  ProjectionType = 0
  Rotation = 0
  Scale = 0.75
  ScaleType = 1
  Source = -> [Fillet005]
  Views = -> [ProjItem024,ProjItem025,ProjItem026]
  X = 121.515
  Y = 231.576
  spacingX = 15
  spacingY = 15
FEATURE [TechDraw::DrawViewDimension] Dimension086
  Arbitrary = false
  ArbitraryTolerances = false
  EqualTolerance = true
  FormatSpec = %.2f
  FormatSpecOverTolerance = %+.2f
  FormatSpecUnderTolerance = %+.2f
  Inverted = false
  LockPosition = false
  MeasureType = 1
  OverTolerance = 0
  References2D = -> [ProjItem025]
  Rotation = 0
  ScaleType = 0
  TheoreticalExact = false
  Type = 1
  UnderTolerance = 0
  X = -1.23785
  Y = -45.5907
FEATURE [TechDraw::DrawViewDimension] Dimension087
  Arbitrary = false
  ArbitraryTolerances = false
  EqualTolerance = true
  FormatSpec = ⌀%.2f
  FormatSpecOverTolerance = %+.2f
  FormatSpecUnderTolerance = %+.2f
  Inverted = false
  LockPosition = false
  MeasureType = 1
  OverTolerance = 0
  References2D = -> [ProjItem025]
  Rotation = 0
  ScaleType = 0
  TheoreticalExact = false
  Type = 5
  UnderTolerance = 0
  X = 40.064
  Y = 34.3958
FEATURE [TechDraw::DrawViewDimension] Dimension088
  Arbitrary = false
  ArbitraryTolerances = false
  EqualTolerance = true
  FormatSpec = ⌀%.2f
  FormatSpecOverTolerance = %+.2f
  FormatSpecUnderTolerance = %+.2f
  Inverted = false
  LockPosition = false
  MeasureType = 1
  OverTolerance = 0
  References2D = -> [ProjItem025]
  Rotation = 0
  ScaleType = 0
  TheoreticalExact = false
  Type = 5
  UnderTolerance = 0
  X = 29.2985
  Y = 16.4225
FEATURE [TechDraw::DrawViewDimension] Dimension089
  Arbitrary = false
  ArbitraryTolerances = false
  EqualTolerance = true
  FormatSpec = R%.2f
  FormatSpecOverTolerance = %+.2f
  FormatSpecUnderTolerance = %+.2f
  Inverted = false
  LockPosition = false
  MeasureType = 1
  OverTolerance = 0
  References2D = -> [ProjItem026]
  Rotation = 0
  ScaleType = 0
  TheoreticalExact = false
  Type = 4
  UnderTolerance = 0
  X = 90.1425
  Y = 70.5463
FEATURE [TechDraw::DrawViewDimension] Dimension090
  Arbitrary = false
  ArbitraryTolerances = false
  EqualTolerance = true
  FormatSpec = ⌀%.2f
  FormatSpecOverTolerance = %+.2f
  FormatSpecUnderTolerance = %+.2f
  Inverted = false
  LockPosition = false
  MeasureType = 1
  OverTolerance = 0
  References2D = -> [ProjItem026]
  Rotation = 0
  ScaleType = 0
  TheoreticalExact = false
  Type = 5
  UnderTolerance = 0
  X = -85.2072
  Y = 67.1933
FEATURE [TechDraw::DrawViewDimension] Dimension091
  Arbitrary = false
  ArbitraryTolerances = false
  EqualTolerance = true
  FormatSpec = %.2f
  FormatSpecOverTolerance = %+.2f
  FormatSpecUnderTolerance = %+.2f
  Inverted = false
  LockPosition = false
  MeasureType = 1
  OverTolerance = 0
  References2D = -> [ProjItem026]
  Rotation = 0
  ScaleType = 0
  TheoreticalExact = false
  Type = 1
  UnderTolerance = 0
  X = 90.9654
  Y = 42.0163
FEATURE [TechDraw::DrawViewDimension] Dimension092
  Arbitrary = false
  ArbitraryTolerances = false
  EqualTolerance = true
  FormatSpec = %.2f
  FormatSpecOverTolerance = %+.2f
  FormatSpecUnderTolerance = %+.2f
  Inverted = false
  LockPosition = false
  MeasureType = 1
  OverTolerance = 0
  References2D = -> [ProjItem026]
  Rotation = 0
  ScaleType = 0
  TheoreticalExact = false
  Type = 2
  UnderTolerance = 0
  X = 57.7044
  Y = 41.1917
FEATURE [TechDraw::DrawViewDimension] Dimension093
  Arbitrary = false
  ArbitraryTolerances = false
  EqualTolerance = true
  FormatSpec = %.2f
  FormatSpecOverTolerance = %+.2f
  FormatSpecUnderTolerance = %+.2f
  Inverted = false
  LockPosition = false
  MeasureType = 1
  OverTolerance = 0
  References2D = -> [ProjItem026]
  Rotation = 0
  ScaleType = 0
  TheoreticalExact = false
  Type = 2
  UnderTolerance = 0
  X = -62.9884
  Y = 66.0165
FEATURE [TechDraw::DrawViewDimension] Dimension094
  Arbitrary = false
  ArbitraryTolerances = false
  EqualTolerance = true
  FormatSpec = ⌀%.2f
  FormatSpecOverTolerance = %+.2f
  FormatSpecUnderTolerance = %+.2f
  Inverted = false
  LockPosition = false
  MeasureType = 1
  OverTolerance = 0
  References2D = -> [ProjItem026]
  Rotation = 0
  ScaleType = 0
  TheoreticalExact = false
  Type = 5
  UnderTolerance = 0
  X = 37.8013
  Y = 28.2329
FEATURE [TechDraw::DrawViewDimension] Dimension095
  Arbitrary = false
  ArbitraryTolerances = false
  EqualTolerance = true
  FormatSpec = %.2f
  FormatSpecOverTolerance = %+.2f
  FormatSpecUnderTolerance = %+.2f
  Inverted = false
  LockPosition = false
  MeasureType = 1
  OverTolerance = 0
  References2D = -> [ProjItem026]
  Rotation = 0
  ScaleType = 0
  TheoreticalExact = false
  Type = 1
  UnderTolerance = 0
  X = -63.5698
  Y = 26.7396
FEATURE [TechDraw::DrawViewDimension] Dimension096
  Arbitrary = false
  ArbitraryTolerances = false
  EqualTolerance = true
  FormatSpec = %.2f
  FormatSpecOverTolerance = %+.2f
  FormatSpecUnderTolerance = %+.2f
  Inverted = false
  LockPosition = false
  MeasureType = 1
  OverTolerance = 0
  References2D = -> [ProjItem026]
  Rotation = 0
  ScaleType = 0
  TheoreticalExact = false
  Type = 2
  UnderTolerance = 0
  X = -60.2619
  Y = 6.72372
FEATURE [TechDraw::DrawViewDimension] Dimension097
  Arbitrary = false
  ArbitraryTolerances = false
  EqualTolerance = true
  FormatSpec = %.2f
  FormatSpecOverTolerance = %+.2f
  FormatSpecUnderTolerance = %+.2f
  Inverted = false
  LockPosition = false
  MeasureType = 1
  OverTolerance = 0
  References2D = -> [ProjItem024]
  Rotation = 0
  ScaleType = 0
  TheoreticalExact = false
  Type = 2
  UnderTolerance = 0
  X = 87.7167
  Y = -45.1418
FEATURE [TechDraw::DrawViewDimension] Dimension098
  Arbitrary = false
  ArbitraryTolerances = false
  EqualTolerance = true
  FormatSpec = %.2f
  FormatSpecOverTolerance = %+.2f
  FormatSpecUnderTolerance = %+.2f
  Inverted = false
  LockPosition = false
  MeasureType = 1
  OverTolerance = 0
  References2D = -> [ProjItem024]
  Rotation = 0
  ScaleType = 0
  TheoreticalExact = false
  Type = 2
  UnderTolerance = 0
  X = -93.9214
  Y = -43.2012
FEATURE [TechDraw::DrawViewDimension] Dimension099
  Arbitrary = false
  ArbitraryTolerances = false
  EqualTolerance = true
  FormatSpec = %.2f
  FormatSpecOverTolerance = %+.2f
  FormatSpecUnderTolerance = %+.2f
  Inverted = false
  LockPosition = false
  MeasureType = 1
  OverTolerance = 0
  References2D = -> [ProjItem026]
  Rotation = 0
  ScaleType = 0
  TheoreticalExact = false
  Type = 2
  UnderTolerance = 0
  X = -95.2675
  Y = -61.5547
FEATURE [TechDraw::DrawViewDimension] Dimension100
  Arbitrary = false
  ArbitraryTolerances = false
  EqualTolerance = true
  FormatSpec = %.2f
  FormatSpecOverTolerance = %+.2f
  FormatSpecUnderTolerance = %+.2f
  Inverted = false
  LockPosition = false
  MeasureType = 1
  OverTolerance = 0
  References2D = -> [ProjItem024]
  Rotation = 0
  ScaleType = 0
  TheoreticalExact = false
  Type = 1
  UnderTolerance = 0
  X = 1.36085
  Y = -50.3237
FEATURE [TechDraw::DrawViewDimension] Dimension101
  Arbitrary = false
  ArbitraryTolerances = false
  EqualTolerance = true
  FormatSpec = %.2f
  FormatSpecOverTolerance = %+.2f
  FormatSpecUnderTolerance = %+.2f
  Inverted = false
  LockPosition = false
  MeasureType = 1
  OverTolerance = 0
  References2D = -> [ProjItem024]
  Rotation = 0
  ScaleType = 0
  TheoreticalExact = false
  Type = 1
  UnderTolerance = 0
  X = 2.04127
  Y = -42.7308
FEATURE [TechDraw::DrawViewDimension] Dimension102
  Arbitrary = false
  ArbitraryTolerances = false
  EqualTolerance = true
  FormatSpec = %.1f
  FormatSpecOverTolerance = %+.2f
  FormatSpecUnderTolerance = %+.2f
  Inverted = false
  LockPosition = false
  MeasureType = 1
  OverTolerance = 0
  References2D = -> [ProjItem025]
  Rotation = 0
  ScaleType = 0
  TheoreticalExact = false
  Type = 1
  UnderTolerance = 0
  X = 66.5689
  Y = -35.5199
FEATURE [TechDraw::DrawViewDimension] Dimension103
  Arbitrary = false
  ArbitraryTolerances = false
  EqualTolerance = true
  FormatSpec = %.2f
  FormatSpecOverTolerance = %+.2f
  FormatSpecUnderTolerance = %+.2f
  Inverted = false
  LockPosition = false
  MeasureType = 1
  OverTolerance = 0
  References2D = -> [ProjItem025]
  Rotation = 0
  ScaleType = 0
  TheoreticalExact = false
  Type = 2
  UnderTolerance = 0
  X = 71.0989
  Y = 30.871
FEATURE [TechDraw::DrawViewDimension] Dimension104
  Arbitrary = false
  ArbitraryTolerances = false
  EqualTolerance = true
  FormatSpec = %.2f
  FormatSpecOverTolerance = %+.2f
  FormatSpecUnderTolerance = %+.2f
  Inverted = false
  LockPosition = false
  MeasureType = 1
  OverTolerance = 0
  References2D = -> [ProjItem025]
  Rotation = 0
  ScaleType = 0
  TheoreticalExact = false
  Type = 2
  UnderTolerance = 0
  X = 71.0781
  Y = 9.61516
FEATURE [TechDraw::DrawViewDimension] Dimension105
  Arbitrary = false
  ArbitraryTolerances = false
  EqualTolerance = true
  FormatSpec = %.2f
  FormatSpecOverTolerance = %+.2f
  FormatSpecUnderTolerance = %+.2f
  Inverted = false
  LockPosition = false
  MeasureType = 1
  OverTolerance = 0
  References2D = -> [ProjItem025]
  Rotation = 0
  ScaleType = 0
  TheoreticalExact = false
  Type = 2
  UnderTolerance = 0
  X = 71.1255
  Y = -14.1
FEATURE [TechDraw::DrawViewDimension] Dimension106
  Arbitrary = false
  ArbitraryTolerances = false
  EqualTolerance = true
  FormatSpec = %.2f
  FormatSpecOverTolerance = %+.2f
  FormatSpecUnderTolerance = %+.2f
  Inverted = false
  LockPosition = false
  MeasureType = 1
  OverTolerance = 0
  References2D = -> [ProjItem025]
  Rotation = 0
  ScaleType = 0
  TheoreticalExact = false
  Type = 2
  UnderTolerance = 0
  X = -67.8964
  Y = 0.776424
FEATURE [TechDraw::DrawViewDimension] Dimension107
  Arbitrary = false
  ArbitraryTolerances = false
  EqualTolerance = true
  FormatSpec = %.2f
  FormatSpecOverTolerance = %+.2f
  FormatSpecUnderTolerance = %+.2f
  Inverted = false
  LockPosition = false
  MeasureType = 1
  OverTolerance = 0
  References2D = -> [ProjItem024]
  Rotation = 0
  ScaleType = 0
  TheoreticalExact = false
  Type = 2
  UnderTolerance = 0
  X = 87.022
  Y = 21.5663
FEATURE [TechDraw::DrawViewDimension] Dimension108
  Arbitrary = false
  ArbitraryTolerances = false
  EqualTolerance = true
  FormatSpec = %.2f
  FormatSpecOverTolerance = %+.2f
  FormatSpecUnderTolerance = %+.2f
  Inverted = false
  LockPosition = false
  MeasureType = 1
  OverTolerance = 0
  References2D = -> [ProjItem024]
  Rotation = 0
  ScaleType = 0
  TheoreticalExact = false
  Type = 2
  UnderTolerance = 0
  X = -94.804
  Y = 31.9137
FEATURE [TechDraw::DrawViewDimension] Dimension110
  Arbitrary = false
  ArbitraryTolerances = false
  EqualTolerance = true
  FormatSpec = %.2f
  FormatSpecOverTolerance = %+.2f
  FormatSpecUnderTolerance = %+.2f
  Inverted = false
  LockPosition = false
  MeasureType = 1
  OverTolerance = 0
  References2D = -> [ProjItem025]
  Rotation = 0
  ScaleType = 0
  TheoreticalExact = false
  Type = 1
  UnderTolerance = 0
  X = -37.2061
  Y = 47.7375
FEATURE [TechDraw::DrawViewPart] View005
  CoarseView = false
  Direction = (0.577,-0.577,0.577)
  Focus = 100
  HardHidden = false
  IsoCount = 0
  IsoHidden = false
  IsoVisible = false
  LockPosition = true
  Perspective = false
  Rotation = 0
  Scale = 0.4
  ScaleType = 0
  SeamHidden = false
  SeamVisible = true
  SmoothHidden = false
  SmoothVisible = true
  Source = -> [Fillet005]
  X = 305.238
  XDirection = (0.707,0.707,0)
  Y = 122.045
FEATURE [TechDraw::DrawViewDimension] Dimension111
  Arbitrary = false
  ArbitraryTolerances = false
  EqualTolerance = true
  FormatSpec = %.2f
  FormatSpecOverTolerance = %+.2f
  FormatSpecUnderTolerance = %+.2f
  Inverted = false
  LockPosition = false
  MeasureType = 1
  OverTolerance = 0
  References2D = -> [ProjItem024]
  Rotation = 0
  ScaleType = 0
  TheoreticalExact = false
  Type = 1
  UnderTolerance = 0
  X = -66.0661
  Y = 48.7057
FEATURE [TechDraw::DrawSVGTemplate] Template007
  Height = 297
  Orientation = 1
  Width = 420
FEATURE [Part::Fillet] Fillet006  label="Caja_central_fillet"
  Base = -> Fusion135
  Edges = 6 edges r=1: [Edge139,Edge141,Edge143,Edge145,Edge147,Edge149]
FEATURE [TechDraw::DrawProjGroupItem] ProjItem027  label="Front007"
  CoarseView = false
  Direction = (1,0,0)
  Focus = 100
  HardHidden = false
  IsoCount = 0
  IsoHidden = false
  IsoVisible = false
  LockPosition = true
  Perspective = false
  Rotation = 0
  RotationVector = (0,1,0)
  Scale = 0.75
  ScaleType = 2
  SeamHidden = false
  SeamVisible = true
  SmoothHidden = false
  SmoothVisible = true
  Source = -> [Fillet006]
  Type = 0
  X = 0
  XDirection = (0,1,0)
  Y = 0
FEATURE [TechDraw::DrawProjGroupItem] ProjItem028  label="Top007"
  CoarseView = false
  Direction = (0,0,1)
  Focus = 100
  HardHidden = false
  IsoCount = 0
  IsoHidden = false
  IsoVisible = false
  LockPosition = true
  Perspective = false
  Rotation = 0
  RotationVector = (1,0,0)
  Scale = 0.75
  ScaleType = 2
  SeamHidden = false
  SeamVisible = true
  SmoothHidden = false
  SmoothVisible = true
  Source = -> [Fillet006]
  Type = 4
  X = 0
  XDirection = (0,1,0)
  Y = -125.75
FEATURE [TechDraw::DrawProjGroupItem] ProjItem029  label="Left004"
  CoarseView = false
  Direction = (1e-16,-1,0)
  Focus = 100
  HardHidden = true
  IsoCount = 0
  IsoHidden = false
  IsoVisible = false
  LockPosition = true
  Perspective = false
  Rotation = 0
  RotationVector = (1,0,0)
  Scale = 0.75
  ScaleType = 2
  SeamHidden = false
  SeamVisible = true
  SmoothHidden = false
  SmoothVisible = true
  Source = -> [Fillet006]
  Type = 1
  X = 192.694
  XDirection = (1,1e-16,0)
  Y = 0
FEATURE [TechDraw::DrawProjGroup] ProjGroup007
  Anchor = -> ProjItem027
  AutoDistribute = true
  LockPosition = false
  ProjectionType = 0
  Rotation = 0
  Scale = 0.75
  ScaleType = 2
  Views = -> [ProjItem027,ProjItem028,ProjItem029]
  X = 114.01
  Y = 223.106
  spacingX = 15
  spacingY = 15
FEATURE [TechDraw::DrawViewDimension] Dimension126
  Arbitrary = false
  ArbitraryTolerances = false
  EqualTolerance = true
  FormatSpec = %.2f
  FormatSpecOverTolerance = %+.2f
  FormatSpecUnderTolerance = %+.2f
  Inverted = false
  LockPosition = false
  MeasureType = 1
  OverTolerance = 0
  References2D = -> [ProjItem029]
  Rotation = 0
  ScaleType = 0
  TheoreticalExact = false
  Type = 2
  UnderTolerance = 0
  X = 62.2261
  Y = 11.3366
FEATURE [TechDraw::DrawViewDimension] Dimension120
  Arbitrary = false
  ArbitraryTolerances = false
  EqualTolerance = true
  FormatSpec = ⌀%.2f
  FormatSpecOverTolerance = %+.2f
  FormatSpecUnderTolerance = %+.2f
  Inverted = false
  LockPosition = false
  MeasureType = 1
  OverTolerance = 0
  References2D = -> [ProjItem028]
  Rotation = 0
  ScaleType = 0
  TheoreticalExact = false
  Type = 5
  UnderTolerance = 0
  X = -68.0317
  Y = -26.3591
FEATURE [TechDraw::DrawViewDimension] Dimension128
  Arbitrary = false
  ArbitraryTolerances = false
  EqualTolerance = true
  FormatSpec = %.2f
  FormatSpecOverTolerance = %+.2f
  FormatSpecUnderTolerance = %+.2f
  Inverted = false
  LockPosition = false
  MeasureType = 1
  OverTolerance = 0
  References2D = -> [ProjItem027]
  Rotation = 0
  ScaleType = 0
  TheoreticalExact = false
  Type = 2
  UnderTolerance = 0
  X = -68.5011
  Y = 4.00474
FEATURE [TechDraw::DrawViewDimension] Dimension129
  Arbitrary = false
  ArbitraryTolerances = false
  EqualTolerance = true
  FormatSpec = %.2f
  FormatSpecOverTolerance = %+.2f
  FormatSpecUnderTolerance = %+.2f
  Inverted = false
  LockPosition = false
  MeasureType = 1
  OverTolerance = 0
  References2D = -> [ProjItem027]
  Rotation = 0
  ScaleType = 0
  TheoreticalExact = false
  Type = 2
  UnderTolerance = 0
  X = -92.6122
  Y = -40.5172
FEATURE [TechDraw::DrawViewDimension] Dimension130
  Arbitrary = false
  ArbitraryTolerances = false
  EqualTolerance = true
  FormatSpec = %.2f
  FormatSpecOverTolerance = %+.2f
  FormatSpecUnderTolerance = %+.2f
  Inverted = false
  LockPosition = false
  MeasureType = 1
  OverTolerance = 0
  References2D = -> [ProjItem027]
  Rotation = 0
  ScaleType = 0
  TheoreticalExact = false
  Type = 2
  UnderTolerance = 0
  X = 87.0544
  Y = 7.39886
FEATURE [TechDraw::DrawViewDimension] Dimension136
  Arbitrary = false
  ArbitraryTolerances = false
  EqualTolerance = true
  FormatSpec = %.2f
  FormatSpecOverTolerance = %+.2f
  FormatSpecUnderTolerance = %+.2f
  Inverted = false
  LockPosition = false
  MeasureType = 1
  OverTolerance = 0
  References2D = -> [ProjItem029]
  Rotation = 0
  ScaleType = 0
  TheoreticalExact = false
  Type = 1
  UnderTolerance = 0
  X = 62.5065
  Y = 48.6112
FEATURE [TechDraw::DrawViewPart] View006
  CoarseView = false
  Direction = (0.577,-0.577,0.577)
  Focus = 100
  HardHidden = false
  IsoCount = 0
  IsoHidden = false
  IsoVisible = false
  LockPosition = false
  Perspective = false
  Rotation = 0
  Scale = 0.4
  ScaleType = 0
  SeamHidden = false
  SeamVisible = true
  SmoothHidden = false
  SmoothVisible = true
  Source = -> [Fillet006]
  X = 303.456
  XDirection = (0.707,0.707,0)
  Y = 123.156
FEATURE [TechDraw::DrawSVGTemplate] Template008
  Height = 297
  Orientation = 1
  Width = 420
FEATURE [TechDraw::DrawViewDimension] Dimension153
  Arbitrary = false
  ArbitraryTolerances = false
  EqualTolerance = true
  FormatSpec = %.2f
  FormatSpecOverTolerance = %+.2f
  FormatSpecUnderTolerance = %+.2f
  Inverted = false
  LockPosition = false
  MeasureType = 1
  OverTolerance = 0
  References2D = -> [ProjItem026]
  Rotation = 0
  ScaleType = 0
  TheoreticalExact = false
  Type = 1
  UnderTolerance = 0
  X = 61.7958
  Y = -4.64166
FEATURE [TechDraw::DrawSVGTemplate] Template009
  Height = 297
  Orientation = 1
  Width = 420
FEATURE [TechDraw::DrawProjGroupItem] ProjItem033  label="Front009"
  CoarseView = false
  Direction = (0,0,-1)
  Focus = 100
  HardHidden = false
  IsoCount = 0
  IsoHidden = false
  IsoVisible = false
  LockPosition = true
  Perspective = false
  Rotation = 0
  RotationVector = (0,-1,0)
  Scale = 0.75
  ScaleType = 2
  SeamHidden = false
  SeamVisible = true
  SmoothHidden = false
  SmoothVisible = true
  Source = -> [Cut001002115]
  Type = 0
  X = 0
  XDirection = (0,-1,0)
  Y = 0
FEATURE [TechDraw::DrawProjGroupItem] ProjItem034  label="Left006"
  CoarseView = false
  Direction = (0,1,-1e-16)
  Focus = 100
  HardHidden = true
  IsoCount = 0
  IsoHidden = false
  IsoVisible = false
  LockPosition = true
  Perspective = false
  Rotation = 0
  RotationVector = (1,0,0)
  Scale = 0.75
  ScaleType = 2
  SeamHidden = false
  SeamVisible = true
  SmoothHidden = false
  SmoothVisible = true
  Source = -> [Cut001002115]
  Type = 1
  X = 153.015
  XDirection = (0,-1e-16,-1)
  Y = 0
FEATURE [TechDraw::DrawProjGroupItem] ProjItem035  label="Top009"
  CoarseView = false
  Direction = (-1,0,0)
  Focus = 100
  HardHidden = true
  IsoCount = 0
  IsoHidden = false
  IsoVisible = false
  LockPosition = true
  Perspective = false
  Rotation = 0
  RotationVector = (1,0,0)
  Scale = 0.75
  ScaleType = 2
  SeamHidden = false
  SeamVisible = true
  SmoothHidden = false
  SmoothVisible = true
  Source = -> [Cut001002115]
  Type = 4
  X = 0
  XDirection = (0,-1,0)
  Y = -98.808
FEATURE [TechDraw::DrawProjGroup] ProjGroup009
  Anchor = -> ProjItem033
  AutoDistribute = true
  LockPosition = false
  ProjectionType = 0
  Rotation = 0
  Scale = 0.75
  ScaleType = 2
  Source = -> [Cut001002115]
  Views = -> [ProjItem033,ProjItem034,ProjItem035]
  X = 137.487
  Y = 198.045
  spacingX = 15
  spacingY = 15
FEATURE [TechDraw::DrawViewDimension] Dimension179
  Arbitrary = false
  ArbitraryTolerances = false
  EqualTolerance = true
  FormatSpec = %.2f
  FormatSpecOverTolerance = %+.2f
  FormatSpecUnderTolerance = %+.2f
  Inverted = false
  LockPosition = false
  MeasureType = 1
  OverTolerance = 0
  References2D = -> [ProjItem033]
  Rotation = 0
  ScaleType = 0
  TheoreticalExact = false
  Type = 1
  UnderTolerance = 0
  X = 0.734857
  Y = 71.8977
FEATURE [TechDraw::DrawViewDimension] Dimension180
  Arbitrary = false
  ArbitraryTolerances = false
  EqualTolerance = true
  FormatSpec = %.2f
  FormatSpecOverTolerance = %+.2f
  FormatSpecUnderTolerance = %+.2f
  Inverted = false
  LockPosition = false
  MeasureType = 1
  OverTolerance = 0
  References2D = -> [ProjItem033]
  Rotation = 0
  ScaleType = 0
  TheoreticalExact = false
  Type = 1
  UnderTolerance = 0
  X = 94.6926
  Y = 71.8977
FEATURE [TechDraw::DrawViewDimension] Dimension181
  Arbitrary = false
  ArbitraryTolerances = false
  EqualTolerance = true
  FormatSpec = ⌀%.2f
  FormatSpecOverTolerance = %+.2f
  FormatSpecUnderTolerance = %+.2f
  Inverted = false
  LockPosition = false
  MeasureType = 1
  OverTolerance = 0
  References2D = -> [ProjItem033]
  Rotation = 0
  ScaleType = 0
  TheoreticalExact = false
  Type = 5
  UnderTolerance = 0
  X = -40.1722
  Y = 11.7577
FEATURE [TechDraw::DrawViewDimension] Dimension182
  Arbitrary = false
  ArbitraryTolerances = false
  EqualTolerance = true
  FormatSpec = %.2f
  FormatSpecOverTolerance = %+.2f
  FormatSpecUnderTolerance = %+.2f
  Inverted = false
  LockPosition = false
  MeasureType = 1
  OverTolerance = 0
  References2D = -> [ProjItem033]
  Rotation = 0
  ScaleType = 0
  TheoreticalExact = false
  Type = 2
  UnderTolerance = 0
  X = 53.4194
  Y = -0.274237
FEATURE [TechDraw::DrawViewDimension] Dimension183
  Arbitrary = false
  ArbitraryTolerances = false
  EqualTolerance = true
  FormatSpec = ⌀%.2f
  FormatSpecOverTolerance = %+.2f
  FormatSpecUnderTolerance = %+.2f
  Inverted = false
  LockPosition = false
  MeasureType = 1
  OverTolerance = 0
  References2D = -> [ProjItem033]
  Rotation = 0
  ScaleType = 0
  TheoreticalExact = false
  Type = 5
  UnderTolerance = 0
  X = -66.872
  Y = -34.2933
FEATURE [TechDraw::DrawViewDimension] Dimension184
  Arbitrary = false
  ArbitraryTolerances = false
  EqualTolerance = true
  FormatSpec = R%.2f
  FormatSpecOverTolerance = %+.2f
  FormatSpecUnderTolerance = %+.2f
  Inverted = false
  LockPosition = false
  MeasureType = 1
  OverTolerance = 0
  References2D = -> [ProjItem033]
  Rotation = 0
  ScaleType = 0
  TheoreticalExact = false
  Type = 4
  UnderTolerance = 0
  X = 100.827
  Y = -60.9277
FEATURE [TechDraw::DrawViewDimension] Dimension185
  Arbitrary = false
  ArbitraryTolerances = false
  EqualTolerance = true
  FormatSpec = %.2f
  FormatSpecOverTolerance = %+.2f
  FormatSpecUnderTolerance = %+.2f
  Inverted = false
  LockPosition = false
  MeasureType = 1
  OverTolerance = 0
  References2D = -> [ProjItem033]
  Rotation = 0
  ScaleType = 0
  TheoreticalExact = false
  Type = 1
  UnderTolerance = 0
  X = 95.5107
  Y = -34.0766
FEATURE [TechDraw::DrawViewDimension] Dimension186
  Arbitrary = false
  ArbitraryTolerances = false
  EqualTolerance = true
  FormatSpec = R%.2f
  FormatSpecOverTolerance = %+.2f
  FormatSpecUnderTolerance = %+.2f
  Inverted = false
  LockPosition = false
  MeasureType = 1
  OverTolerance = 0
  References2D = -> [ProjItem035]
  Rotation = 0
  ScaleType = 0
  TheoreticalExact = false
  Type = 4
  UnderTolerance = 0
  X = 98.7611
  Y = 17.5161
FEATURE [TechDraw::DrawViewDimension] Dimension187
  Arbitrary = false
  ArbitraryTolerances = false
  EqualTolerance = true
  FormatSpec = %.2f
  FormatSpecOverTolerance = %+.2f
  FormatSpecUnderTolerance = %+.2f
  Inverted = false
  LockPosition = false
  MeasureType = 1
  OverTolerance = 0
  References2D = -> [ProjItem035]
  Rotation = 0
  ScaleType = 0
  TheoreticalExact = false
  Type = 2
  UnderTolerance = 0
  X = -73.4049
  Y = -18.0821
FEATURE [TechDraw::DrawViewDimension] Dimension188
  Arbitrary = false
  ArbitraryTolerances = false
  EqualTolerance = true
  FormatSpec = %.2f
  FormatSpecOverTolerance = %+.2f
  FormatSpecUnderTolerance = %+.2f
  Inverted = false
  LockPosition = false
  MeasureType = 1
  OverTolerance = 0
  References2D = -> [ProjItem035]
  Rotation = 0
  ScaleType = 0
  TheoreticalExact = false
  Type = 2
  UnderTolerance = 0
  X = 65.6063
  Y = 13.8055
FEATURE [TechDraw::DrawViewDimension] Dimension189
  Arbitrary = false
  ArbitraryTolerances = false
  EqualTolerance = true
  FormatSpec = R%.2f
  FormatSpecOverTolerance = %+.2f
  FormatSpecUnderTolerance = %+.2f
  Inverted = false
  LockPosition = false
  MeasureType = 1
  OverTolerance = 0
  References2D = -> [ProjItem034]
  Rotation = 0
  ScaleType = 0
  TheoreticalExact = false
  Type = 4
  UnderTolerance = 0
  X = -13.7893
  Y = -62.0518
FEATURE [TechDraw::DrawViewPart] View008
  CoarseView = false
  Direction = (-0.577,0.577,0.577)
  Focus = 100
  HardHidden = false
  IsoCount = 0
  IsoHidden = false
  IsoVisible = false
  LockPosition = false
  Perspective = false
  Rotation = 0
  Scale = 0.4
  ScaleType = 0
  SeamHidden = false
  SeamVisible = true
  SmoothHidden = false
  SmoothVisible = true
  Source = -> [Cut001002115]
  X = 342.019
  XDirection = (-0.707,-0.707,0)
  Y = 113.08
FEATURE [TechDraw::DrawSVGTemplate] Template010
  Height = 297
  Orientation = 1
  Width = 420
FEATURE [TechDraw::DrawProjGroupItem] ProjItem036  label="Front010"
  CoarseView = false
  Direction = (0,0,-1)
  Focus = 100
  HardHidden = false
  IsoCount = 0
  IsoHidden = false
  IsoVisible = false
  LockPosition = true
  Perspective = false
  Rotation = 0
  RotationVector = (0,1,0)
  Scale = 0.75
  ScaleType = 2
  SeamHidden = false
  SeamVisible = true
  SmoothHidden = false
  SmoothVisible = true
  Source = -> [Cut001002114]
  Type = 0
  X = 0
  XDirection = (0,1,0)
  Y = 0
FEATURE [TechDraw::DrawProjGroupItem] ProjItem037  label="Left007"
  CoarseView = false
  Direction = (0,-1,-1e-16)
  Focus = 100
  HardHidden = true
  IsoCount = 0
  IsoHidden = false
  IsoVisible = false
  LockPosition = true
  Perspective = false
  Rotation = 0
  RotationVector = (1,0,0)
  ScaleType = 2
  SeamHidden = false
  SeamVisible = true
  SmoothHidden = false
  SmoothVisible = true
  Source = -> [Cut001002114]
  Type = 1
  X = 155.902
  XDirection = (0,1e-16,-1)
  Y = 0
FEATURE [TechDraw::DrawProjGroupItem] ProjItem038  label="Top010"
  CoarseView = false
  Direction = (1,0,0)
  Focus = 100
  HardHidden = true
  IsoCount = 0
  IsoHidden = false
  IsoVisible = false
  LockPosition = true
  Perspective = false
  Rotation = 0
  RotationVector = (1,0,0)
  ScaleType = 2
  SeamHidden = false
  SeamVisible = true
  SmoothHidden = false
  SmoothVisible = true
  Source = -> [Cut001002114]
  Type = 4
  X = 0
  XDirection = (0,1,0)
  Y = -106.239
FEATURE [TechDraw::DrawProjGroup] ProjGroup010
  Anchor = -> ProjItem036
  AutoDistribute = true
  LockPosition = false
  ProjectionType = 0
  Rotation = 0
  Scale = 0.75
  ScaleType = 2
  Source = -> [Cut001002114]
  Views = -> [ProjItem036,ProjItem037,ProjItem038]
  X = 137.782
  Y = 202.452
  spacingX = 15
  spacingY = 15
FEATURE [TechDraw::DrawViewDimension] Dimension190
  Arbitrary = false
  ArbitraryTolerances = false
  EqualTolerance = true
  FormatSpec = %.2f
  FormatSpecOverTolerance = %+.2f
  FormatSpecUnderTolerance = %+.2f
  Inverted = false
  LockPosition = false
  MeasureType = 1
  OverTolerance = 0
  References2D = -> [ProjItem036]
  Rotation = 0
  ScaleType = 0
  TheoreticalExact = false
  Type = 1
  UnderTolerance = 0
  X = 0.536664
  Y = 71.352
FEATURE [TechDraw::DrawViewDimension] Dimension191
  Arbitrary = false
  ArbitraryTolerances = false
  EqualTolerance = true
  FormatSpec = %.2f
  FormatSpecOverTolerance = %+.2f
  FormatSpecUnderTolerance = %+.2f
  Inverted = false
  LockPosition = false
  MeasureType = 1
  OverTolerance = 0
  References2D = -> [ProjItem036]
  Rotation = 0
  ScaleType = 0
  TheoreticalExact = false
  Type = 1
  UnderTolerance = 0
  X = 92.4488
  Y = 71.352
FEATURE [TechDraw::DrawViewDimension] Dimension192
  Arbitrary = false
  ArbitraryTolerances = false
  EqualTolerance = true
  FormatSpec = ⌀%.2f
  FormatSpecOverTolerance = %+.2f
  FormatSpecUnderTolerance = %+.2f
  Inverted = false
  LockPosition = false
  MeasureType = 1
  OverTolerance = 0
  References2D = -> [ProjItem036]
  Rotation = 0
  ScaleType = 0
  TheoreticalExact = false
  Type = 5
  UnderTolerance = 0
  X = -68.3826
  Y = -34.5315
FEATURE [TechDraw::DrawViewDimension] Dimension193
  Arbitrary = false
  ArbitraryTolerances = false
  EqualTolerance = true
  FormatSpec = ⌀%.2f
  FormatSpecOverTolerance = %+.2f
  FormatSpecUnderTolerance = %+.2f
  Inverted = false
  LockPosition = false
  MeasureType = 1
  OverTolerance = 0
  References2D = -> [ProjItem036]
  Rotation = 0
  ScaleType = 0
  TheoreticalExact = false
  Type = 5
  UnderTolerance = 0
  X = 33.5109
  Y = 8.84551
FEATURE [TechDraw::DrawViewDimension] Dimension194
  Arbitrary = false
  ArbitraryTolerances = false
  EqualTolerance = true
  FormatSpec = %.2f
  FormatSpecOverTolerance = %+.2f
  FormatSpecUnderTolerance = %+.2f
  Inverted = false
  LockPosition = false
  MeasureType = 1
  OverTolerance = 0
  References2D = -> [ProjItem036]
  Rotation = 0
  ScaleType = 0
  TheoreticalExact = false
  Type = 2
  UnderTolerance = 0
  X = 63.9014
  Y = 0.343722
FEATURE [TechDraw::DrawViewDimension] Dimension195
  Arbitrary = false
  ArbitraryTolerances = false
  EqualTolerance = true
  FormatSpec = %.2f
  FormatSpecOverTolerance = %+.2f
  FormatSpecUnderTolerance = %+.2f
  Inverted = false
  LockPosition = false
  MeasureType = 1
  OverTolerance = 0
  References2D = -> [ProjItem036]
  Rotation = 0
  ScaleType = 0
  TheoreticalExact = false
  Type = 1
  UnderTolerance = 0
  X = 94.1144
  Y = -35.133
FEATURE [TechDraw::DrawViewDimension] Dimension196
  Arbitrary = false
  ArbitraryTolerances = false
  EqualTolerance = true
  FormatSpec = %.2f
  FormatSpecOverTolerance = %+.2f
  FormatSpecUnderTolerance = %+.2f
  Inverted = false
  LockPosition = false
  MeasureType = 1
  OverTolerance = 0
  References2D = -> [ProjItem033]
  Rotation = 0
  ScaleType = 0
  TheoreticalExact = false
  Type = 1
  UnderTolerance = 0
  X = -95.5297
  Y = -22.9946
FEATURE [TechDraw::DrawViewDimension] Dimension197
  Arbitrary = false
  ArbitraryTolerances = false
  EqualTolerance = true
  FormatSpec = %.2f
  FormatSpecOverTolerance = %+.2f
  FormatSpecUnderTolerance = %+.2f
  Inverted = false
  LockPosition = false
  MeasureType = 1
  OverTolerance = 0
  References2D = -> [ProjItem036]
  Rotation = 0
  ScaleType = 0
  TheoreticalExact = false
  Type = 1
  UnderTolerance = 0
  X = -92.4188
  Y = -22.6911
FEATURE [TechDraw::DrawViewDimension] Dimension198
  Arbitrary = false
  ArbitraryTolerances = false
  EqualTolerance = true
  FormatSpec = R%.2f
  FormatSpecOverTolerance = %+.2f
  FormatSpecUnderTolerance = %+.2f
  Inverted = false
  LockPosition = false
  MeasureType = 1
  OverTolerance = 0
  References2D = -> [ProjItem036]
  Rotation = 0
  ScaleType = 0
  TheoreticalExact = false
  Type = 4
  UnderTolerance = 0
  X = 99.8522
  Y = -59.367
FEATURE [TechDraw::DrawViewDimension] Dimension199
  Arbitrary = false
  ArbitraryTolerances = false
  EqualTolerance = true
  FormatSpec = R%.2f
  FormatSpecOverTolerance = %+.2f
  FormatSpecUnderTolerance = %+.2f
  Inverted = false
  LockPosition = false
  MeasureType = 1
  OverTolerance = 0
  References2D = -> [ProjItem037]
  Rotation = 0
  ScaleType = 0
  TheoreticalExact = false
  Type = 4
  UnderTolerance = 0
  X = -14.3638
  Y = -62.5021
FEATURE [TechDraw::DrawViewDimension] Dimension200
  Arbitrary = false
  ArbitraryTolerances = false
  EqualTolerance = true
  FormatSpec = R%.2f
  FormatSpecOverTolerance = %+.2f
  FormatSpecUnderTolerance = %+.2f
  Inverted = false
  LockPosition = false
  MeasureType = 1
  OverTolerance = 0
  References2D = -> [ProjItem038]
  Rotation = 0
  ScaleType = 0
  TheoreticalExact = false
  Type = 4
  UnderTolerance = 0
  X = 89.8063
  Y = 16.6931
FEATURE [TechDraw::DrawViewDimension] Dimension201
  Arbitrary = false
  ArbitraryTolerances = false
  EqualTolerance = true
  FormatSpec = %.2f
  FormatSpecOverTolerance = %+.2f
  FormatSpecUnderTolerance = %+.2f
  Inverted = false
  LockPosition = false
  MeasureType = 1
  OverTolerance = 0
  References2D = -> [ProjItem038]
  Rotation = 0
  ScaleType = 0
  TheoreticalExact = false
  Type = 2
  UnderTolerance = 0
  X = 63.3266
  Y = 14.2714
FEATURE [TechDraw::DrawViewDimension] Dimension202
  Arbitrary = false
  ArbitraryTolerances = false
  EqualTolerance = true
  FormatSpec = %.2f
  FormatSpecOverTolerance = %+.2f
  FormatSpecUnderTolerance = %+.2f
  Inverted = false
  LockPosition = false
  MeasureType = 1
  OverTolerance = 0
  References2D = -> [ProjItem038]
  Rotation = 0
  ScaleType = 0
  TheoreticalExact = false
  Type = 2
  UnderTolerance = 0
  X = -69.471
  Y = -13.4184
FEATURE [TechDraw::DrawViewPart] View009
  CoarseView = false
  Direction = (0.577,-0.577,0.577)
  Focus = 100
  HardHidden = false
  IsoCount = 0
  IsoHidden = false
  IsoVisible = false
  LockPosition = true
  Perspective = false
  Rotation = 0
  Scale = 0.4
  ScaleType = 0
  SeamHidden = false
  SeamVisible = true
  SmoothHidden = false
  SmoothVisible = true
  Source = -> [Cut001002114]
  X = 343.685
  XDirection = (0.707,0.707,0)
  Y = 113.932
FEATURE [TechDraw::DrawSVGTemplate] Template011
  Height = 297
  Orientation = 1
  Width = 420
FEATURE [TechDraw::DrawSVGTemplate] Template012
  Height = 297
  Orientation = 1
  Width = 420
FEATURE [TechDraw::DrawProjGroupItem] ProjItem042  label="Front012"
  CoarseView = false
  Direction = (0,-1,0)
  Focus = 100
  HardHidden = true
  IsoCount = 0
  IsoHidden = false
  IsoVisible = false
  LockPosition = true
  Perspective = false
  Rotation = 0
  RotationVector = (1,0,0)
  Scale = 0.5
  ScaleType = 2
  SeamHidden = false
  SeamVisible = true
  SmoothHidden = false
  SmoothVisible = true
  Source = -> [Cut001002086,Clone001,Clone002,Clone003,Clone,Clone004,Clone008,Clone011,Clone017,Clone014,_1700_Cell,Fusion116,Fusion125]
  Type = 0
  X = 0
  XDirection = (1,0,0)
  Y = 0
FEATURE [TechDraw::DrawProjGroupItem] ProjItem043  label="Left009"
  CoarseView = false
  Direction = (-1,-1e-16,0)
  Focus = 100
  HardHidden = false
  IsoCount = 0
  IsoHidden = false
  IsoVisible = false
  LockPosition = true
  Perspective = false
  Rotation = 0
  RotationVector = (1,0,0)
  ScaleType = 2
  SeamHidden = false
  SeamVisible = true
  SmoothHidden = false
  SmoothVisible = true
  Source = -> [Cut001002086,Clone001,Clone002,Clone003,Clone,Clone004,Clone008,Clone011,Clone017,Clone014,_1700_Cell,Fusion116,Fusion125]
  Type = 1
  X = 194.326
  XDirection = (1e-16,-1,0)
  Y = 0
FEATURE [TechDraw::DrawProjGroupItem] ProjItem044  label="Top012"
  CoarseView = false
  Direction = (0,0,1)
  Focus = 100
  HardHidden = false
  IsoCount = 0
  IsoHidden = false
  IsoVisible = false
  LockPosition = true
  Perspective = false
  Rotation = 0
  RotationVector = (1,0,0)
  ScaleType = 2
  SeamHidden = false
  SeamVisible = true
  SmoothHidden = false
  SmoothVisible = true
  Source = -> [Cut001002086,Clone001,Clone002,Clone003,Clone,Clone004,Clone008,Clone011,Clone017,Clone014,_1700_Cell,Fusion116,Fusion125]
  Type = 4
  X = 0
  XDirection = (1,0,0)
  Y = -97.2315
FEATURE [TechDraw::DrawProjGroup] ProjGroup012
  Anchor = -> ProjItem042
  AutoDistribute = true
  LockPosition = false
  ProjectionType = 0
  Rotation = 0
  Scale = 0.5
  ScaleType = 2
  Source = -> [Cut001002086,Clone001,Clone002,Clone003,Clone,Clone004,Clone008,Clone011,Clone017,Clone014,_1700_Cell,Fusion116,Fusion125]
  Views = -> [ProjItem042,ProjItem043,ProjItem044]
  X = 128.655
  Y = 238.165
  spacingX = 15
  spacingY = 15
FEATURE [TechDraw::DrawViewBalloon] Balloon006
  BubbleShape = 0
  EndType = 0
  EndTypeScale = 1
  KinkLength = 5
  LockPosition = false
  OriginX = -180.999
  OriginY = 17.6718
  Rotation = 0
  ScaleType = 0
  ShapeScale = 1
  SourceView = -> ProjItem044
  Text = 1
  TextWrapLen = -1
  X = -218.226
  Y = 70.6704
FEATURE [TechDraw::DrawViewBalloon] Balloon007
  BubbleShape = 0
  EndType = 0
  EndTypeScale = 1
  KinkLength = 5
  LockPosition = false
  OriginX = -110.982
  OriginY = 77.4576
  Rotation = 0
  ScaleType = 0
  ShapeScale = 1
  SourceView = -> ProjItem044
  Text = 2
  TextWrapLen = -1
  X = -70.9822
  Y = 117.458
FEATURE [TechDraw::DrawViewBalloon] Balloon008
  BubbleShape = 0
  EndType = 0
  EndTypeScale = 1
  KinkLength = 5
  LockPosition = false
  OriginX = -190.219
  OriginY = -5.93582
  Rotation = 0
  ScaleType = 0
  ShapeScale = 1
  SourceView = -> ProjItem042
  Text = 3
  TextWrapLen = -1
  X = -219.728
  Y = 50.7581
FEATURE [TechDraw::DrawViewBalloon] Balloon009
  BubbleShape = 0
  EndType = 0
  EndTypeScale = 1
  KinkLength = 5
  LockPosition = false
  OriginX = -134.96
  OriginY = -34.5345
  Rotation = 0
  ScaleType = 0
  ShapeScale = 1
  SourceView = -> ProjItem042
  Text = 4
  TextWrapLen = -1
  X = -186.573
  Y = -74.514
FEATURE [TechDraw::DrawViewBalloon] Balloon010
  BubbleShape = 0
  EndType = 0
  EndTypeScale = 1
  KinkLength = 5
  LockPosition = false
  OriginX = 183.018
  OriginY = 5.21283
  Rotation = 0
  ScaleType = 0
  ShapeScale = 1
  SourceView = -> ProjItem042
  Text = 5
  TextWrapLen = -1
  X = 229.805
  Y = 44.2434
FEATURE [TechDraw::DrawViewPart] View012
  CoarseView = false
  Direction = (-0.577,-0.577,0.577)
  Focus = 100
  HardHidden = false
  IsoCount = 0
  IsoHidden = false
  IsoVisible = false
  LockPosition = true
  Perspective = false
  Rotation = 0
  Scale = 0.4
  ScaleType = 0
  SeamHidden = false
  SeamVisible = true
  SmoothHidden = false
  SmoothVisible = true
  Source = -> [Cut001002086,Clone,Clone004,Clone008,Clone011,Clone017,Clone014,Fusion116,Fusion125,Clone001,_1700_Cell]
  X = 317.998
  XDirection = (0.707,-0.707,0)
  Y = 140.07
FEATURE [Spreadsheet::Sheet] Spreadsheet  label="numeracion_piezas"
  cells = A1=1; B1=Pletina de Cobre; A2=2; B2=Pletina de Níquel; A3=3; B3=Tapa Lateral Izquierda; A4=4; B4=Soporte de Celda; A5=5; B5=Tapa Lateral Derecha; A7=1; B7=Base Izquierda Caja Batería; A8=2; B8=Base Central Caja Batería; A9=3; B9=Base Derecha Caja Batería; A10=4; B10=Tapa Izquierda Caja Batería; A11=5; B11=Tapa Central Caja Batería; A12=6; B12=Tapa Derecha Caja Batería
FEATURE [TechDraw::DrawViewSpreadsheet] Sheet
  CellEnd = B5
  CellStart = A1
  Font = osifont
  LineWidth = 0.35
  LockPosition = false
  Rotation = 0
  ScaleType = 2
  Source = -> Spreadsheet
  Symbol = <blob: 2299 chars omitted>
  TextSize = 10
  X = 187.569
  Y = 44.5698
FEATURE [TechDraw::DrawViewSpreadsheet] Sheet001
  CellEnd = B12
  CellStart = A7
  Font = osifont
  LineWidth = 0.35
  LockPosition = true
  Rotation = 0
  ScaleType = 2
  Source = -> Spreadsheet
  Symbol = <blob: 2760 chars omitted>
  TextSize = 8
  X = 187.443
  Y = 46.9937
FEATURE [Part::Part2DObjectPython] ShapeString  # Draft 2D object (typed FeaturePython)
  FontFile = <userpath>/Documents/tfm_augusto/Mecanica/Caja_bateria/logos/Staatliches-Regular.ttf
  Placement = pos=(393.3,10.68,29.06) rot=(0.57735,0.57735,0.57735;2.0944rad)
  Size = 6
  String = BATERIA 84AH 12V
  Tracking = 0
FEATURE [Part::Extrusion] Extrude001
  Base = -> ShapeString
  Dir = (1,-2e-16,2e-16)
  DirMode = 2
  FaceMakerClass = Part::FaceMakerBullseye
  LengthFwd = -1
  LengthRev = 0
  Placement = pos=(0.3,12,7) rot=(0,0,1;0rad)
  Solid = false
  Symmetric = false
FEATURE [Part::Part2DObjectPython] ShapeString001  # Draft 2D object (typed FeaturePython)
  FontFile = <userpath>/Documents/tfm_augusto/Mecanica/Caja_bateria/logos/Staatliches-Regular.ttf
  Placement = pos=(393.07,148,2.37) rot=(0.57735,0.57735,0.57735;2.0944rad)
  Size = 2
  String = Conector CAN
  Tracking = 0
FEATURE [Part::Extrusion] Extrude002
  Base = -> ShapeString001
  Dir = (1,0,0)
  DirMode = 2
  FaceMakerClass = Part::FaceMakerBullseye
  LengthFwd = -1
  LengthRev = 0
  Solid = false
  Symmetric = false
FEATURE [Part::MultiFuse] Fusion141  label="Logos"
  Placement = pos=(0,0,0.2) rot=(0,0,1;0rad)
  Shapes = -> [Extrude002,Extrude001]
FEATURE [Part::Cut] Cut001002116  label="Caja_Drcha_Logos"
  Base = -> Cut001002113
  Tool = -> Fusion141
FEATURE [Part::Feature] polygon2
  shape: bbox 30 x 23.5 x 2e-07 mm, 0 faces, 0 solids (baked)
FEATURE [Part::Extrusion] Extrude
  Base = -> polygon2
  Dir = (0,0,1)
  DirMode = 2
  FaceMakerClass = Part::FaceMakerBullseye
  LengthFwd = 2
  LengthRev = 0
  Placement = pos=(392,-11,61) rot=(0.57735,0.57735,0.57735;2.0944rad)
  Solid = true
  Symmetric = false
FEATURE [Part::Cut] Cut001002117  label="Caja_Drcha_logo_ull"
  Base = -> Cut001002116
  Tool = -> Extrude
FEATURE [Part::Fillet] Fillet007  label="Caja_Drcha_Fillet"
  Base = -> Cut001002117
  Edges = 2 edges r=6: [Edge39,Edge49]
FEATURE [App::DocumentObjectGroup] Group026  label="Caja Inferior"
  Group = -> [Fillet005,Fillet006,Fillet007]
FEATURE [TechDraw::DrawProjGroupItem] ProjItem030  label="Front008"
  CoarseView = false
  Direction = (-1,0,0)
  Focus = 100
  HardHidden = true
  IsoCount = 0
  IsoHidden = false
  IsoVisible = false
  LockPosition = true
  Perspective = false
  Rotation = 0
  RotationVector = (0,-1,0)
  Scale = 0.75
  ScaleType = 2
  SeamHidden = false
  SeamVisible = true
  SmoothHidden = false
  SmoothVisible = true
  Source = -> [Fillet007]
  Type = 0
  X = 0
  XDirection = (0,-1,0)
  Y = 0
FEATURE [TechDraw::DrawProjGroupItem] ProjItem031  label="Left005"
  CoarseView = false
  Direction = (-1e-16,1,0)
  Focus = 100
  HardHidden = true
  IsoCount = 0
  IsoHidden = false
  IsoVisible = false
  LockPosition = true
  Perspective = false
  Rotation = 0
  RotationVector = (1,0,0)
  ScaleType = 2
  SeamHidden = false
  SeamVisible = true
  SmoothHidden = false
  SmoothVisible = true
  Source = -> [Fillet007]
  Type = 1
  X = 182.21
  XDirection = (-1,-1e-16,0)
  Y = 0
FEATURE [TechDraw::DrawProjGroupItem] ProjItem032  label="Top008"
  CoarseView = false
  Direction = (0,0,1)
  Focus = 100
  HardHidden = false
  IsoCount = 0
  IsoHidden = false
  IsoVisible = false
  LockPosition = true
  Perspective = false
  Rotation = 0
  RotationVector = (1,0,0)
  ScaleType = 2
  SeamHidden = false
  SeamVisible = true
  SmoothHidden = false
  SmoothVisible = true
  Source = -> [Fillet007]
  Type = 4
  X = 0
  XDirection = (0,-1,0)
  Y = -132.5
FEATURE [TechDraw::DrawProjGroup] ProjGroup008
  Anchor = -> ProjItem030
  AutoDistribute = true
  LockPosition = false
  ProjectionType = 0
  Rotation = 0
  Scale = 0.75
  ScaleType = 2
  Views = -> [ProjItem030,ProjItem031,ProjItem032]
  X = 121.988
  Y = 230.5
  spacingX = 15
  spacingY = 15
FEATURE [TechDraw::DrawViewDimension] Dimension156
  Arbitrary = false
  ArbitraryTolerances = false
  EqualTolerance = true
  FormatSpec = %.2f
  FormatSpecOverTolerance = %+.2f
  FormatSpecUnderTolerance = %+.2f
  Inverted = false
  LockPosition = false
  MeasureType = 1
  OverTolerance = 0
  References2D = -> [ProjItem030]
  Rotation = 0
  ScaleType = 0
  TheoreticalExact = false
  Type = 2
  UnderTolerance = 0
  X = 87.7737
  Y = -41.4904
FEATURE [TechDraw::DrawViewDimension] Dimension157
  Arbitrary = false
  ArbitraryTolerances = false
  EqualTolerance = true
  FormatSpec = %.2f
  FormatSpecOverTolerance = %+.2f
  FormatSpecUnderTolerance = %+.2f
  Inverted = false
  LockPosition = false
  MeasureType = 1
  OverTolerance = 0
  References2D = -> [ProjItem030]
  Rotation = 0
  ScaleType = 0
  TheoreticalExact = false
  Type = 2
  UnderTolerance = 0
  X = -91.267
  Y = -44.0825
FEATURE [TechDraw::DrawViewDimension] Dimension158
  Arbitrary = false
  ArbitraryTolerances = false
  EqualTolerance = true
  FormatSpec = %.2f
  FormatSpecOverTolerance = %+.2f
  FormatSpecUnderTolerance = %+.2f
  Inverted = false
  LockPosition = false
  MeasureType = 1
  OverTolerance = 0
  References2D = -> [ProjItem030]
  Rotation = 0
  ScaleType = 0
  TheoreticalExact = false
  Type = 1
  UnderTolerance = 0
  X = -0.354387
  Y = -40.8996
FEATURE [TechDraw::DrawViewDimension] Dimension159
  Arbitrary = false
  ArbitraryTolerances = false
  EqualTolerance = true
  FormatSpec = %.2f
  FormatSpecOverTolerance = %+.2f
  FormatSpecUnderTolerance = %+.2f
  Inverted = false
  LockPosition = false
  MeasureType = 1
  OverTolerance = 0
  References2D = -> [ProjItem030]
  Rotation = 0
  ScaleType = 0
  TheoreticalExact = false
  Type = 1
  UnderTolerance = 0
  X = 0.141755
  Y = -47.2901
FEATURE [TechDraw::DrawViewDimension] Dimension165
  Arbitrary = false
  ArbitraryTolerances = false
  EqualTolerance = true
  FormatSpec = %.2f
  FormatSpecOverTolerance = %+.2f
  FormatSpecUnderTolerance = %+.2f
  Inverted = false
  LockPosition = false
  MeasureType = 1
  OverTolerance = 0
  References2D = -> [ProjItem031]
  Rotation = 0
  ScaleType = 0
  TheoreticalExact = false
  Type = 1
  UnderTolerance = 0
  X = 0.001973
  Y = -9.96829
FEATURE [TechDraw::DrawViewDimension] Dimension178
  Arbitrary = false
  ArbitraryTolerances = false
  EqualTolerance = true
  FormatSpec = ⌀%.2f
  FormatSpecOverTolerance = %+.2f
  FormatSpecUnderTolerance = %+.2f
  Inverted = false
  LockPosition = false
  MeasureType = 1
  OverTolerance = 0
  References2D = -> [ProjItem030]
  Rotation = 0
  ScaleType = 0
  TheoreticalExact = false
  Type = 5
  UnderTolerance = 0
  X = -34.7758
  Y = 10.2009
FEATURE [TechDraw::DrawViewPart] View007
  CoarseView = false
  Direction = (-0.577,0.577,0.577)
  Focus = 100
  HardHidden = true
  IsoCount = 0
  IsoHidden = false
  IsoVisible = false
  LockPosition = true
  Perspective = false
  Rotation = 0
  Scale = 0.4
  ScaleType = 0
  SeamHidden = false
  SeamVisible = true
  SmoothHidden = false
  SmoothVisible = true
  Source = -> [Fillet007]
  X = 308.2
  XDirection = (-0.707,-0.707,0)
  Y = 126.49
FEATURE [Part::FeaturePython] Clone047  label="Extrude003"  # Draft clone (typed FeaturePython)
  AttacherType = Attacher::AttachEngine3D
  Fuse = false
  Objects = -> [Extrude]
  Placement = pos=(170,110,115) rot=(0,0,1;0rad)
  Scale = (1,1,1)
FEATURE [Part::FeaturePython] Clone048  label="Extrude004"  # Draft clone (typed FeaturePython)
  AttacherType = Attacher::AttachEngine3D
  Fuse = false
  Objects = -> [Extrude001]
  Placement = pos=(129,34,-276.7) rot=(0.57735,0.57735,0.57735;4.18879rad)
  Scale = (1,1,1)
FEATURE [Part::MultiFuse] Fusion142  label="logos_tapa"
  Shapes = -> [Clone047,Clone048]
FEATURE [Part::Cut] Cut001002118  label="Tapa_central_logo"
  Base = -> Fillet
  Placement = pos=(0,0,-14) rot=(0,0,1;0rad)
  Tool = -> Fusion142
FEATURE [TechDraw::DrawProjGroupItem] ProjItem039  label="Front011"
  CoarseView = false
  Direction = (0,0,-1)
  Focus = 100
  HardHidden = true
  IsoCount = 0
  IsoHidden = false
  IsoVisible = false
  LockPosition = true
  Perspective = false
  Rotation = 0
  RotationVector = (0,1,0)
  Scale = 0.75
  ScaleType = 2
  SeamHidden = false
  SeamVisible = true
  SmoothHidden = false
  SmoothVisible = true
  Source = -> [Cut001002118]
  Type = 0
  X = 0
  XDirection = (0,1,0)
  Y = 0
FEATURE [TechDraw::DrawProjGroupItem] ProjItem040  label="Top011"
  CoarseView = false
  Direction = (1,0,0)
  Focus = 100
  HardHidden = true
  IsoCount = 0
  IsoHidden = false
  IsoVisible = false
  LockPosition = true
  Perspective = false
  Rotation = 0
  RotationVector = (1,0,0)
  Scale = 0.75
  ScaleType = 2
  SeamHidden = false
  SeamVisible = true
  SmoothHidden = false
  SmoothVisible = true
  Source = -> [Cut001002118]
  Type = 4
  X = 0
  XDirection = (0,1,0)
  Y = -106.883
FEATURE [TechDraw::DrawProjGroupItem] ProjItem041  label="Left008"
  CoarseView = false
  Direction = (0,-1,-1e-16)
  Focus = 100
  HardHidden = true
  IsoCount = 0
  IsoHidden = false
  IsoVisible = false
  LockPosition = true
  Perspective = false
  Rotation = 0
  RotationVector = (1,0,0)
  Scale = 0.75
  ScaleType = 2
  SeamHidden = false
  SeamVisible = true
  SmoothHidden = false
  SmoothVisible = true
  Source = -> [Cut001002118]
  Type = 1
  X = 152.397
  XDirection = (0,1e-16,-1)
  Y = 0
FEATURE [TechDraw::DrawProjGroup] ProjGroup011
  Anchor = -> ProjItem039
  AutoDistribute = true
  LockPosition = false
  ProjectionType = 0
  Rotation = 0
  Scale = 0.75
  ScaleType = 2
  Source = -> [Fillet]
  Views = -> [ProjItem039,ProjItem040,ProjItem041]
  X = 142.699
  Y = 211.145
  spacingX = 15
  spacingY = 15
FEATURE [TechDraw::DrawViewDimension] Dimension214
  Arbitrary = false
  ArbitraryTolerances = false
  EqualTolerance = true
  FormatSpec = R%.2f
  FormatSpecOverTolerance = %+.2f
  FormatSpecUnderTolerance = %+.2f
  Inverted = false
  LockPosition = false
  MeasureType = 1
  OverTolerance = 0
  References2D = -> [ProjItem040]
  Rotation = 0
  ScaleType = 0
  TheoreticalExact = false
  Type = 4
  UnderTolerance = 0
  X = 88.8475
  Y = 16.3965
FEATURE [TechDraw::DrawViewDimension] Dimension216
  Arbitrary = false
  ArbitraryTolerances = false
  EqualTolerance = true
  FormatSpec = R%.2f
  FormatSpecOverTolerance = %+.2f
  FormatSpecUnderTolerance = %+.2f
  Inverted = false
  LockPosition = false
  MeasureType = 1
  OverTolerance = 0
  References2D = -> [ProjItem040]
  Rotation = 0
  ScaleType = 0
  TheoreticalExact = false
  Type = 4
  UnderTolerance = 0
  X = -81.3743
  Y = -12.0901
FEATURE [TechDraw::DrawViewDimension] Dimension218
  Arbitrary = false
  ArbitraryTolerances = false
  EqualTolerance = true
  FormatSpec = %.2f
  FormatSpecOverTolerance = %+.2f
  FormatSpecUnderTolerance = %+.2f
  Inverted = false
  LockPosition = false
  MeasureType = 1
  OverTolerance = 0
  References2D = -> [ProjItem040]
  Rotation = 0
  ScaleType = 0
  TheoreticalExact = false
  Type = 2
  UnderTolerance = 0
  X = -67.8463
  Y = -13.0641
FEATURE [TechDraw::DrawViewPart] View010
  CoarseView = false
  Direction = (0.577,-0.577,0.577)
  Focus = 100
  HardHidden = false
  IsoCount = 0
  IsoHidden = false
  IsoVisible = false
  LockPosition = true
  Perspective = false
  Rotation = 0
  Scale = 0.4
  ScaleType = 0
  SeamHidden = false
  SeamVisible = true
  SmoothHidden = false
  SmoothVisible = false
  Source = -> [Cut001002118]
  X = 334.206
  XDirection = (0.707,0.707,0)
  Y = 112.812
FEATURE [Part::Part2DObjectPython] ShapeString002  # Draft 2D object (typed FeaturePython)
  FontFile = <userpath>/Documents/tfm_augusto/Mecanica/Caja_bateria/logos/Staatliches-Regular.ttf
  Placement = pos=(2.33,143.28,117) rot=(0,0,1;0rad)
  Size = 12
  String = -
  Tracking = 0
FEATURE [Part::Part2DObjectPython] ShapeString003  # Draft 2D object (typed FeaturePython)
  FontFile = <userpath>/Documents/tfm_augusto/Mecanica/Caja_bateria/logos/Staatliches-Regular.ttf
  Placement = pos=(353.33,143.28,117) rot=(0,0,1;0rad)
  Size = 12
  String = +
  Tracking = 0
FEATURE [Part::Extrusion] Extrude003  label="Extrude005"
  Base = -> ShapeString002
  Dir = (0,0,1)
  DirMode = 2
  FaceMakerClass = Part::FaceMakerBullseye
  LengthFwd = -2
  LengthRev = 0
  Solid = false
  Symmetric = false
FEATURE [Part::Extrusion] Extrude004  label="Extrude006"
  Base = -> ShapeString003
  Dir = (0,0,1)
  DirMode = 2
  FaceMakerClass = Part::FaceMakerBullseye
  LengthFwd = -2
  LengthRev = 0
  Solid = false
  Symmetric = false
FEATURE [Part::Cut] Cut001002119  label="Tapa_Drcha_Polo"
  Base = -> Cut001002115
  Placement = pos=(0,0,-14) rot=(0,0,1;0rad)
  Tool = -> Extrude004
FEATURE [Part::Cut] Cut001002120  label="Tapa_Izquierda_Polo"
  Base = -> Cut001002114
  Placement = pos=(0,0,-14) rot=(0,0,1;0rad)
  Tool = -> Extrude003
FEATURE [App::DocumentObjectGroup] Group027  label="Tapa Caja"
  Group = -> [Cut001002118,Cut001002119,Cut001002120]
FEATURE [TechDraw::DrawSVGTemplate] Template013
  EditableTexts = A3=A3; AUTHOR_NAME=AUTHOR NAME; A__=_________; B__=_________; CHECK_DATE=CHECK DATE; CREATION_DATE=CREATION DATE; C__=_________; D__=_________; E__=_________; F__=_________; G__=_________; H__=_________; I__=_________; SCALE=SCALE; SHEET=SHEET; SUBTITLE=SUBTITLE; SUPERVISOR_NAME=SUPERVISOR NAME; TITLE=TITLE; VERSION=VERSION; WEIGHT=WEIGHT
  Height = 297
  Orientation = 1
  Width = 420
FEATURE [TechDraw::DrawPage] Page014
  KeepUpdated = true
  NextBalloonIndex = 1
  ProjectionType = 0
  Template = -> Template013
FEATURE [TechDraw::DrawViewSymbol] Symbol
  LockPosition = false
  Rotation = 0
  ScaleType = 2
  Symbol = <blob: 387326 chars omitted>
  X = 307.063
  Y = 32.981
FEATURE [TechDraw::DrawViewSymbol] Symbol001
  LockPosition = false
  Rotation = 0
  ScaleType = 2
  Symbol = <blob: 387326 chars omitted>
  X = 305.354
  Y = 32.6392
FEATURE [TechDraw::DrawPage] Page003  label="Pletina_cobre"
  KeepUpdated = true
  NextBalloonIndex = 2
  ProjectionType = 0
  Template = -> Template002
  Views = -> [ProjGroup002,Dimension025,Dimension026,Dimension027,Dimension028,Dimension029,Dimension030,Symbol001]
FEATURE [TechDraw::DrawViewSymbol] Symbol002
  LockPosition = false
  Rotation = 0
  ScaleType = 2
  Symbol = <blob: 387326 chars omitted>
  X = 306.593
  Y = 32.4383
FEATURE [TechDraw::DrawPage] Page004  label="Tapeta_lat_izda"
  KeepUpdated = true
  NextBalloonIndex = 1
  ProjectionType = 0
  Template = -> Template003
  Views = -> [ProjGroup003,View003,Dimension031,Dimension032,Dimension033,Dimension034,Dimension035,Dimension036,Dimension037,Dimension038,Dimension039,Dimension040,Dimension043,SectionView,Dimension046,Dimension047,Dimension048,Dimension049,Dimension051,Dimension052,Dimension053,Annotation,Symbol002]
FEATURE [TechDraw::DrawViewSymbol] Symbol003
  LockPosition = false
  Rotation = 0
  ScaleType = 2
  Symbol = <blob: 387326 chars omitted>
  X = 305.981
  Y = 32.8671
FEATURE [TechDraw::DrawPage] Page005  label="Tapeta_lat_drcha"
  KeepUpdated = true
  NextBalloonIndex = 1
  ProjectionType = 0
  Template = -> Template004
  Views = -> [ProjGroup004,SectionView001,Dimension055,Dimension056,Dimension057,Dimension058,Dimension059,Dimension061,Dimension062,Dimension063,Dimension064,Dimension065,Dimension066,Dimension067,Dimension068,Dimension069,Dimension070,Dimension071,Dimension072,Dimension073,Dimension075,Dimension076,Dimension077,Dimension078,View004,Annotation001,Dimension079,Symbol003]
FEATURE [TechDraw::DrawViewDimension] Dimension
  Arbitrary = false
  ArbitraryTolerances = false
  EqualTolerance = true
  FormatSpec = %.2f
  FormatSpecOverTolerance = %+.2f
  FormatSpecUnderTolerance = %+.2f
  Inverted = false
  LockPosition = false
  MeasureType = 1
  OverTolerance = 0
  References2D = -> [ProjItem044]
  Rotation = 0
  ScaleType = 0
  TheoreticalExact = false
  Type = 1
  UnderTolerance = 0
  X = -0.557833
  Y = -51.3944
FEATURE [TechDraw::DrawViewDimension] Dimension220
  Arbitrary = false
  ArbitraryTolerances = false
  EqualTolerance = true
  FormatSpec = %.2f
  FormatSpecOverTolerance = %+.2f
  FormatSpecUnderTolerance = %+.2f
  Inverted = false
  LockPosition = false
  MeasureType = 1
  OverTolerance = 0
  References2D = -> [ProjItem043]
  Rotation = 0
  ScaleType = 0
  TheoreticalExact = false
  Type = 1
  UnderTolerance = 0
  X = 1.20046
  Y = -24.1014
FEATURE [TechDraw::DrawViewDimension] Dimension221
  Arbitrary = false
  ArbitraryTolerances = false
  EqualTolerance = true
  FormatSpec = %.2f
  FormatSpecOverTolerance = %+.2f
  FormatSpecUnderTolerance = %+.2f
  Inverted = false
  LockPosition = false
  MeasureType = 1
  OverTolerance = 0
  References2D = -> [ProjItem043]
  Rotation = 0
  ScaleType = 0
  TheoreticalExact = false
  Type = 2
  UnderTolerance = 0
  X = 53.3191
  Y = 0
FEATURE [TechDraw::DrawViewSymbol] Symbol004
  LockPosition = false
  Rotation = 0
  ScaleType = 2
  Symbol = <blob: 387326 chars omitted>
  X = 305.06
  Y = 32.9364
FEATURE [TechDraw::DrawPage] Page013  label="estructura_bateria_general"
  KeepUpdated = true
  NextBalloonIndex = 7
  ProjectionType = 0
  Template = -> Template012
  Views = -> [ProjGroup012,Balloon006,Balloon007,Balloon008,Balloon009,Balloon010,View012,Sheet,Dimension,Dimension220,Dimension221,Symbol004]
FEATURE [TechDraw::DrawProjGroupItem] ProjItem015  label="Front005"
  CoarseView = false
  Direction = (0,-1,0)
  Focus = 100
  HardHidden = false
  IsoCount = 0
  IsoHidden = false
  IsoVisible = false
  LockPosition = true
  Perspective = false
  Rotation = 0
  RotationVector = (1,0,0)
  Scale = 0.25
  ScaleType = 2
  SeamHidden = false
  SeamVisible = true
  SmoothHidden = false
  SmoothVisible = true
  Source = -> [Group027,Group026]
  Type = 0
  X = 0
  XDirection = (1,0,0)
  Y = 0
FEATURE [TechDraw::DrawProjGroupItem] ProjItem016  label="Right"
  CoarseView = false
  Direction = (1,-1e-16,0)
  Focus = 100
  HardHidden = false
  IsoCount = 0
  IsoHidden = false
  IsoVisible = false
  LockPosition = true
  Perspective = false
  Rotation = 0
  RotationVector = (1,0,0)
  Scale = 0.25
  ScaleType = 2
  SeamHidden = false
  SeamVisible = true
  SmoothHidden = false
  SmoothVisible = true
  Source = -> [Fillet005,Fillet006,Fillet007,Cut001002118,Cut001002119,Cut001002120]
  Type = 2
  X = -99.572
  XDirection = (1e-16,1,0)
  Y = 0
FEATURE [TechDraw::DrawProjGroupItem] ProjItem017  label="Left002"
  CoarseView = false
  Direction = (-1,-1e-16,0)
  Focus = 100
  HardHidden = false
  IsoCount = 0
  IsoHidden = false
  IsoVisible = false
  LockPosition = true
  Perspective = false
  Rotation = 0
  RotationVector = (1,0,0)
  Scale = 0.25
  ScaleType = 2
  SeamHidden = false
  SeamVisible = true
  SmoothHidden = false
  SmoothVisible = true
  Source = -> [Group027,Group026]
  Type = 1
  X = 99.572
  XDirection = (1e-16,-1,0)
  Y = 0
FEATURE [TechDraw::DrawViewDimension] Dimension085
  Arbitrary = false
  ArbitraryTolerances = false
  EqualTolerance = true
  FormatSpec = %.2f
  FormatSpecOverTolerance = %+.2f
  FormatSpecUnderTolerance = %+.2f
  Inverted = false
  LockPosition = false
  MeasureType = 1
  OverTolerance = 0
  References2D = -> [ProjItem017]
  Rotation = 0
  ScaleType = 0
  TheoreticalExact = false
  Type = 2
  UnderTolerance = 0
  X = 26.4
  Y = 13.75
FEATURE [TechDraw::DrawProjGroupItem] ProjItem021  label="FrontTopRight"
  CoarseView = false
  Direction = (0.57735,-0.57735,0.57735)
  Focus = 100
  HardHidden = false
  IsoCount = 0
  IsoHidden = false
  IsoVisible = false
  LockPosition = true
  Perspective = false
  Rotation = 0
  RotationVector = (1,0,0)
  Scale = 0.25
  ScaleType = 2
  SeamHidden = false
  SeamVisible = false
  SmoothHidden = true
  SmoothVisible = false
  Source = -> [Group027,Group026]
  Type = 7
  X = -128.002
  XDirection = (0.707107,0.707107,0)
  Y = -91.6357
FEATURE [TechDraw::DrawProjGroupItem] ProjItem022  label="Top005"
  CoarseView = false
  Direction = (0,0,1)
  Focus = 100
  HardHidden = false
  IsoCount = 0
  IsoHidden = false
  IsoVisible = false
  LockPosition = true
  Perspective = false
  Rotation = 0
  RotationVector = (1,0,0)
  Scale = 0.25
  ScaleType = 2
  SeamHidden = false
  SeamVisible = true
  SmoothHidden = false
  SmoothVisible = true
  Source = -> [Group027,Group026]
  Type = 4
  X = 0
  XDirection = (1,0,0)
  Y = -95.8122
FEATURE [TechDraw::DrawProjGroupItem] ProjItem023  label="FrontTopLeft001"
  CoarseView = false
  Direction = (-0.57735,-0.57735,0.57735)
  Focus = 100
  HardHidden = true
  IsoCount = 0
  IsoHidden = false
  IsoVisible = false
  LockPosition = true
  Perspective = false
  Rotation = 0
  RotationVector = (1,0,0)
  Scale = 0.25
  ScaleType = 2
  SeamHidden = false
  SeamVisible = true
  SmoothHidden = false
  SmoothVisible = true
  Source = -> [Group027,Group026]
  Type = 6
  X = 126.293
  XDirection = (0.707107,-0.707107,0)
  Y = -98.8129
FEATURE [TechDraw::DrawProjGroup] ProjGroup005
  Anchor = -> ProjItem015
  AutoDistribute = true
  LockPosition = false
  ProjectionType = 0
  Rotation = 0
  Scale = 0.25
  ScaleType = 2
  Source = -> [Group027,Group026]
  Views = -> [ProjItem015,ProjItem016,ProjItem017,ProjItem021,ProjItem022,ProjItem023]
  X = 212.024
  Y = 237.48
  spacingX = 15
  spacingY = 15
FEATURE [TechDraw::DrawViewSymbol] Symbol005
  LockPosition = false
  Rotation = 0
  ScaleType = 2
  Symbol = <blob: 387326 chars omitted>
  X = 306.263
  Y = 33.5323
FEATURE [TechDraw::DrawPage] Page007  label="Caja_bateria_izda"
  KeepUpdated = true
  NextBalloonIndex = 1
  ProjectionType = 0
  Template = -> Template006
  Views = -> [ProjGroup006,Dimension086,Dimension087,Dimension088,Dimension089,Dimension090,Dimension091,Dimension092,Dimension093,Dimension094,Dimension095,Dimension096,Dimension097,Dimension098,Dimension099,Dimension100,Dimension101,Dimension102,Dimension103,Dimension104,Dimension105,Dimension106,Dimension107,Dimension108,Dimension110,View005,Dimension111,Dimension153,Symbol005]
FEATURE [TechDraw::DrawViewSymbol] Symbol006
  LockPosition = false
  Rotation = 0
  ScaleType = 2
  Symbol = <blob: 387326 chars omitted>
  X = 306.438
  Y = 33.1941
FEATURE [TechDraw::DrawPage] Page011  label="tapa_izda_caja_bateria"
  KeepUpdated = true
  NextBalloonIndex = 1
  ProjectionType = 0
  Template = -> Template010
  Views = -> [ProjGroup010,Dimension190,Dimension191,Dimension192,Dimension193,Dimension194,Dimension195,Dimension197,Dimension198,Dimension199,Dimension200,Dimension201,Dimension202,View009,Symbol006]
FEATURE [TechDraw::DrawViewDimension] Dimension222
  Arbitrary = false
  ArbitraryTolerances = false
  EqualTolerance = true
  FormatSpec = ⌀%.2f
  FormatSpecOverTolerance = %+.2f
  FormatSpecUnderTolerance = %+.2f
  Inverted = false
  LockPosition = false
  MeasureType = 1
  OverTolerance = 0
  References2D = -> [ProjItem039]
  Rotation = 0
  ScaleType = 0
  TheoreticalExact = false
  Type = 5
  UnderTolerance = 0
  X = -70.6327
  Y = -23.1726
FEATURE [TechDraw::DrawViewDimension] Dimension223
  Arbitrary = false
  ArbitraryTolerances = false
  EqualTolerance = true
  FormatSpec = %.2f
  FormatSpecOverTolerance = %+.2f
  FormatSpecUnderTolerance = %+.2f
  Inverted = false
  LockPosition = false
  MeasureType = 1
  OverTolerance = 0
  References2D = -> [ProjItem039]
  Rotation = 0
  ScaleType = 0
  TheoreticalExact = false
  Type = 1
  UnderTolerance = 0
  X = -94.8834
  Y = -48.2789
FEATURE [TechDraw::DrawViewDimension] Dimension224
  Arbitrary = false
  ArbitraryTolerances = false
  EqualTolerance = true
  FormatSpec = %.1f
  FormatSpecOverTolerance = %+.2f
  FormatSpecUnderTolerance = %+.2f
  Inverted = false
  LockPosition = false
  MeasureType = 1
  OverTolerance = 0
  References2D = -> [ProjItem039]
  Rotation = 0
  ScaleType = 0
  TheoreticalExact = false
  Type = 2
  UnderTolerance = 0
  X = 89.2821
  Y = -51.0755
FEATURE [TechDraw::DrawViewDimension] Dimension225
  Arbitrary = false
  ArbitraryTolerances = false
  EqualTolerance = true
  FormatSpec = %.2f
  FormatSpecOverTolerance = %+.2f
  FormatSpecUnderTolerance = %+.2f
  Inverted = false
  LockPosition = false
  MeasureType = 1
  OverTolerance = 0
  References2D = -> [ProjItem039]
  Rotation = 0
  ScaleType = 0
  TheoreticalExact = false
  Type = 1
  UnderTolerance = 0
  X = 63.6477
  Y = 33.4553
FEATURE [TechDraw::DrawViewDimension] Dimension226
  Arbitrary = false
  ArbitraryTolerances = false
  EqualTolerance = true
  FormatSpec = %.1f
  FormatSpecOverTolerance = %+.2f
  FormatSpecUnderTolerance = %+.2f
  Inverted = false
  LockPosition = false
  MeasureType = 1
  OverTolerance = 0
  References2D = -> [ProjItem039]
  Rotation = 0
  ScaleType = 0
  TheoreticalExact = false
  Type = 1
  UnderTolerance = 0
  X = 96.3857
  Y = 63.1187
FEATURE [TechDraw::DrawViewDimension] Dimension227
  Arbitrary = false
  ArbitraryTolerances = false
  EqualTolerance = true
  FormatSpec = %.2f
  FormatSpecOverTolerance = %+.2f
  FormatSpecUnderTolerance = %+.2f
  Inverted = false
  LockPosition = false
  MeasureType = 1
  OverTolerance = 0
  References2D = -> [ProjItem039]
  Rotation = 0
  ScaleType = 0
  TheoreticalExact = false
  Type = 2
  UnderTolerance = 0
  X = -65.8821
  Y = 28.8715
FEATURE [TechDraw::DrawViewDimension] Dimension228
  Arbitrary = false
  ArbitraryTolerances = false
  EqualTolerance = true
  FormatSpec = %.2f
  FormatSpecOverTolerance = %+.2f
  FormatSpecUnderTolerance = %+.2f
  Inverted = false
  LockPosition = false
  MeasureType = 1
  OverTolerance = 0
  References2D = -> [ProjItem041]
  Rotation = 0
  ScaleType = 0
  TheoreticalExact = false
  Type = 2
  UnderTolerance = 0
  X = -14.4971
  Y = 62.7379
FEATURE [TechDraw::DrawViewDimension] Dimension229
  Arbitrary = false
  ArbitraryTolerances = false
  EqualTolerance = true
  FormatSpec = %.2f
  FormatSpecOverTolerance = %+.2f
  FormatSpecUnderTolerance = %+.2f
  Inverted = false
  LockPosition = false
  MeasureType = 1
  OverTolerance = 0
  References2D = -> [ProjItem041]
  Rotation = 0
  ScaleType = 0
  TheoreticalExact = false
  Type = 1
  UnderTolerance = 0
  X = 17.7535
  Y = -58.153
FEATURE [TechDraw::DrawViewDimension] Dimension230
  Arbitrary = false
  ArbitraryTolerances = false
  EqualTolerance = true
  FormatSpec = %.2f
  FormatSpecOverTolerance = %+.2f
  FormatSpecUnderTolerance = %+.2f
  Inverted = false
  LockPosition = false
  MeasureType = 1
  OverTolerance = 0
  References2D = -> [ProjItem041]
  Rotation = 0
  ScaleType = 0
  TheoreticalExact = false
  Type = 1
  UnderTolerance = 0
  X = -12.9105
  Y = -51.5293
FEATURE [TechDraw::DrawViewDimension] Dimension231
  Arbitrary = false
  ArbitraryTolerances = false
  EqualTolerance = true
  FormatSpec = %.2f
  FormatSpecOverTolerance = %+.2f
  FormatSpecUnderTolerance = %+.2f
  Inverted = false
  LockPosition = false
  MeasureType = 1
  OverTolerance = 0
  References2D = -> [ProjItem041]
  Rotation = 0
  ScaleType = 0
  TheoreticalExact = false
  Type = 2
  UnderTolerance = 0
  X = 10.2057
  Y = 2.4593
FEATURE [TechDraw::DrawViewSymbol] Symbol007
  LockPosition = false
  Rotation = 0
  ScaleType = 2
  Symbol = <blob: 387326 chars omitted>
  X = 305.27
  Y = 33.1731
FEATURE [TechDraw::DrawViewSymbol] Symbol008
  LockPosition = false
  Rotation = 0
  ScaleType = 2
  Symbol = <blob: 387326 chars omitted>
  X = 305.04
  Y = 32.8447
FEATURE [TechDraw::DrawPage] Page010  label="tapa_drcha_caja_bateria"
  KeepUpdated = true
  NextBalloonIndex = 1
  ProjectionType = 0
  Template = -> Template009
  Views = -> [ProjGroup009,Dimension179,Dimension180,Dimension181,Dimension182,Dimension183,Dimension184,Dimension185,Dimension186,Dimension187,Dimension188,Dimension189,View008,Dimension196,Symbol008]
FEATURE [TechDraw::DrawViewDimension] Dimension232
  Arbitrary = false
  ArbitraryTolerances = false
  EqualTolerance = true
  FormatSpec = %.2f
  FormatSpecOverTolerance = %+.2f
  FormatSpecUnderTolerance = %+.2f
  Inverted = false
  LockPosition = false
  MeasureType = 1
  OverTolerance = 0
  References2D = -> [ProjItem039]
  Rotation = 0
  ScaleType = 0
  TheoreticalExact = false
  Type = 1
  UnderTolerance = 0
  X = 0.633795
  Y = -54.0157
FEATURE [TechDraw::DrawPage] Page012  label="tapa_central_caja_bateria"
  KeepUpdated = true
  NextBalloonIndex = 1
  ProjectionType = 0
  Template = -> Template011
  Views = -> [ProjGroup011,Dimension214,Dimension216,Dimension218,View010,Dimension222,Dimension223,Dimension224,Dimension225,Dimension226,Dimension227,Dimension228,Dimension229,Dimension230,Dimension231,Symbol007,Dimension232]
FEATURE [TechDraw::DrawViewDimension] Dimension233
  Arbitrary = false
  ArbitraryTolerances = false
  EqualTolerance = true
  FormatSpec = %.2f
  FormatSpecOverTolerance = %+.2f
  FormatSpecUnderTolerance = %+.2f
  Inverted = false
  LockPosition = false
  MeasureType = 1
  OverTolerance = 0
  References2D = -> [ProjItem027]
  Rotation = 0
  ScaleType = 0
  TheoreticalExact = false
  Type = 1
  UnderTolerance = 0
  X = 2.56771
  Y = 48.9561
FEATURE [TechDraw::DrawViewDimension] Dimension234
  Arbitrary = false
  ArbitraryTolerances = false
  EqualTolerance = true
  FormatSpec = %.2f
  FormatSpecOverTolerance = %+.2f
  FormatSpecUnderTolerance = %+.2f
  Inverted = false
  LockPosition = false
  MeasureType = 1
  OverTolerance = 0
  References2D = -> [ProjItem029]
  Rotation = 0
  ScaleType = 0
  TheoreticalExact = false
  Type = 2
  UnderTolerance = 0
  X = -67.5597
  Y = 2.36535
FEATURE [TechDraw::DrawViewDimension] Dimension235
  Arbitrary = false
  ArbitraryTolerances = false
  EqualTolerance = true
  FormatSpec = %.2f
  FormatSpecOverTolerance = %+.2f
  FormatSpecUnderTolerance = %+.2f
  Inverted = false
  LockPosition = false
  MeasureType = 1
  OverTolerance = 0
  References2D = -> [ProjItem029]
  Rotation = 0
  ScaleType = 0
  TheoreticalExact = false
  Type = 2
  UnderTolerance = 0
  X = -59.9172
  Y = 11.2325
FEATURE [TechDraw::DrawViewDimension] Dimension236
  Arbitrary = false
  ArbitraryTolerances = false
  EqualTolerance = true
  FormatSpec = %.2f
  FormatSpecOverTolerance = %+.2f
  FormatSpecUnderTolerance = %+.2f
  Inverted = false
  LockPosition = false
  MeasureType = 1
  OverTolerance = 0
  References2D = -> [ProjItem029]
  Rotation = 0
  ScaleType = 0
  TheoreticalExact = false
  Type = 1
  UnderTolerance = 0
  X = -25.7297
  Y = 48.4883
FEATURE [TechDraw::DrawViewDimension] Dimension237
  Arbitrary = false
  ArbitraryTolerances = false
  EqualTolerance = true
  FormatSpec = %.2f
  FormatSpecOverTolerance = %+.2f
  FormatSpecUnderTolerance = %+.2f
  Inverted = false
  LockPosition = false
  MeasureType = 1
  OverTolerance = 0
  References2D = -> [ProjItem029]
  Rotation = 0
  ScaleType = 0
  TheoreticalExact = false
  Type = 2
  UnderTolerance = 0
  X = -30.4226
  Y = 22.3208
FEATURE [TechDraw::DrawViewDimension] Dimension238
  Arbitrary = false
  ArbitraryTolerances = false
  EqualTolerance = true
  FormatSpec = %.2f
  FormatSpecOverTolerance = %+.2f
  FormatSpecUnderTolerance = %+.2f
  Inverted = false
  LockPosition = false
  MeasureType = 1
  OverTolerance = 0
  References2D = -> [ProjItem029]
  Rotation = 0
  ScaleType = 0
  TheoreticalExact = false
  Type = 2
  UnderTolerance = 0
  X = 26.2894
  Y = 15.7025
FEATURE [TechDraw::DrawViewDimension] Dimension239
  Arbitrary = false
  ArbitraryTolerances = false
  EqualTolerance = true
  FormatSpec = %.2f
  FormatSpecOverTolerance = %+.2f
  FormatSpecUnderTolerance = %+.2f
  Inverted = false
  LockPosition = false
  MeasureType = 1
  OverTolerance = 0
  References2D = -> [ProjItem029]
  Rotation = 0
  ScaleType = 0
  TheoreticalExact = false
  Type = 1
  UnderTolerance = 0
  X = 63.5888
  Y = -37.0383
FEATURE [TechDraw::DrawViewDimension] Dimension240
  Arbitrary = false
  ArbitraryTolerances = false
  EqualTolerance = true
  FormatSpec = %.2f
  FormatSpecOverTolerance = %+.2f
  FormatSpecUnderTolerance = %+.2f
  Inverted = false
  LockPosition = false
  MeasureType = 1
  OverTolerance = 0
  References2D = -> [ProjItem028]
  Rotation = 0
  ScaleType = 0
  TheoreticalExact = false
  Type = 2
  UnderTolerance = 0
  X = 33.1537
  Y = -26.175
FEATURE [TechDraw::DrawViewDimension] Dimension241
  Arbitrary = false
  ArbitraryTolerances = false
  EqualTolerance = true
  FormatSpec = %.2f
  FormatSpecOverTolerance = %+.2f
  FormatSpecUnderTolerance = %+.2f
  Inverted = false
  LockPosition = false
  MeasureType = 1
  OverTolerance = 0
  References2D = -> [ProjItem028]
  Rotation = 0
  ScaleType = 0
  TheoreticalExact = false
  Type = 2
  UnderTolerance = 0
  X = 33.1537
  Y = 5.89271
FEATURE [TechDraw::DrawViewDimension] Dimension242
  Arbitrary = false
  ArbitraryTolerances = false
  EqualTolerance = true
  FormatSpec = %.2f
  FormatSpecOverTolerance = %+.2f
  FormatSpecUnderTolerance = %+.2f
  Inverted = false
  LockPosition = false
  MeasureType = 1
  OverTolerance = 0
  References2D = -> [ProjItem028]
  Rotation = 0
  ScaleType = 0
  TheoreticalExact = false
  Type = 2
  UnderTolerance = 0
  X = 33.2364
  Y = 40.9076
FEATURE [TechDraw::DrawViewDimension] Dimension243
  Arbitrary = false
  ArbitraryTolerances = false
  EqualTolerance = true
  FormatSpec = %.2f
  FormatSpecOverTolerance = %+.2f
  FormatSpecUnderTolerance = %+.2f
  Inverted = false
  LockPosition = false
  MeasureType = 1
  OverTolerance = 0
  References2D = -> [ProjItem028]
  Rotation = 0
  ScaleType = 0
  TheoreticalExact = false
  Type = 1
  UnderTolerance = 0
  X = -62.25
  Y = 29.8927
FEATURE [TechDraw::DrawViewDimension] Dimension244
  Arbitrary = false
  ArbitraryTolerances = false
  EqualTolerance = true
  FormatSpec = ⌀%.2f
  FormatSpecOverTolerance = %+.2f
  FormatSpecUnderTolerance = %+.2f
  Inverted = false
  LockPosition = false
  MeasureType = 1
  OverTolerance = 0
  References2D = -> [ProjItem028]
  Rotation = 0
  ScaleType = 0
  TheoreticalExact = false
  Type = 5
  UnderTolerance = 0
  X = -35.893
  Y = 64.0947
FEATURE [TechDraw::DrawViewDimension] Dimension245
  Arbitrary = false
  ArbitraryTolerances = false
  EqualTolerance = true
  FormatSpec = %.2f
  FormatSpecOverTolerance = %+.2f
  FormatSpecUnderTolerance = %+.2f
  Inverted = false
  LockPosition = false
  MeasureType = 1
  OverTolerance = 0
  References2D = -> [ProjItem028]
  Rotation = 0
  ScaleType = 0
  TheoreticalExact = false
  Type = 1
  UnderTolerance = 0
  X = 64.5626
  Y = -25.0352
FEATURE [TechDraw::DrawViewDimension] Dimension246
  Arbitrary = false
  ArbitraryTolerances = false
  EqualTolerance = true
  FormatSpec = %.2f
  FormatSpecOverTolerance = %+.2f
  FormatSpecUnderTolerance = %+.2f
  Inverted = false
  LockPosition = false
  MeasureType = 1
  OverTolerance = 0
  References2D = -> [ProjItem028]
  Rotation = 0
  ScaleType = 0
  TheoreticalExact = false
  Type = 2
  UnderTolerance = 0
  X = 89.9882
  Y = -53.4504
FEATURE [TechDraw::DrawViewDimension] Dimension247
  Arbitrary = false
  ArbitraryTolerances = false
  EqualTolerance = true
  FormatSpec = %.2f
  FormatSpecOverTolerance = %+.2f
  FormatSpecUnderTolerance = %+.2f
  Inverted = false
  LockPosition = false
  MeasureType = 1
  OverTolerance = 0
  References2D = -> [ProjItem028]
  Rotation = 0
  ScaleType = 0
  TheoreticalExact = false
  Type = 2
  UnderTolerance = 0
  X = -67.2982
  Y = -63.0585
FEATURE [TechDraw::DrawViewDimension] Dimension248
  Arbitrary = false
  ArbitraryTolerances = false
  EqualTolerance = true
  FormatSpec = %.2f
  FormatSpecOverTolerance = %+.2f
  FormatSpecUnderTolerance = %+.2f
  Inverted = false
  LockPosition = false
  MeasureType = 1
  OverTolerance = 0
  References2D = -> [ProjItem028]
  Rotation = 0
  ScaleType = 0
  TheoreticalExact = false
  Type = 2
  UnderTolerance = 0
  X = -92.3593
  Y = 0.932286
FEATURE [TechDraw::DrawViewDimension] Dimension249
  Arbitrary = false
  ArbitraryTolerances = false
  EqualTolerance = true
  FormatSpec = %.2f
  FormatSpecOverTolerance = %+.2f
  FormatSpecUnderTolerance = %+.2f
  Inverted = false
  LockPosition = false
  MeasureType = 1
  OverTolerance = 0
  References2D = -> [ProjItem028]
  Rotation = 0
  ScaleType = 0
  TheoreticalExact = false
  Type = 2
  UnderTolerance = 0
  X = 66.205
  Y = 26.2058
FEATURE [TechDraw::DrawViewDimension] Dimension250
  Arbitrary = false
  ArbitraryTolerances = false
  EqualTolerance = true
  FormatSpec = %.2f
  FormatSpecOverTolerance = %+.2f
  FormatSpecUnderTolerance = %+.2f
  Inverted = false
  LockPosition = false
  MeasureType = 1
  OverTolerance = 0
  References2D = -> [ProjItem027]
  Rotation = 0
  ScaleType = 0
  TheoreticalExact = false
  Type = 1
  UnderTolerance = 0
  X = -1.86889
  Y = -47.796
FEATURE [TechDraw::DrawViewDimension] Dimension251
  Arbitrary = false
  ArbitraryTolerances = false
  EqualTolerance = true
  FormatSpec = %.2f
  FormatSpecOverTolerance = %+.2f
  FormatSpecUnderTolerance = %+.2f
  Inverted = false
  LockPosition = false
  MeasureType = 1
  OverTolerance = 0
  References2D = -> [ProjItem027]
  Rotation = 0
  ScaleType = 0
  TheoreticalExact = false
  Type = 1
  UnderTolerance = 0
  X = 0.415309
  Y = -41.0582
FEATURE [TechDraw::DrawViewDimension] Dimension252
  Arbitrary = false
  ArbitraryTolerances = false
  EqualTolerance = true
  FormatSpec = %.2f
  FormatSpecOverTolerance = %+.2f
  FormatSpecUnderTolerance = %+.2f
  Inverted = false
  LockPosition = false
  MeasureType = 1
  OverTolerance = 0
  References2D = -> [ProjItem027]
  Rotation = 0
  ScaleType = 0
  TheoreticalExact = false
  Type = 2
  UnderTolerance = 0
  X = 87.1832
  Y = -43.1006
FEATURE [TechDraw::DrawViewSymbol] Symbol009
  LockPosition = false
  Rotation = 0
  ScaleType = 2
  Symbol = <blob: 387326 chars omitted>
  X = 305.849
  Y = 32.8451
FEATURE [TechDraw::DrawViewDimension] Dimension253
  Arbitrary = false
  ArbitraryTolerances = false
  EqualTolerance = true
  FormatSpec = %.2f
  FormatSpecOverTolerance = %+.2f
  FormatSpecUnderTolerance = %+.2f
  Inverted = false
  LockPosition = false
  MeasureType = 1
  OverTolerance = 0
  References2D = -> [ProjItem030]
  Rotation = 0
  ScaleType = 0
  TheoreticalExact = false
  Type = 2
  UnderTolerance = 0
  X = -90.6155
  Y = 32.7323
FEATURE [TechDraw::DrawViewDimension] Dimension254
  Arbitrary = false
  ArbitraryTolerances = false
  EqualTolerance = true
  FormatSpec = %.2f
  FormatSpecOverTolerance = %+.2f
  FormatSpecUnderTolerance = %+.2f
  Inverted = false
  LockPosition = false
  MeasureType = 1
  OverTolerance = 0
  References2D = -> [ProjItem030]
  Rotation = 0
  ScaleType = 0
  TheoreticalExact = false
  Type = 1
  UnderTolerance = 0
  X = -63.8861
  Y = 46.4669
FEATURE [TechDraw::DrawViewDimension] Dimension255
  Arbitrary = false
  ArbitraryTolerances = false
  EqualTolerance = true
  FormatSpec = %.2f
  FormatSpecOverTolerance = %+.2f
  FormatSpecUnderTolerance = %+.2f
  Inverted = false
  LockPosition = false
  MeasureType = 1
  OverTolerance = 0
  References2D = -> [ProjItem030]
  Rotation = 0
  ScaleType = 0
  TheoreticalExact = false
  Type = 2
  UnderTolerance = 0
  X = 86.6371
  Y = 22.6631
FEATURE [TechDraw::DrawViewDimension] Dimension256
  Arbitrary = false
  ArbitraryTolerances = false
  EqualTolerance = true
  FormatSpec = %.2f
  FormatSpecOverTolerance = %+.2f
  FormatSpecUnderTolerance = %+.2f
  Inverted = false
  LockPosition = false
  MeasureType = 1
  OverTolerance = 0
  References2D = -> [ProjItem031]
  Rotation = 0
  ScaleType = 0
  TheoreticalExact = false
  Type = 2
  UnderTolerance = 0
  X = 63.5175
  Y = -12.9817
FEATURE [TechDraw::DrawViewDimension] Dimension257
  Arbitrary = false
  ArbitraryTolerances = false
  EqualTolerance = true
  FormatSpec = %.2f
  FormatSpecOverTolerance = %+.2f
  FormatSpecUnderTolerance = %+.2f
  Inverted = false
  LockPosition = false
  MeasureType = 1
  OverTolerance = 0
  References2D = -> [ProjItem031]
  Rotation = 0
  ScaleType = 0
  TheoreticalExact = false
  Type = 2
  UnderTolerance = 0
  X = 63.628
  Y = 10.8948
FEATURE [TechDraw::DrawViewDimension] Dimension258
  Arbitrary = false
  ArbitraryTolerances = false
  EqualTolerance = true
  FormatSpec = %.2f
  FormatSpecOverTolerance = %+.2f
  FormatSpecUnderTolerance = %+.2f
  Inverted = false
  LockPosition = false
  MeasureType = 1
  OverTolerance = 0
  References2D = -> [ProjItem031]
  Rotation = 0
  ScaleType = 0
  TheoreticalExact = false
  Type = 2
  UnderTolerance = 0
  X = 63.7277
  Y = 30.9125
FEATURE [TechDraw::DrawViewDimension] Dimension259
  Arbitrary = false
  ArbitraryTolerances = false
  EqualTolerance = true
  FormatSpec = %.2f
  FormatSpecOverTolerance = %+.2f
  FormatSpecUnderTolerance = %+.2f
  Inverted = false
  LockPosition = false
  MeasureType = 1
  OverTolerance = 0
  References2D = -> [ProjItem031]
  Rotation = 0
  ScaleType = 0
  TheoreticalExact = false
  Type = 1
  UnderTolerance = 0
  X = 0
  Y = -39.59
FEATURE [TechDraw::DrawViewDimension] Dimension260
  Arbitrary = false
  ArbitraryTolerances = false
  EqualTolerance = true
  FormatSpec = %.2f
  FormatSpecOverTolerance = %+.2f
  FormatSpecUnderTolerance = %+.2f
  Inverted = false
  LockPosition = false
  MeasureType = 1
  OverTolerance = 0
  References2D = -> [ProjItem031]
  Rotation = 0
  ScaleType = 0
  TheoreticalExact = false
  Type = 1
  UnderTolerance = 0
  X = -50.3605
  Y = 46.8292
FEATURE [TechDraw::DrawViewDimension] Dimension261
  Arbitrary = false
  ArbitraryTolerances = false
  EqualTolerance = true
  FormatSpec = %.2f
  FormatSpecOverTolerance = %+.2f
  FormatSpecUnderTolerance = %+.2f
  Inverted = false
  LockPosition = false
  MeasureType = 1
  OverTolerance = 0
  References2D = -> [ProjItem030]
  Rotation = 0
  ScaleType = 0
  TheoreticalExact = false
  Type = 2
  UnderTolerance = 0
  X = -39.9131
  Y = -10.531
FEATURE [TechDraw::DrawViewDimension] Dimension262
  Arbitrary = false
  ArbitraryTolerances = false
  EqualTolerance = true
  FormatSpec = %.2f
  FormatSpecOverTolerance = %+.2f
  FormatSpecUnderTolerance = %+.2f
  Inverted = false
  LockPosition = false
  MeasureType = 1
  OverTolerance = 0
  References2D = -> [ProjItem030]
  Rotation = 0
  ScaleType = 0
  TheoreticalExact = false
  Type = 1
  UnderTolerance = 0
  X = -63.9326
  Y = 3.92609
FEATURE [TechDraw::DrawViewDimension] Dimension263
  Arbitrary = false
  ArbitraryTolerances = false
  EqualTolerance = true
  FormatSpec = %.2f
  FormatSpecOverTolerance = %+.2f
  FormatSpecUnderTolerance = %+.2f
  Inverted = false
  LockPosition = false
  MeasureType = 1
  OverTolerance = 0
  References2D = -> [ProjItem031]
  Rotation = 0
  ScaleType = 0
  TheoreticalExact = false
  Type = 2
  UnderTolerance = 0
  X = -66.6522
  Y = 0.945651
FEATURE [TechDraw::DrawViewDimension] Dimension264
  Arbitrary = false
  ArbitraryTolerances = false
  EqualTolerance = true
  FormatSpec = %.2f
  FormatSpecOverTolerance = %+.2f
  FormatSpecUnderTolerance = %+.2f
  Inverted = false
  LockPosition = false
  MeasureType = 1
  OverTolerance = 0
  References2D = -> [ProjItem032]
  Rotation = 0
  ScaleType = 0
  TheoreticalExact = false
  Type = 2
  UnderTolerance = 0
  X = -41.677
  Y = 70.6337
FEATURE [TechDraw::DrawViewDimension] Dimension265
  Arbitrary = false
  ArbitraryTolerances = false
  EqualTolerance = true
  FormatSpec = R%.2f
  FormatSpecOverTolerance = %+.2f
  FormatSpecUnderTolerance = %+.2f
  Inverted = false
  LockPosition = false
  MeasureType = 1
  OverTolerance = 0
  References2D = -> [ProjItem032]
  Rotation = 0
  ScaleType = 0
  TheoreticalExact = false
  Type = 4
  UnderTolerance = 0
  X = 88.1346
  Y = 67.7086
FEATURE [TechDraw::DrawViewDimension] Dimension266
  Arbitrary = false
  ArbitraryTolerances = false
  EqualTolerance = true
  FormatSpec = %.2f
  FormatSpecOverTolerance = %+.2f
  FormatSpecUnderTolerance = %+.2f
  Inverted = false
  LockPosition = false
  MeasureType = 1
  OverTolerance = 0
  References2D = -> [ProjItem032]
  Rotation = 0
  ScaleType = 0
  TheoreticalExact = false
  Type = 2
  UnderTolerance = 0
  X = 61.7772
  Y = 37.7674
FEATURE [TechDraw::DrawViewDimension] Dimension267
  Arbitrary = false
  ArbitraryTolerances = false
  EqualTolerance = true
  FormatSpec = %.2f
  FormatSpecOverTolerance = %+.2f
  FormatSpecUnderTolerance = %+.2f
  Inverted = false
  LockPosition = false
  MeasureType = 1
  OverTolerance = 0
  References2D = -> [ProjItem032]
  Rotation = 0
  ScaleType = 0
  TheoreticalExact = false
  Type = 1
  UnderTolerance = 0
  X = 88.2326
  Y = 44.6804
FEATURE [TechDraw::DrawViewDimension] Dimension268
  Arbitrary = false
  ArbitraryTolerances = false
  EqualTolerance = true
  FormatSpec = %.2f
  FormatSpecOverTolerance = %+.2f
  FormatSpecUnderTolerance = %+.2f
  Inverted = false
  LockPosition = false
  MeasureType = 1
  OverTolerance = 0
  References2D = -> [ProjItem032]
  Rotation = 0
  ScaleType = 0
  TheoreticalExact = false
  Type = 1
  UnderTolerance = 0
  X = 62.25
  Y = 14.4782
FEATURE [TechDraw::DrawViewDimension] Dimension269
  Arbitrary = false
  ArbitraryTolerances = false
  EqualTolerance = true
  FormatSpec = ⌀%.2f
  FormatSpecOverTolerance = %+.2f
  FormatSpecUnderTolerance = %+.2f
  Inverted = false
  LockPosition = false
  MeasureType = 1
  OverTolerance = 0
  References2D = -> [ProjItem032]
  Rotation = 0
  ScaleType = 0
  TheoreticalExact = false
  Type = 5
  UnderTolerance = 0
  X = 34.9891
  Y = -7.94346
FEATURE [TechDraw::DrawViewDimension] Dimension270
  Arbitrary = false
  ArbitraryTolerances = false
  EqualTolerance = true
  FormatSpec = %.2f
  FormatSpecOverTolerance = %+.2f
  FormatSpecUnderTolerance = %+.2f
  Inverted = false
  LockPosition = false
  MeasureType = 1
  OverTolerance = 0
  References2D = -> [ProjItem032]
  Rotation = 0
  ScaleType = 0
  TheoreticalExact = false
  Type = 1
  UnderTolerance = 0
  X = -61.5033
  Y = 12.5869
FEATURE [TechDraw::DrawViewDimension] Dimension271
  Arbitrary = false
  ArbitraryTolerances = false
  EqualTolerance = true
  FormatSpec = %.2f
  FormatSpecOverTolerance = %+.2f
  FormatSpecUnderTolerance = %+.2f
  Inverted = false
  LockPosition = false
  MeasureType = 1
  OverTolerance = 0
  References2D = -> [ProjItem032]
  Rotation = 0
  ScaleType = 0
  TheoreticalExact = false
  Type = 2
  UnderTolerance = 0
  X = -55.7902
  Y = -8.51739
FEATURE [TechDraw::DrawViewDimension] Dimension272
  Arbitrary = false
  ArbitraryTolerances = false
  EqualTolerance = true
  FormatSpec = %.2f
  FormatSpecOverTolerance = %+.2f
  FormatSpecUnderTolerance = %+.2f
  Inverted = false
  LockPosition = false
  MeasureType = 1
  OverTolerance = 0
  References2D = -> [ProjItem032]
  Rotation = 0
  ScaleType = 0
  TheoreticalExact = false
  Type = 2
  UnderTolerance = 0
  X = -65.7421
  Y = -64.8
FEATURE [TechDraw::DrawViewDimension] Dimension273
  Arbitrary = false
  ArbitraryTolerances = false
  EqualTolerance = true
  FormatSpec = %.2f
  FormatSpecOverTolerance = %+.2f
  FormatSpecUnderTolerance = %+.2f
  Inverted = false
  LockPosition = false
  MeasureType = 1
  OverTolerance = 0
  References2D = -> [ProjItem032]
  Rotation = 0
  ScaleType = 0
  TheoreticalExact = false
  Type = 2
  UnderTolerance = 0
  X = -55.6011
  Y = -31.4413
FEATURE [TechDraw::DrawViewDimension] Dimension274
  Arbitrary = false
  ArbitraryTolerances = false
  EqualTolerance = true
  FormatSpec = ⌀%.2f
  FormatSpecOverTolerance = %+.2f
  FormatSpecUnderTolerance = %+.2f
  Inverted = false
  LockPosition = false
  MeasureType = 1
  OverTolerance = 0
  References2D = -> [ProjItem032]
  Rotation = 0
  ScaleType = 0
  TheoreticalExact = false
  Type = 5
  UnderTolerance = 0
  X = -63.7368
  Y = 47.6608
FEATURE [TechDraw::DrawViewDimension] Dimension275
  Arbitrary = false
  ArbitraryTolerances = false
  EqualTolerance = true
  FormatSpec = %.2f
  FormatSpecOverTolerance = %+.2f
  FormatSpecUnderTolerance = %+.2f
  Inverted = false
  LockPosition = false
  MeasureType = 1
  OverTolerance = 0
  References2D = -> [ProjItem030]
  Rotation = 0
  ScaleType = 0
  TheoreticalExact = false
  Type = 2
  UnderTolerance = 0
  X = 61.0549
  Y = 49.2848
FEATURE [TechDraw::DrawViewDimension] Dimension276
  Arbitrary = false
  ArbitraryTolerances = false
  EqualTolerance = true
  FormatSpec = ⌀%.2f
  FormatSpecOverTolerance = %+.2f
  FormatSpecUnderTolerance = %+.2f
  Inverted = false
  LockPosition = false
  MeasureType = 1
  OverTolerance = 0
  References2D = -> [ProjItem031]
  Rotation = 0
  ScaleType = 0
  TheoreticalExact = false
  Type = 5
  UnderTolerance = 0
  X = 42.5543
  Y = 32.9086
FEATURE [TechDraw::DrawViewSymbol] Symbol010
  LockPosition = false
  Rotation = 0
  ScaleType = 2
  Symbol = <blob: 387326 chars omitted>
  X = 305.641
  Y = 32.5257
FEATURE [TechDraw::DrawPage] Page009  label="caja_bateria_drcha"
  KeepUpdated = true
  NextBalloonIndex = 1
  ProjectionType = 0
  Template = -> Template008
  Views = -> [ProjGroup008,Dimension156,Dimension157,Dimension158,Dimension159,Dimension165,Dimension178,View007,Dimension253,Dimension254,Dimension255,Dimension256,Dimension257,Dimension258,Dimension259,Dimension260,Dimension261,Dimension262,Dimension263,Dimension264,Dimension265,Dimension266,Dimension267,Dimension268,Dimension269,Dimension270,Dimension271,Dimension272,Dimension273,Dimension274,Dimension275,+2 more]
FEATURE [TechDraw::DrawProjGroupItem] ProjItem  label="Front"
  CoarseView = false
  Direction = (0,0,1)
  Focus = 100
  HardHidden = true
  IsoCount = 0
  IsoHidden = false
  IsoVisible = false
  LockPosition = true
  Perspective = false
  Rotation = 0
  RotationVector = (1,0,0)
  ScaleType = 2
  SeamHidden = false
  SeamVisible = true
  SmoothHidden = false
  SmoothVisible = true
  Source = -> [Cut001002086]
  Type = 0
  X = 0
  XDirection = (1e-16,1,0)
  Y = 0
FEATURE [TechDraw::DrawProjGroupItem] ProjItem045  label="Left"
  CoarseView = false
  Direction = (-1e-16,-1,1e-16)
  Focus = 100
  HardHidden = true
  IsoCount = 0
  IsoHidden = false
  IsoVisible = false
  LockPosition = true
  Perspective = false
  Rotation = 0
  RotationVector = (1,0,0)
  ScaleType = 2
  SeamHidden = false
  SeamVisible = true
  SmoothHidden = false
  SmoothVisible = true
  Source = -> [Cut001002086]
  Type = 1
  X = 180.444
  XDirection = (0,1e-16,1)
  Y = 0
FEATURE [TechDraw::DrawProjGroupItem] ProjItem046  label="Top"
  CoarseView = false
  Direction = (-1,1e-16,0)
  Focus = 100
  HardHidden = true
  IsoCount = 0
  IsoHidden = false
  IsoVisible = false
  LockPosition = true
  Perspective = false
  Rotation = 0
  RotationVector = (1,0,0)
  ScaleType = 2
  SeamHidden = false
  SeamVisible = true
  SmoothHidden = false
  SmoothVisible = true
  Source = -> [Cut001002086]
  Type = 4
  X = 0
  XDirection = (1e-16,1,0)
  Y = -112.496
FEATURE [TechDraw::DrawProjGroup] ProjGroup
  Anchor = -> ProjItem
  AutoDistribute = true
  LockPosition = false
  ProjectionType = 0
  Rotation = 0
  ScaleType = 0
  Source = -> [Cut001002086]
  Views = -> [ProjItem,ProjItem045,ProjItem046]
  X = 134.876
  Y = 222.226
  spacingX = 15
  spacingY = 15
FEATURE [TechDraw::DrawViewDimension] Dimension277
  Arbitrary = false
  ArbitraryTolerances = false
  EqualTolerance = true
  FormatSpec = ⌀%.2f
  FormatSpecOverTolerance = %+.2f
  FormatSpecUnderTolerance = %+.2f
  Inverted = false
  LockPosition = false
  MeasureType = 1
  OverTolerance = 0
  References2D = -> [ProjItem]
  Rotation = 0
  ScaleType = 0
  TheoreticalExact = false
  Type = 5
  UnderTolerance = 0
  X = 104.585
  Y = 57.3742
FEATURE [TechDraw::DrawViewDimension] Dimension278
  Arbitrary = false
  ArbitraryTolerances = false
  EqualTolerance = true
  FormatSpec = ⌀%.2f
  FormatSpecOverTolerance = %+.2f
  FormatSpecUnderTolerance = %+.2f
  Inverted = false
  LockPosition = false
  MeasureType = 1
  OverTolerance = 0
  References2D = -> [ProjItem]
  Rotation = 0
  ScaleType = 0
  TheoreticalExact = false
  Type = 5
  UnderTolerance = 0
  X = 106.006
  Y = 41.4187
FEATURE [TechDraw::DrawViewDimension] Dimension279
  Arbitrary = false
  ArbitraryTolerances = false
  EqualTolerance = true
  FormatSpec = R%.2f
  FormatSpecOverTolerance = %+.2f
  FormatSpecUnderTolerance = %+.2f
  Inverted = false
  LockPosition = false
  MeasureType = 1
  OverTolerance = 0
  References2D = -> [ProjItem]
  Rotation = 0
  ScaleType = 0
  TheoreticalExact = false
  Type = 4
  UnderTolerance = 0
  X = 75.0782
  Y = 4.48065
FEATURE [TechDraw::DrawViewDimension] Dimension280
  Arbitrary = false
  ArbitraryTolerances = false
  EqualTolerance = true
  FormatSpec = %.2f
  FormatSpecOverTolerance = %+.2f
  FormatSpecUnderTolerance = %+.2f
  Inverted = false
  LockPosition = false
  MeasureType = 1
  OverTolerance = 0
  References2D = -> [ProjItem]
  Rotation = 0
  ScaleType = 0
  TheoreticalExact = false
  Type = 1
  UnderTolerance = 0
  X = 47.4724
  Y = -55.474
FEATURE [TechDraw::DrawViewDimension] Dimension281
  Arbitrary = false
  ArbitraryTolerances = false
  EqualTolerance = true
  FormatSpec = %.2f
  FormatSpecOverTolerance = %+.2f
  FormatSpecUnderTolerance = %+.2f
  Inverted = false
  LockPosition = false
  MeasureType = 1
  OverTolerance = 0
  References2D = -> [ProjItem]
  Rotation = 0
  ScaleType = 0
  TheoreticalExact = false
  Type = 1
  UnderTolerance = 0
  X = 106.967
  Y = -55.3542
FEATURE [TechDraw::DrawViewDimension] Dimension282
  Arbitrary = false
  ArbitraryTolerances = false
  EqualTolerance = true
  FormatSpec = %.2f
  FormatSpecOverTolerance = %+.2f
  FormatSpecUnderTolerance = %+.2f
  Inverted = false
  LockPosition = false
  MeasureType = 1
  OverTolerance = 0
  References2D = -> [ProjItem]
  Rotation = 0
  ScaleType = 0
  TheoreticalExact = false
  Type = 1
  UnderTolerance = 0
  X = 2.14293
  Y = -55.243
FEATURE [TechDraw::DrawViewDimension] Dimension283
  Arbitrary = false
  ArbitraryTolerances = false
  EqualTolerance = true
  FormatSpec = %.2f
  FormatSpecOverTolerance = %+.2f
  FormatSpecUnderTolerance = %+.2f
  Inverted = false
  LockPosition = false
  MeasureType = 1
  OverTolerance = 0
  References2D = -> [ProjItem]
  Rotation = 0
  ScaleType = 0
  TheoreticalExact = false
  Type = 2
  UnderTolerance = 0
  X = -104.722
  Y = -59.2818
FEATURE [TechDraw::DrawViewDimension] Dimension284
  Arbitrary = false
  ArbitraryTolerances = false
  EqualTolerance = true
  FormatSpec = %.2f
  FormatSpecOverTolerance = %+.2f
  FormatSpecUnderTolerance = %+.2f
  Inverted = false
  LockPosition = false
  MeasureType = 1
  OverTolerance = 0
  References2D = -> [ProjItem]
  Rotation = 0
  ScaleType = 0
  TheoreticalExact = false
  Type = 2
  UnderTolerance = 0
  X = -105.4
  Y = -0.115516
FEATURE [TechDraw::DrawViewDimension] Dimension285
  Arbitrary = false
  ArbitraryTolerances = false
  EqualTolerance = true
  FormatSpec = %.2f
  FormatSpecOverTolerance = %+.2f
  FormatSpecUnderTolerance = %+.2f
  Inverted = false
  LockPosition = false
  MeasureType = 1
  OverTolerance = 0
  References2D = -> [ProjItem]
  Rotation = 0
  ScaleType = 0
  TheoreticalExact = false
  Type = 2
  UnderTolerance = 0
  X = -105.703
  Y = 44.231
FEATURE [TechDraw::DrawViewDimension] Dimension286
  Arbitrary = false
  ArbitraryTolerances = false
  EqualTolerance = true
  FormatSpec = %.2f
  FormatSpecOverTolerance = %+.2f
  FormatSpecUnderTolerance = %+.2f
  Inverted = false
  LockPosition = false
  MeasureType = 1
  OverTolerance = 0
  References2D = -> [ProjItem]
  Rotation = 0
  ScaleType = 0
  TheoreticalExact = false
  Type = 1
  UnderTolerance = 0
  X = -86.231
  Y = 61.7033
FEATURE [TechDraw::DrawViewDimension] Dimension287
  Arbitrary = false
  ArbitraryTolerances = false
  EqualTolerance = true
  FormatSpec = %.2f
  FormatSpecOverTolerance = %+.2f
  FormatSpecUnderTolerance = %+.2f
  Inverted = false
  LockPosition = false
  MeasureType = 1
  OverTolerance = 0
  References2D = -> [ProjItem046]
  Rotation = 0
  ScaleType = 0
  TheoreticalExact = false
  Type = 2
  UnderTolerance = 0
  X = -105.598
  Y = -4.04986
FEATURE [TechDraw::DrawViewDimension] Dimension288
  Arbitrary = false
  ArbitraryTolerances = false
  EqualTolerance = true
  FormatSpec = %.2f
  FormatSpecOverTolerance = %+.2f
  FormatSpecUnderTolerance = %+.2f
  Inverted = false
  LockPosition = false
  MeasureType = 1
  OverTolerance = 0
  References2D = -> [ProjItem046]
  Rotation = 0
  ScaleType = 0
  TheoreticalExact = false
  Type = 1
  UnderTolerance = 0
  X = 0
  Y = -16.9976
FEATURE [TechDraw::DrawViewDimension] Dimension289
  Arbitrary = false
  ArbitraryTolerances = false
  EqualTolerance = true
  FormatSpec = %.2f
  FormatSpecOverTolerance = %+.2f
  FormatSpecUnderTolerance = %+.2f
  Inverted = false
  LockPosition = false
  MeasureType = 1
  OverTolerance = 0
  References2D = -> [ProjItem]
  Rotation = 0
  ScaleType = 0
  TheoreticalExact = false
  Type = 1
  UnderTolerance = 0
  X = 46.5003
  Y = 61.3961
FEATURE [TechDraw::DrawViewDimension] Dimension290
  Arbitrary = false
  ArbitraryTolerances = false
  EqualTolerance = true
  FormatSpec = %.2f
  FormatSpecOverTolerance = %+.2f
  FormatSpecUnderTolerance = %+.2f
  Inverted = false
  LockPosition = false
  MeasureType = 1
  OverTolerance = 0
  References2D = -> [ProjItem046]
  Rotation = 0
  ScaleType = 0
  TheoreticalExact = false
  Type = 1
  UnderTolerance = 0
  X = 88.7962
  Y = 16.6976
FEATURE [TechDraw::DrawViewDimension] Dimension291
  Arbitrary = false
  ArbitraryTolerances = false
  EqualTolerance = true
  FormatSpec = %.2f
  FormatSpecOverTolerance = %+.2f
  FormatSpecUnderTolerance = %+.2f
  Inverted = false
  LockPosition = false
  MeasureType = 1
  OverTolerance = 0
  References2D = -> [ProjItem046]
  Rotation = 0
  ScaleType = 0
  TheoreticalExact = false
  Type = 1
  UnderTolerance = 0
  X = 38.4967
  Y = 17.2467
FEATURE [TechDraw::DrawViewDimension] Dimension292
  Arbitrary = false
  ArbitraryTolerances = false
  EqualTolerance = true
  FormatSpec = %.2f
  FormatSpecOverTolerance = %+.2f
  FormatSpecUnderTolerance = %+.2f
  Inverted = false
  LockPosition = false
  MeasureType = 1
  OverTolerance = 0
  References2D = -> [ProjItem046]
  Rotation = 0
  ScaleType = 0
  TheoreticalExact = false
  Type = 2
  UnderTolerance = 0
  X = 103.615
  Y = -5.58117
FEATURE [TechDraw::DrawViewDimension] Dimension293
  Arbitrary = false
  ArbitraryTolerances = false
  EqualTolerance = true
  FormatSpec = %.2f
  FormatSpecOverTolerance = %+.2f
  FormatSpecUnderTolerance = %+.2f
  Inverted = false
  LockPosition = false
  MeasureType = 1
  OverTolerance = 0
  References2D = -> [ProjItem045]
  Rotation = 0
  ScaleType = 0
  TheoreticalExact = false
  Type = 1
  UnderTolerance = 0
  X = 13.1894
  Y = 61.6976
FEATURE [TechDraw::DrawViewDimension] Dimension294
  Arbitrary = false
  ArbitraryTolerances = false
  EqualTolerance = true
  FormatSpec = %.2f
  FormatSpecOverTolerance = %+.2f
  FormatSpecUnderTolerance = %+.2f
  Inverted = false
  LockPosition = false
  MeasureType = 1
  OverTolerance = 0
  References2D = -> [ProjItem045]
  Rotation = 0
  ScaleType = 0
  TheoreticalExact = false
  Type = 2
  UnderTolerance = 0
  X = 13.9458
  Y = 2.19315
FEATURE [TechDraw::DrawViewDimension] Dimension295
  Arbitrary = false
  ArbitraryTolerances = false
  EqualTolerance = true
  FormatSpec = %.2f
  FormatSpecOverTolerance = %+.2f
  FormatSpecUnderTolerance = %+.2f
  Inverted = false
  LockPosition = false
  MeasureType = 1
  OverTolerance = 0
  References2D = -> [ProjItem045]
  Rotation = 0
  ScaleType = 0
  TheoreticalExact = false
  Type = 2
  UnderTolerance = 0
  X = -16.3825
  Y = 0.46996
FEATURE [TechDraw::DrawViewDimension] Dimension296
  Arbitrary = false
  ArbitraryTolerances = false
  EqualTolerance = true
  FormatSpec = %.2f
  FormatSpecOverTolerance = %+.2f
  FormatSpecUnderTolerance = %+.2f
  Inverted = false
  LockPosition = false
  MeasureType = 1
  OverTolerance = 0
  References2D = -> [ProjItem045]
  Rotation = 0
  ScaleType = 0
  TheoreticalExact = false
  Type = 1
  UnderTolerance = 0
  X = 16.7623
  Y = -56.0361
FEATURE [TechDraw::DrawViewDimension] Dimension297
  Arbitrary = false
  ArbitraryTolerances = false
  EqualTolerance = true
  FormatSpec = %.2f
  FormatSpecOverTolerance = %+.2f
  FormatSpecUnderTolerance = %+.2f
  Inverted = false
  LockPosition = false
  MeasureType = 1
  OverTolerance = 0
  References2D = -> [ProjItem045]
  Rotation = 0
  ScaleType = 0
  TheoreticalExact = false
  Type = 1
  UnderTolerance = 0
  X = -18.0873
  Y = 53.13
FEATURE [TechDraw::DrawPage] Page  label="Soporte_Celda_General"
  KeepUpdated = true
  NextBalloonIndex = 1
  ProjectionType = 0
  Template = -> Template
  Views = -> [View001,Symbol,ProjGroup,Dimension277,Dimension278,Dimension279,Dimension280,Dimension281,Dimension282,Dimension283,Dimension284,Dimension285,Dimension286,Dimension287,Dimension288,Dimension289,Dimension290,Dimension291,Dimension292,Dimension293,Dimension294,Dimension295,Dimension296,Dimension297]
FEATURE [TechDraw::DrawViewBalloon] Balloon
  BubbleShape = 0
  EndType = 0
  EndTypeScale = 1
  KinkLength = 5
  LockPosition = false
  OriginX = -142.497
  OriginY = 7.76197
  Rotation = 0
  ScaleType = 0
  ShapeScale = 1
  SourceView = -> ProjItem015
  Text = 1
  TextWrapLen = -1
  X = -199.244
  Y = 123.373
FEATURE [TechDraw::DrawViewBalloon] Balloon011
  BubbleShape = 0
  EndType = 0
  EndTypeScale = 1
  KinkLength = 5
  LockPosition = false
  OriginX = -0.0529144
  OriginY = 12.0353
  Rotation = 0
  ScaleType = 0
  ShapeScale = 1
  SourceView = -> ProjItem015
  Text = 2
  TextWrapLen = -1
  X = -62.4974
  Y = 130.495
FEATURE [TechDraw::DrawViewBalloon] Balloon012
  BubbleShape = 0
  EndType = 0
  EndTypeScale = 1
  KinkLength = 5
  LockPosition = false
  OriginX = 125.298
  OriginY = 16.3086
  Rotation = 0
  ScaleType = 0
  ShapeScale = 1
  SourceView = -> ProjItem015
  Text = 3
  TextWrapLen = -1
  X = 201.025
  Y = 131.92
FEATURE [TechDraw::DrawViewBalloon] Balloon013
  BubbleShape = 0
  EndType = 0
  EndTypeScale = 1
  KinkLength = 5
  LockPosition = false
  OriginX = -106.253
  OriginY = 106.567
  Rotation = 0
  ScaleType = 0
  ShapeScale = 1
  SourceView = -> ProjItem021
  Text = 4
  TextWrapLen = -1
  X = -19.1307
  Y = 230.725
FEATURE [TechDraw::DrawViewBalloon] Balloon014
  BubbleShape = 0
  EndType = 0
  EndTypeScale = 1
  KinkLength = 5
  LockPosition = false
  OriginX = 53.2849
  OriginY = 68.1068
  Rotation = 0
  ScaleType = 0
  ShapeScale = 1
  SourceView = -> ProjItem021
  Text = 5
  TextWrapLen = -1
  X = 133.285
  Y = 190.84
FEATURE [TechDraw::DrawViewBalloon] Balloon015
  BubbleShape = 0
  EndType = 0
  EndTypeScale = 1
  KinkLength = 5
  LockPosition = false
  OriginX = 138.752
  OriginY = -10.2377
  Rotation = 0
  ScaleType = 0
  ShapeScale = 1
  SourceView = -> ProjItem021
  Text = 6
  TextWrapLen = -1
  X = 232.996
  Y = 125.316
FEATURE [TechDraw::DrawViewSymbol] Symbol011
  LockPosition = false
  Rotation = 0
  ScaleType = 2
  Symbol = <blob: 387326 chars omitted>
  X = 306.506
  Y = 33.4761
FEATURE [TechDraw::DrawPage] Page006  label="Caja_bateria_general"
  KeepUpdated = true
  NextBalloonIndex = 14
  ProjectionType = 0
  Template = -> Template005
  Views = -> [ProjGroup005,Dimension085,Sheet001,Balloon,Balloon011,Balloon012,Balloon013,Balloon014,Balloon015,Symbol011]
FEATURE [TechDraw::DrawViewDimension] Dimension298
  Arbitrary = false
  ArbitraryTolerances = false
  EqualTolerance = true
  FormatSpec = %.2f
  FormatSpecOverTolerance = %+.2f
  FormatSpecUnderTolerance = %+.2f
  Inverted = false
  LockPosition = false
  MeasureType = 1
  OverTolerance = 0
  References2D = -> [ProjItem027]
  Rotation = 0
  ScaleType = 0
  TheoreticalExact = false
  Type = 1
  UnderTolerance = 0
  X = 89.2835
  Y = 48.9538
FEATURE [TechDraw::DrawViewDimension] Dimension127
  Arbitrary = false
  ArbitraryTolerances = false
  EqualTolerance = true
  FormatSpec = %.2f
  FormatSpecOverTolerance = %+.2f
  FormatSpecUnderTolerance = %+.2f
  Inverted = false
  LockPosition = false
  MeasureType = 1
  OverTolerance = 0
  References2D = -> [ProjItem029]
  Rotation = 0
  ScaleType = 0
  TheoreticalExact = false
  Type = 2
  UnderTolerance = 0
  X = 62.2065
  Y = -14.2211
FEATURE [TechDraw::DrawViewDimension] Dimension299
  Arbitrary = false
  ArbitraryTolerances = false
  EqualTolerance = true
  FormatSpec = %.2f
  FormatSpecOverTolerance = %+.2f
  FormatSpecUnderTolerance = %+.2f
  Inverted = false
  LockPosition = false
  MeasureType = 1
  OverTolerance = 0
  References2D = -> [ProjItem029]
  Rotation = 0
  ScaleType = 0
  TheoreticalExact = false
  Type = 2
  UnderTolerance = 0
  X = 62.2884
  Y = 31.4356
FEATURE [TechDraw::DrawPage] Page008  label="Caja_bateria_central"
  KeepUpdated = true
  NextBalloonIndex = 1
  ProjectionType = 0
  Template = -> Template007
  Views = -> [ProjGroup007,Dimension120,Dimension126,Dimension127,Dimension128,Dimension129,Dimension130,Dimension136,View006,Dimension233,Dimension234,Dimension235,Dimension236,Dimension237,Dimension238,Dimension239,Dimension240,Dimension241,Dimension242,Dimension243,Dimension244,Dimension245,Dimension246,Dimension247,Dimension248,Dimension249,Dimension250,Dimension251,Dimension252,Symbol009,Dimension298,+1 more]
FEATURE [App::DocumentObjectGroup] Group029  label="Planimetria"
  Group = -> [Page,Page003,Page004,Page005,Page007,Page008,Page009,Page010,Page011,Page012,Page013,Page006,Spreadsheet]
note: 4 file-system paths scrubbed to <path> (originals preserved in the JSON sidecar)
